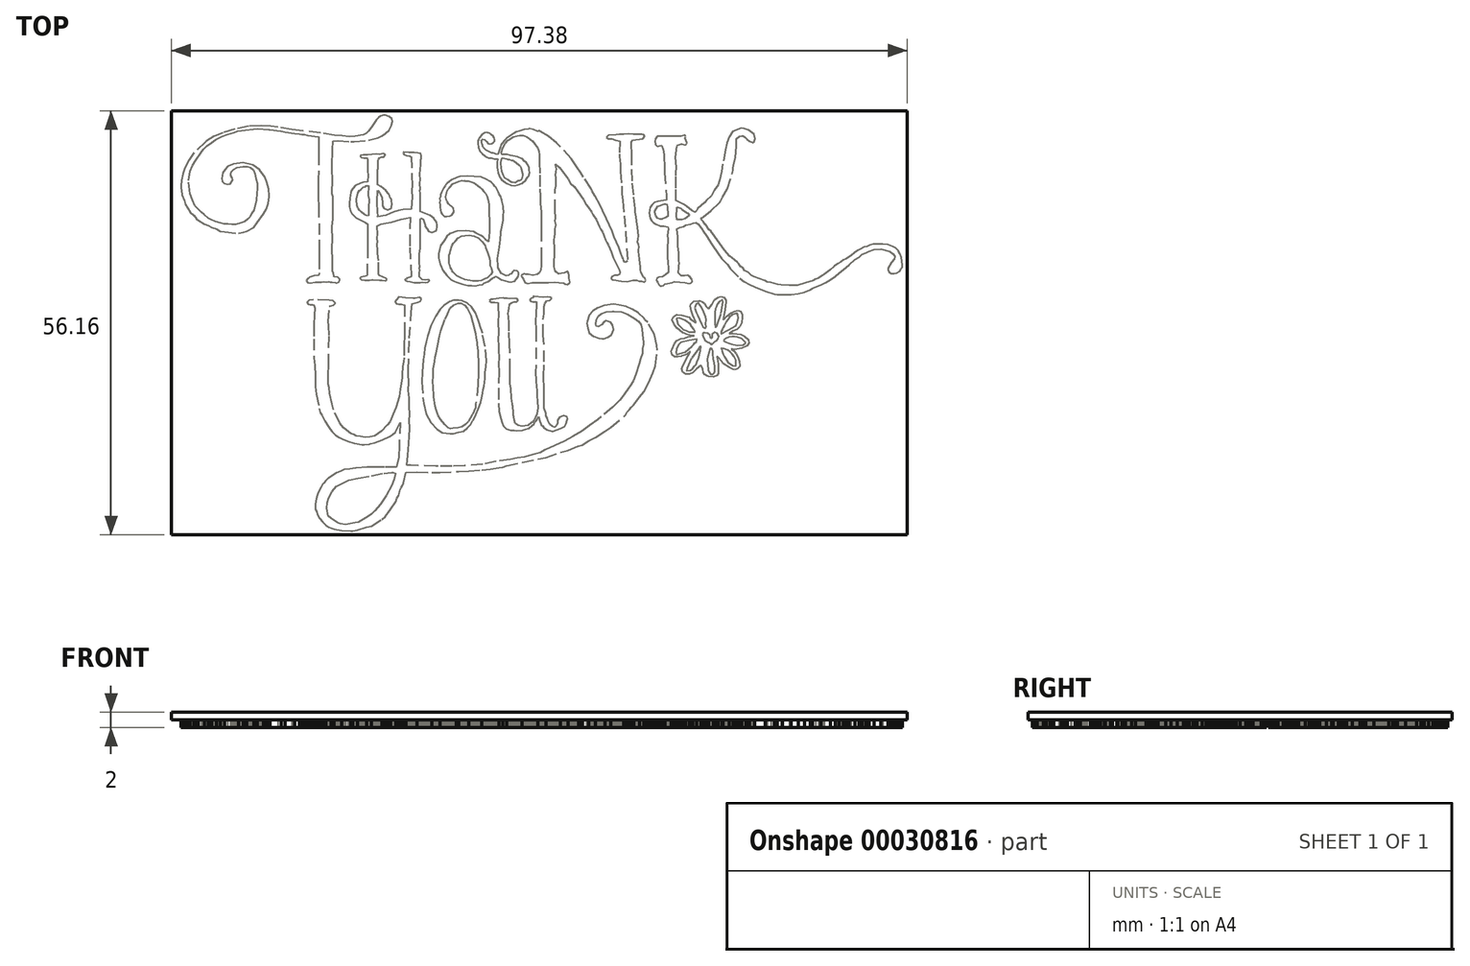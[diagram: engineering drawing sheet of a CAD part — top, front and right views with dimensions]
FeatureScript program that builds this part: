
annotation { "Feature Type Name" : "Feature", "Feature Type Description" : "" }
export const myFeature = defineFeature(function(context is Context, id is Id, definition is map)
    precondition{}
    {
        {
            var Q0;
            Q0=qCreatedBy(makeId("Top.planeOp"),FACE);
            var sketch = newSketch(context, id + "F0", { "sketchPlane" : qUnion([Q0])});
            skLineSegment(sketch, "E0", {"start": v(-26.64, -26.6) * mm, "end": v(-26.83, -26.5) * mm});
            skLineSegment(sketch, "E1", {"start": v(-26.83, -26.5) * mm, "end": v(-27.1, -26.42) * mm});
            skLineSegment(sketch, "E2", {"start": v(-27.1, -26.42) * mm, "end": v(-27.5, -26.13) * mm});
            skLineSegment(sketch, "E3", {"start": v(-27.5, -26.13) * mm, "end": v(-27.9, -25.88) * mm});
            skLineSegment(sketch, "E4", {"start": v(-27.9, -25.88) * mm, "end": v(-28.23, -25.57) * mm});
            skLineSegment(sketch, "E5", {"start": v(-28.23, -25.57) * mm, "end": v(-28.44, -24.57) * mm});
            skLineSegment(sketch, "E6", {"start": v(-28.44, -24.57) * mm, "end": v(-28.37, -23.8) * mm});
            skLineSegment(sketch, "E7", {"start": v(-28.37, -23.8) * mm, "end": v(-28.18, -23.16) * mm});
            skLineSegment(sketch, "E8", {"start": v(-28.18, -23.16) * mm, "end": v(-27.73, -22.34) * mm});
            skLineSegment(sketch, "E9", {"start": v(-27.73, -22.34) * mm, "end": v(-27.17, -21.66) * mm});
            skLineSegment(sketch, "E10", {"start": v(-27.17, -21.66) * mm, "end": v(-26.54, -21.29) * mm});
            skLineSegment(sketch, "E11", {"start": v(-26.54, -21.29) * mm, "end": v(-25.52, -20.83) * mm});
            skLineSegment(sketch, "E12", {"start": v(-25.52, -20.83) * mm, "end": v(-24.32, -20.52) * mm});
            skLineSegment(sketch, "E13", {"start": v(-24.32, -20.52) * mm, "end": v(-22.57, -20.23) * mm});
            skLineSegment(sketch, "E14", {"start": v(-22.57, -20.23) * mm, "end": v(-20.9, -19.88) * mm});
            skLineSegment(sketch, "E15", {"start": v(-20.9, -19.88) * mm, "end": v(-19.84, -19.8) * mm});
            skLineSegment(sketch, "E16", {"start": v(-19.84, -19.8) * mm, "end": v(-19.66, -19.78) * mm});
            skLineSegment(sketch, "E17", {"start": v(-19.66, -19.78) * mm, "end": v(-19.37, -19.88) * mm});
            skLineSegment(sketch, "E18", {"start": v(-19.37, -19.88) * mm, "end": v(-19.55, -20.76) * mm});
            skLineSegment(sketch, "E19", {"start": v(-19.55, -20.76) * mm, "end": v(-19.9, -21.55) * mm});
            skLineSegment(sketch, "E20", {"start": v(-19.9, -21.55) * mm, "end": v(-20.56, -22.85) * mm});
            skLineSegment(sketch, "E21", {"start": v(-20.56, -22.85) * mm, "end": v(-21.33, -23.96) * mm});
            skLineSegment(sketch, "E22", {"start": v(-21.33, -23.96) * mm, "end": v(-22.07, -24.88) * mm});
            skLineSegment(sketch, "E23", {"start": v(-22.07, -24.88) * mm, "end": v(-22.52, -25.28) * mm});
            skLineSegment(sketch, "E24", {"start": v(-22.52, -25.28) * mm, "end": v(-22.96, -25.65) * mm});
            skLineSegment(sketch, "E25", {"start": v(-22.96, -25.65) * mm, "end": v(-23.6, -26.02) * mm});
            skLineSegment(sketch, "E26", {"start": v(-23.6, -26.02) * mm, "end": v(-24.24, -26.37) * mm});
            skLineSegment(sketch, "E27", {"start": v(-24.24, -26.37) * mm, "end": v(-24.68, -26.47) * mm});
            skLineSegment(sketch, "E28", {"start": v(-24.68, -26.47) * mm, "end": v(-25.98, -26.74) * mm});
            skLineSegment(sketch, "E29", {"start": v(-25.98, -26.74) * mm, "end": v(-26.64, -26.6) * mm});
            skLineSegment(sketch, "E30", {"start": v(-19.42, 2.85) * mm, "end": v(-19.42, 2.82) * mm});
            skLineSegment(sketch, "E31", {"start": v(-19.42, 2.82) * mm, "end": v(-19.23, 2.55) * mm});
            skLineSegment(sketch, "E32", {"start": v(-19.23, 2.55) * mm, "end": v(-18.94, 2.53) * mm});
            skLineSegment(sketch, "E33", {"start": v(-18.94, 2.53) * mm, "end": v(-18.6, 2.53) * mm});
            skLineSegment(sketch, "E34", {"start": v(-18.6, 2.53) * mm, "end": v(-18.15, 2.37) * mm});
            skLineSegment(sketch, "E35", {"start": v(-18.15, 2.37) * mm, "end": v(-18.15, -0.46) * mm});
            skLineSegment(sketch, "E36", {"start": v(-18.15, -0.46) * mm, "end": v(-18.18, -1.05) * mm});
            skLineSegment(sketch, "E37", {"start": v(-18.18, -1.05) * mm, "end": v(-18.18, -1.15) * mm});
            skLineSegment(sketch, "E38", {"start": v(-18.18, -1.15) * mm, "end": v(-18.15, -1.36) * mm});
            skLineSegment(sketch, "E39", {"start": v(-18.15, -1.36) * mm, "end": v(-18.18, -1.73) * mm});
            skLineSegment(sketch, "E40", {"start": v(-18.18, -1.73) * mm, "end": v(-18.2, -2.77) * mm});
            skLineSegment(sketch, "E41", {"start": v(-18.2, -2.77) * mm, "end": v(-18.2, -4.62) * mm});
            skLineSegment(sketch, "E42", {"start": v(-18.2, -4.62) * mm, "end": v(-18.3, -5.15) * mm});
            skLineSegment(sketch, "E43", {"start": v(-18.3, -5.15) * mm, "end": v(-18.39, -5.73) * mm});
            skLineSegment(sketch, "E44", {"start": v(-18.39, -5.73) * mm, "end": v(-18.5, -6.84) * mm});
            skLineSegment(sketch, "E45", {"start": v(-18.5, -6.84) * mm, "end": v(-18.47, -7.13) * mm});
            skLineSegment(sketch, "E46", {"start": v(-18.47, -7.13) * mm, "end": v(-18.47, -7.2) * mm});
            skLineSegment(sketch, "E47", {"start": v(-18.47, -7.2) * mm, "end": v(-18.55, -7.69) * mm});
            skLineSegment(sketch, "E48", {"start": v(-18.55, -7.69) * mm, "end": v(-18.7, -8.72) * mm});
            skLineSegment(sketch, "E49", {"start": v(-18.7, -8.72) * mm, "end": v(-18.86, -9.75) * mm});
            skLineSegment(sketch, "E50", {"start": v(-18.86, -9.75) * mm, "end": v(-19.31, -11.23) * mm});
            skLineSegment(sketch, "E51", {"start": v(-19.31, -11.23) * mm, "end": v(-19.71, -12.1) * mm});
            skLineSegment(sketch, "E52", {"start": v(-19.71, -12.1) * mm, "end": v(-20.08, -13.03) * mm});
            skLineSegment(sketch, "E53", {"start": v(-20.08, -13.03) * mm, "end": v(-20.45, -13.5) * mm});
            skLineSegment(sketch, "E54", {"start": v(-20.45, -13.5) * mm, "end": v(-21.19, -14.34) * mm});
            skLineSegment(sketch, "E55", {"start": v(-21.19, -14.34) * mm, "end": v(-22.12, -14.94) * mm});
            skLineSegment(sketch, "E56", {"start": v(-22.12, -14.94) * mm, "end": v(-22.72, -15.07) * mm});
            skLineSegment(sketch, "E57", {"start": v(-22.72, -15.07) * mm, "end": v(-23.34, -15.12) * mm});
            skLineSegment(sketch, "E58", {"start": v(-23.34, -15.12) * mm, "end": v(-23.99, -15.05) * mm});
            skLineSegment(sketch, "E59", {"start": v(-23.99, -15.05) * mm, "end": v(-24.58, -14.94) * mm});
            skLineSegment(sketch, "E60", {"start": v(-24.58, -14.94) * mm, "end": v(-24.87, -14.75) * mm});
            skLineSegment(sketch, "E61", {"start": v(-24.87, -14.75) * mm, "end": v(-25.24, -14.65) * mm});
            skLineSegment(sketch, "E62", {"start": v(-25.24, -14.65) * mm, "end": v(-25.53, -14.43) * mm});
            skLineSegment(sketch, "E63", {"start": v(-25.53, -14.43) * mm, "end": v(-26.2, -13.9) * mm});
            skLineSegment(sketch, "E64", {"start": v(-26.2, -13.9) * mm, "end": v(-26.72, -13.24) * mm});
            skLineSegment(sketch, "E65", {"start": v(-26.72, -13.24) * mm, "end": v(-27.57, -11.47) * mm});
            skLineSegment(sketch, "E66", {"start": v(-27.57, -11.47) * mm, "end": v(-27.73, -10.73) * mm});
            skLineSegment(sketch, "E67", {"start": v(-27.73, -10.73) * mm, "end": v(-28.07, -9.3) * mm});
            skLineSegment(sketch, "E68", {"start": v(-28.07, -9.3) * mm, "end": v(-28.15, -8.56) * mm});
            skLineSegment(sketch, "E69", {"start": v(-28.15, -8.56) * mm, "end": v(-28.26, -8.08) * mm});
            skLineSegment(sketch, "E70", {"start": v(-28.26, -8.08) * mm, "end": v(-28.28, -7.45) * mm});
            skLineSegment(sketch, "E71", {"start": v(-28.28, -7.45) * mm, "end": v(-28.28, -6.81) * mm});
            skLineSegment(sketch, "E72", {"start": v(-28.28, -6.81) * mm, "end": v(-28.2, -5.57) * mm});
            skLineSegment(sketch, "E73", {"start": v(-28.2, -5.57) * mm, "end": v(-28.12, -1.63) * mm});
            skLineSegment(sketch, "E74", {"start": v(-28.12, -1.63) * mm, "end": v(-28.2, -0.33) * mm});
            skLineSegment(sketch, "E75", {"start": v(-28.2, -0.33) * mm, "end": v(-28.23, 0.2) * mm});
            skLineSegment(sketch, "E76", {"start": v(-28.23, 0.2) * mm, "end": v(-28.12, 2.24) * mm});
            skLineSegment(sketch, "E77", {"start": v(-28.12, 2.24) * mm, "end": v(-28.02, 2.24) * mm});
            skLineSegment(sketch, "E78", {"start": v(-28.02, 2.24) * mm, "end": v(-27.57, 2.35) * mm});
            skLineSegment(sketch, "E79", {"start": v(-27.57, 2.35) * mm, "end": v(-27.33, 2.63) * mm});
            skLineSegment(sketch, "E80", {"start": v(-27.33, 2.63) * mm, "end": v(-27.6, 2.98) * mm});
            skLineSegment(sketch, "E81", {"start": v(-27.6, 2.98) * mm, "end": v(-28.15, 3) * mm});
            skLineSegment(sketch, "E82", {"start": v(-28.15, 3) * mm, "end": v(-30.19, 3.08) * mm});
            skLineSegment(sketch, "E83", {"start": v(-30.19, 3.08) * mm, "end": v(-30.8, 3.03) * mm});
            skLineSegment(sketch, "E84", {"start": v(-30.8, 3.03) * mm, "end": v(-31.06, 2.74) * mm});
            skLineSegment(sketch, "E85", {"start": v(-31.06, 2.74) * mm, "end": v(-31.06, 2.71) * mm});
            skLineSegment(sketch, "E86", {"start": v(-31.06, 2.71) * mm, "end": v(-30.93, 2.53) * mm});
            skLineSegment(sketch, "E87", {"start": v(-30.93, 2.53) * mm, "end": v(-30.66, 2.47) * mm});
            skLineSegment(sketch, "E88", {"start": v(-30.66, 2.47) * mm, "end": v(-30.36, 2.45) * mm});
            skLineSegment(sketch, "E89", {"start": v(-30.36, 2.45) * mm, "end": v(-30.14, 2.37) * mm});
            skLineSegment(sketch, "E90", {"start": v(-30.14, 2.37) * mm, "end": v(-30.03, 1.97) * mm});
            skLineSegment(sketch, "E91", {"start": v(-30.03, 1.97) * mm, "end": v(-30.1, 1.05) * mm});
            skLineSegment(sketch, "E92", {"start": v(-30.1, 1.05) * mm, "end": v(-30.14, -0.25) * mm});
            skLineSegment(sketch, "E93", {"start": v(-30.14, -0.25) * mm, "end": v(-30.14, -2.1) * mm});
            skLineSegment(sketch, "E94", {"start": v(-30.14, -2.1) * mm, "end": v(-30.16, -4.33) * mm});
            skLineSegment(sketch, "E95", {"start": v(-30.16, -4.33) * mm, "end": v(-30.16, -4.6) * mm});
            skLineSegment(sketch, "E96", {"start": v(-30.16, -4.6) * mm, "end": v(-30.06, -5.6) * mm});
            skLineSegment(sketch, "E97", {"start": v(-30.06, -5.6) * mm, "end": v(-29.98, -6.97) * mm});
            skLineSegment(sketch, "E98", {"start": v(-29.98, -6.97) * mm, "end": v(-29.95, -7.66) * mm});
            skLineSegment(sketch, "E99", {"start": v(-29.95, -7.66) * mm, "end": v(-29.98, -8.24) * mm});
            skLineSegment(sketch, "E100", {"start": v(-29.98, -8.24) * mm, "end": v(-29.98, -8.4) * mm});
            skLineSegment(sketch, "E101", {"start": v(-29.98, -8.4) * mm, "end": v(-29.82, -9.4) * mm});
            skLineSegment(sketch, "E102", {"start": v(-29.82, -9.4) * mm, "end": v(-29.45, -11.36) * mm});
            skLineSegment(sketch, "E103", {"start": v(-29.45, -11.36) * mm, "end": v(-29.33, -11.82) * mm});
            skLineSegment(sketch, "E104", {"start": v(-29.33, -11.82) * mm, "end": v(-29.1, -12.24) * mm});
            skLineSegment(sketch, "E105", {"start": v(-29.1, -12.24) * mm, "end": v(-28.72, -13.02) * mm});
            skLineSegment(sketch, "E106", {"start": v(-28.72, -13.02) * mm, "end": v(-28.28, -13.72) * mm});
            skLineSegment(sketch, "E107", {"start": v(-28.28, -13.72) * mm, "end": v(-28, -14.06) * mm});
            skLineSegment(sketch, "E108", {"start": v(-28, -14.06) * mm, "end": v(-27.73, -14.4) * mm});
            skLineSegment(sketch, "E109", {"start": v(-27.73, -14.4) * mm, "end": v(-27.3, -14.84) * mm});
            skLineSegment(sketch, "E110", {"start": v(-27.3, -14.84) * mm, "end": v(-26.78, -15.17) * mm});
            skLineSegment(sketch, "E111", {"start": v(-26.78, -15.17) * mm, "end": v(-26.43, -15.36) * mm});
            skLineSegment(sketch, "E112", {"start": v(-26.43, -15.36) * mm, "end": v(-25.66, -15.67) * mm});
            skLineSegment(sketch, "E113", {"start": v(-25.66, -15.67) * mm, "end": v(-24.84, -15.89) * mm});
            skLineSegment(sketch, "E114", {"start": v(-24.84, -15.89) * mm, "end": v(-24.74, -15.91) * mm});
            skLineSegment(sketch, "E115", {"start": v(-24.74, -15.91) * mm, "end": v(-23.81, -16.1) * mm});
            skLineSegment(sketch, "E116", {"start": v(-23.81, -16.1) * mm, "end": v(-23.47, -16.13) * mm});
            skLineSegment(sketch, "E117", {"start": v(-23.47, -16.13) * mm, "end": v(-22.78, -16.02) * mm});
            skLineSegment(sketch, "E118", {"start": v(-22.78, -16.02) * mm, "end": v(-22.67, -16) * mm});
            skLineSegment(sketch, "E119", {"start": v(-22.67, -16) * mm, "end": v(-22.1, -15.84) * mm});
            skLineSegment(sketch, "E120", {"start": v(-22.1, -15.84) * mm, "end": v(-21.09, -15.46) * mm});
            skLineSegment(sketch, "E121", {"start": v(-21.09, -15.46) * mm, "end": v(-20.13, -15.01) * mm});
            skLineSegment(sketch, "E122", {"start": v(-20.13, -15.01) * mm, "end": v(-19.74, -14.75) * mm});
            skLineSegment(sketch, "E123", {"start": v(-19.74, -14.75) * mm, "end": v(-19.34, -14.46) * mm});
            skLineSegment(sketch, "E124", {"start": v(-19.34, -14.46) * mm, "end": v(-19.05, -13.8) * mm});
            skLineSegment(sketch, "E125", {"start": v(-19.05, -13.8) * mm, "end": v(-18.7, -13.16) * mm});
            skLineSegment(sketch, "E126", {"start": v(-18.7, -13.16) * mm, "end": v(-18.86, -16.23) * mm});
            skLineSegment(sketch, "E127", {"start": v(-18.86, -16.23) * mm, "end": v(-18.94, -17.75) * mm});
            skLineSegment(sketch, "E128", {"start": v(-18.94, -17.75) * mm, "end": v(-19.2, -19.12) * mm});
            skLineSegment(sketch, "E129", {"start": v(-19.2, -19.12) * mm, "end": v(-20.82, -19.12) * mm});
            skLineSegment(sketch, "E130", {"start": v(-20.82, -19.12) * mm, "end": v(-21.46, -19.09) * mm});
            skLineSegment(sketch, "E131", {"start": v(-21.46, -19.09) * mm, "end": v(-22.28, -19.06) * mm});
            skLineSegment(sketch, "E132", {"start": v(-22.28, -19.06) * mm, "end": v(-23.1, -19.09) * mm});
            skLineSegment(sketch, "E133", {"start": v(-23.1, -19.09) * mm, "end": v(-24.66, -19.2) * mm});
            skLineSegment(sketch, "E134", {"start": v(-24.66, -19.2) * mm, "end": v(-25.4, -19.35) * mm});
            skLineSegment(sketch, "E135", {"start": v(-25.4, -19.35) * mm, "end": v(-26.17, -19.43) * mm});
            skLineSegment(sketch, "E136", {"start": v(-26.17, -19.43) * mm, "end": v(-26.7, -19.64) * mm});
            skLineSegment(sketch, "E137", {"start": v(-26.7, -19.64) * mm, "end": v(-27.17, -19.86) * mm});
            skLineSegment(sketch, "E138", {"start": v(-27.17, -19.86) * mm, "end": v(-28.2, -20.54) * mm});
            skLineSegment(sketch, "E139", {"start": v(-28.2, -20.54) * mm, "end": v(-28.31, -20.62) * mm});
            skLineSegment(sketch, "E140", {"start": v(-28.31, -20.62) * mm, "end": v(-28.42, -20.73) * mm});
            skLineSegment(sketch, "E141", {"start": v(-28.42, -20.73) * mm, "end": v(-28.63, -20.94) * mm});
            skLineSegment(sketch, "E142", {"start": v(-28.63, -20.94) * mm, "end": v(-28.81, -21.15) * mm});
            skLineSegment(sketch, "E143", {"start": v(-28.81, -21.15) * mm, "end": v(-29.02, -21.36) * mm});
            skLineSegment(sketch, "E144", {"start": v(-29.02, -21.36) * mm, "end": v(-29.21, -21.74) * mm});
            skLineSegment(sketch, "E145", {"start": v(-29.21, -21.74) * mm, "end": v(-29.58, -22.42) * mm});
            skLineSegment(sketch, "E146", {"start": v(-29.58, -22.42) * mm, "end": v(-29.75, -22.8) * mm});
            skLineSegment(sketch, "E147", {"start": v(-29.75, -22.8) * mm, "end": v(-29.87, -23.27) * mm});
            skLineSegment(sketch, "E148", {"start": v(-29.87, -23.27) * mm, "end": v(-29.95, -23.96) * mm});
            skLineSegment(sketch, "E149", {"start": v(-29.95, -23.96) * mm, "end": v(-29.95, -24.7) * mm});
            skLineSegment(sketch, "E150", {"start": v(-29.95, -24.7) * mm, "end": v(-29.8, -24.99) * mm});
            skLineSegment(sketch, "E151", {"start": v(-29.8, -24.99) * mm, "end": v(-29.71, -25.33) * mm});
            skLineSegment(sketch, "E152", {"start": v(-29.71, -25.33) * mm, "end": v(-29.38, -25.86) * mm});
            skLineSegment(sketch, "E153", {"start": v(-29.38, -25.86) * mm, "end": v(-29.02, -26.34) * mm});
            skLineSegment(sketch, "E154", {"start": v(-29.02, -26.34) * mm, "end": v(-28.58, -26.79) * mm});
            skLineSegment(sketch, "E155", {"start": v(-28.58, -26.79) * mm, "end": v(-28.18, -27) * mm});
            skLineSegment(sketch, "E156", {"start": v(-28.18, -27) * mm, "end": v(-27.84, -27.18) * mm});
            skLineSegment(sketch, "E157", {"start": v(-27.84, -27.18) * mm, "end": v(-27.5, -27.3) * mm});
            skLineSegment(sketch, "E158", {"start": v(-27.5, -27.3) * mm, "end": v(-26.48, -27.48) * mm});
            skLineSegment(sketch, "E159", {"start": v(-26.48, -27.48) * mm, "end": v(-25.3, -27.5) * mm});
            skLineSegment(sketch, "E160", {"start": v(-25.3, -27.5) * mm, "end": v(-25, -27.5) * mm});
            skLineSegment(sketch, "E161", {"start": v(-25, -27.5) * mm, "end": v(-24.37, -27.4) * mm});
            skLineSegment(sketch, "E162", {"start": v(-24.37, -27.4) * mm, "end": v(-23.15, -27.05) * mm});
            skLineSegment(sketch, "E163", {"start": v(-23.15, -27.05) * mm, "end": v(-22.57, -26.87) * mm});
            skLineSegment(sketch, "E164", {"start": v(-22.57, -26.87) * mm, "end": v(-21.17, -26) * mm});
            skLineSegment(sketch, "E165", {"start": v(-21.17, -26) * mm, "end": v(-20.72, -25.63) * mm});
            skLineSegment(sketch, "E166", {"start": v(-20.72, -25.63) * mm, "end": v(-20.35, -25.15) * mm});
            skLineSegment(sketch, "E167", {"start": v(-20.35, -25.15) * mm, "end": v(-20, -24.67) * mm});
            skLineSegment(sketch, "E168", {"start": v(-20, -24.67) * mm, "end": v(-19.31, -23.67) * mm});
            skLineSegment(sketch, "E169", {"start": v(-19.31, -23.67) * mm, "end": v(-19.16, -23.22) * mm});
            skLineSegment(sketch, "E170", {"start": v(-19.16, -23.22) * mm, "end": v(-18.92, -22.82) * mm});
            skLineSegment(sketch, "E171", {"start": v(-18.92, -22.82) * mm, "end": v(-18.7, -22.08) * mm});
            skLineSegment(sketch, "E172", {"start": v(-18.7, -22.08) * mm, "end": v(-18.63, -21.81) * mm});
            skLineSegment(sketch, "E173", {"start": v(-18.63, -21.81) * mm, "end": v(-18.41, -21.52) * mm});
            skLineSegment(sketch, "E174", {"start": v(-18.41, -21.52) * mm, "end": v(-18.26, -21.15) * mm});
            skLineSegment(sketch, "E175", {"start": v(-18.26, -21.15) * mm, "end": v(-18, -19.78) * mm});
            skLineSegment(sketch, "E176", {"start": v(-18, -19.78) * mm, "end": v(-16.51, -19.75) * mm});
            skLineSegment(sketch, "E177", {"start": v(-16.51, -19.75) * mm, "end": v(-14.53, -19.78) * mm});
            skLineSegment(sketch, "E178", {"start": v(-14.53, -19.78) * mm, "end": v(-13.47, -19.8) * mm});
            skLineSegment(sketch, "E179", {"start": v(-13.47, -19.8) * mm, "end": v(-11.32, -19.64) * mm});
            skLineSegment(sketch, "E180", {"start": v(-11.32, -19.64) * mm, "end": v(-10.98, -19.64) * mm});
            skLineSegment(sketch, "E181", {"start": v(-10.98, -19.64) * mm, "end": v(-9.66, -19.57) * mm});
            skLineSegment(sketch, "E182", {"start": v(-9.66, -19.57) * mm, "end": v(-7.91, -19.49) * mm});
            skLineSegment(sketch, "E183", {"start": v(-7.91, -19.49) * mm, "end": v(-6.77, -19.33) * mm});
            skLineSegment(sketch, "E184", {"start": v(-6.77, -19.33) * mm, "end": v(-5.63, -19.17) * mm});
            skLineSegment(sketch, "E185", {"start": v(-5.63, -19.17) * mm, "end": v(-5.16, -19.06) * mm});
            skLineSegment(sketch, "E186", {"start": v(-5.16, -19.06) * mm, "end": v(-4.63, -18.9) * mm});
            skLineSegment(sketch, "E187", {"start": v(-4.63, -18.9) * mm, "end": v(-2.57, -18.43) * mm});
            skLineSegment(sketch, "E188", {"start": v(-2.57, -18.43) * mm, "end": v(-0.48, -17.98) * mm});
            skLineSegment(sketch, "E189", {"start": v(-0.48, -17.98) * mm, "end": v(0.58, -17.8) * mm});
            skLineSegment(sketch, "E190", {"start": v(0.58, -17.8) * mm, "end": v(2.46, -17.13) * mm});
            skLineSegment(sketch, "E191", {"start": v(2.46, -17.13) * mm, "end": v(3.47, -16.87) * mm});
            skLineSegment(sketch, "E192", {"start": v(3.47, -16.87) * mm, "end": v(4.87, -16.31) * mm});
            skLineSegment(sketch, "E193", {"start": v(4.87, -16.31) * mm, "end": v(5.35, -16.15) * mm});
            skLineSegment(sketch, "E194", {"start": v(5.35, -16.15) * mm, "end": v(6.22, -15.62) * mm});
            skLineSegment(sketch, "E195", {"start": v(6.22, -15.62) * mm, "end": v(7.14, -15.17) * mm});
            skLineSegment(sketch, "E196", {"start": v(7.14, -15.17) * mm, "end": v(8.39, -14.35) * mm});
            skLineSegment(sketch, "E197", {"start": v(8.39, -14.35) * mm, "end": v(9.13, -13.82) * mm});
            skLineSegment(sketch, "E198", {"start": v(9.13, -13.82) * mm, "end": v(10.87, -12.42) * mm});
            skLineSegment(sketch, "E199", {"start": v(10.87, -12.42) * mm, "end": v(11.14, -12.16) * mm});
            skLineSegment(sketch, "E200", {"start": v(11.14, -12.16) * mm, "end": v(11.32, -11.79) * mm});
            skLineSegment(sketch, "E201", {"start": v(11.32, -11.79) * mm, "end": v(11.62, -11.5) * mm});
            skLineSegment(sketch, "E202", {"start": v(11.62, -11.5) * mm, "end": v(11.9, -11.15) * mm});
            skLineSegment(sketch, "E203", {"start": v(11.9, -11.15) * mm, "end": v(12.2, -10.86) * mm});
            skLineSegment(sketch, "E204", {"start": v(12.2, -10.86) * mm, "end": v(12.96, -9.8) * mm});
            skLineSegment(sketch, "E205", {"start": v(12.96, -9.8) * mm, "end": v(13.52, -9.11) * mm});
            skLineSegment(sketch, "E206", {"start": v(13.52, -9.11) * mm, "end": v(14, -8.32) * mm});
            skLineSegment(sketch, "E207", {"start": v(14, -8.32) * mm, "end": v(14.34, -7.47) * mm});
            skLineSegment(sketch, "E208", {"start": v(14.34, -7.47) * mm, "end": v(14.73, -6.56) * mm});
            skLineSegment(sketch, "E209", {"start": v(14.73, -6.56) * mm, "end": v(15.03, -5.68) * mm});
            skLineSegment(sketch, "E210", {"start": v(15.03, -5.68) * mm, "end": v(15.3, -3.61) * mm});
            skLineSegment(sketch, "E211", {"start": v(15.3, -3.61) * mm, "end": v(15.27, -2.95) * mm});
            skLineSegment(sketch, "E212", {"start": v(15.27, -2.95) * mm, "end": v(14.9, -1.47) * mm});
            skLineSegment(sketch, "E213", {"start": v(14.9, -1.47) * mm, "end": v(14.02, 0.12) * mm});
            skLineSegment(sketch, "E214", {"start": v(14.02, 0.12) * mm, "end": v(13.68, 0.38) * mm});
            skLineSegment(sketch, "E215", {"start": v(13.68, 0.38) * mm, "end": v(13.57, 0.57) * mm});
            skLineSegment(sketch, "E216", {"start": v(13.57, 0.57) * mm, "end": v(12.75, 1.34) * mm});
            skLineSegment(sketch, "E217", {"start": v(12.75, 1.34) * mm, "end": v(12.01, 1.81) * mm});
            skLineSegment(sketch, "E218", {"start": v(12.01, 1.81) * mm, "end": v(11.17, 2.2) * mm});
            skLineSegment(sketch, "E219", {"start": v(11.17, 2.2) * mm, "end": v(10.24, 2.4) * mm});
            skLineSegment(sketch, "E220", {"start": v(10.24, 2.4) * mm, "end": v(9.55, 2.47) * mm});
            skLineSegment(sketch, "E221", {"start": v(9.55, 2.47) * mm, "end": v(8.26, 2.29) * mm});
            skLineSegment(sketch, "E222", {"start": v(8.26, 2.29) * mm, "end": v(7.45, 2.02) * mm});
            skLineSegment(sketch, "E223", {"start": v(7.45, 2.02) * mm, "end": v(6.83, 1.6) * mm});
            skLineSegment(sketch, "E224", {"start": v(6.83, 1.6) * mm, "end": v(6.3, 1.02) * mm});
            skLineSegment(sketch, "E225", {"start": v(6.3, 1.02) * mm, "end": v(6, 0.2) * mm});
            skLineSegment(sketch, "E226", {"start": v(6, 0.2) * mm, "end": v(5.98, -0.07) * mm});
            skLineSegment(sketch, "E227", {"start": v(5.98, -0.07) * mm, "end": v(6.08, -0.7) * mm});
            skLineSegment(sketch, "E228", {"start": v(6.08, -0.7) * mm, "end": v(6.32, -1.28) * mm});
            skLineSegment(sketch, "E229", {"start": v(6.32, -1.28) * mm, "end": v(6.84, -1.72) * mm});
            skLineSegment(sketch, "E230", {"start": v(6.84, -1.72) * mm, "end": v(7.54, -2.02) * mm});
            skLineSegment(sketch, "E231", {"start": v(7.54, -2.02) * mm, "end": v(8.02, -2.05) * mm});
            skLineSegment(sketch, "E232", {"start": v(8.02, -2.05) * mm, "end": v(8.23, -2.05) * mm});
            skLineSegment(sketch, "E233", {"start": v(8.23, -2.05) * mm, "end": v(8.75, -1.85) * mm});
            skLineSegment(sketch, "E234", {"start": v(8.75, -1.85) * mm, "end": v(9.18, -1.57) * mm});
            skLineSegment(sketch, "E235", {"start": v(9.18, -1.57) * mm, "end": v(9.26, -1.5) * mm});
            skLineSegment(sketch, "E236", {"start": v(9.26, -1.5) * mm, "end": v(9.52, -0.83) * mm});
            skLineSegment(sketch, "E237", {"start": v(9.52, -0.83) * mm, "end": v(9.4, -0.3) * mm});
            skLineSegment(sketch, "E238", {"start": v(9.4, -0.3) * mm, "end": v(9.13, 0.1) * mm});
            skLineSegment(sketch, "E239", {"start": v(9.13, 0.1) * mm, "end": v(8.6, 0.28) * mm});
            skLineSegment(sketch, "E240", {"start": v(8.6, 0.28) * mm, "end": v(8.52, 0.28) * mm});
            skLineSegment(sketch, "E241", {"start": v(8.52, 0.28) * mm, "end": v(8.22, 0.07) * mm});
            skLineSegment(sketch, "E242", {"start": v(8.22, 0.07) * mm, "end": v(7.94, -0.25) * mm});
            skLineSegment(sketch, "E243", {"start": v(7.94, -0.25) * mm, "end": v(7.49, -0.46) * mm});
            skLineSegment(sketch, "E244", {"start": v(7.49, -0.46) * mm, "end": v(7.22, -0.44) * mm});
            skLineSegment(sketch, "E245", {"start": v(7.22, -0.44) * mm, "end": v(7.2, -0.17) * mm});
            skLineSegment(sketch, "E246", {"start": v(7.2, -0.17) * mm, "end": v(7.22, 0.38) * mm});
            skLineSegment(sketch, "E247", {"start": v(7.22, 0.38) * mm, "end": v(7.51, 0.94) * mm});
            skLineSegment(sketch, "E248", {"start": v(7.51, 0.94) * mm, "end": v(7.89, 1.2) * mm});
            skLineSegment(sketch, "E249", {"start": v(7.89, 1.2) * mm, "end": v(8.58, 1.46) * mm});
            skLineSegment(sketch, "E250", {"start": v(8.58, 1.46) * mm, "end": v(9.37, 1.57) * mm});
            skLineSegment(sketch, "E251", {"start": v(9.37, 1.57) * mm, "end": v(9.58, 1.57) * mm});
            skLineSegment(sketch, "E252", {"start": v(9.58, 1.57) * mm, "end": v(10.53, 1.47) * mm});
            skLineSegment(sketch, "E253", {"start": v(10.53, 1.47) * mm, "end": v(11.38, 1.18) * mm});
            skLineSegment(sketch, "E254", {"start": v(11.38, 1.18) * mm, "end": v(12.33, 0.6) * mm});
            skLineSegment(sketch, "E255", {"start": v(12.33, 0.6) * mm, "end": v(12.8, 0.23) * mm});
            skLineSegment(sketch, "E256", {"start": v(12.8, 0.23) * mm, "end": v(13.15, -0.23) * mm});
            skLineSegment(sketch, "E257", {"start": v(13.15, -0.23) * mm, "end": v(13.3, -0.8) * mm});
            skLineSegment(sketch, "E258", {"start": v(13.3, -0.8) * mm, "end": v(13.34, -1.47) * mm});
            skLineSegment(sketch, "E259", {"start": v(13.34, -1.47) * mm, "end": v(13.44, -2.6) * mm});
            skLineSegment(sketch, "E260", {"start": v(13.44, -2.6) * mm, "end": v(13.44, -2.82) * mm});
            skLineSegment(sketch, "E261", {"start": v(13.44, -2.82) * mm, "end": v(13.34, -3.4) * mm});
            skLineSegment(sketch, "E262", {"start": v(13.34, -3.4) * mm, "end": v(13.3, -4.03) * mm});
            skLineSegment(sketch, "E263", {"start": v(13.3, -4.03) * mm, "end": v(13.1, -4.72) * mm});
            skLineSegment(sketch, "E264", {"start": v(13.1, -4.72) * mm, "end": v(12.91, -5.41) * mm});
            skLineSegment(sketch, "E265", {"start": v(12.91, -5.41) * mm, "end": v(12.46, -6.84) * mm});
            skLineSegment(sketch, "E266", {"start": v(12.46, -6.84) * mm, "end": v(12.13, -7.65) * mm});
            skLineSegment(sketch, "E267", {"start": v(12.13, -7.65) * mm, "end": v(11.7, -8.35) * mm});
            skLineSegment(sketch, "E268", {"start": v(11.7, -8.35) * mm, "end": v(11.48, -8.61) * mm});
            skLineSegment(sketch, "E269", {"start": v(11.48, -8.61) * mm, "end": v(10.92, -9.43) * mm});
            skLineSegment(sketch, "E270", {"start": v(10.92, -9.43) * mm, "end": v(10.34, -10.2) * mm});
            skLineSegment(sketch, "E271", {"start": v(10.34, -10.2) * mm, "end": v(9.42, -11.13) * mm});
            skLineSegment(sketch, "E272", {"start": v(9.42, -11.13) * mm, "end": v(7.91, -12.42) * mm});
            skLineSegment(sketch, "E273", {"start": v(7.91, -12.42) * mm, "end": v(7.43, -12.82) * mm});
            skLineSegment(sketch, "E274", {"start": v(7.43, -12.82) * mm, "end": v(6.38, -13.59) * mm});
            skLineSegment(sketch, "E275", {"start": v(6.38, -13.59) * mm, "end": v(5.32, -14.35) * mm});
            skLineSegment(sketch, "E276", {"start": v(5.32, -14.35) * mm, "end": v(4.16, -15.03) * mm});
            skLineSegment(sketch, "E277", {"start": v(4.16, -15.03) * mm, "end": v(2.96, -15.68) * mm});
            skLineSegment(sketch, "E278", {"start": v(2.96, -15.68) * mm, "end": v(1.72, -16.26) * mm});
            skLineSegment(sketch, "E279", {"start": v(1.72, -16.26) * mm, "end": v(0.42, -16.81) * mm});
            skLineSegment(sketch, "E280", {"start": v(0.42, -16.81) * mm, "end": v(-0.21, -17.16) * mm});
            skLineSegment(sketch, "E281", {"start": v(-0.21, -17.16) * mm, "end": v(-0.94, -17.38) * mm});
            skLineSegment(sketch, "E282", {"start": v(-0.94, -17.38) * mm, "end": v(-1.64, -17.56) * mm});
            skLineSegment(sketch, "E283", {"start": v(-1.64, -17.56) * mm, "end": v(-2.3, -17.77) * mm});
            skLineSegment(sketch, "E284", {"start": v(-2.3, -17.77) * mm, "end": v(-3.23, -17.87) * mm});
            skLineSegment(sketch, "E285", {"start": v(-3.23, -17.87) * mm, "end": v(-4.1, -18.06) * mm});
            skLineSegment(sketch, "E286", {"start": v(-4.1, -18.06) * mm, "end": v(-6, -18.35) * mm});
            skLineSegment(sketch, "E287", {"start": v(-6, -18.35) * mm, "end": v(-7.8, -18.7) * mm});
            skLineSegment(sketch, "E288", {"start": v(-7.8, -18.7) * mm, "end": v(-10.21, -18.88) * mm});
            skLineSegment(sketch, "E289", {"start": v(-10.21, -18.88) * mm, "end": v(-11.87, -18.94) * mm});
            skLineSegment(sketch, "E290", {"start": v(-11.87, -18.94) * mm, "end": v(-13.68, -18.98) * mm});
            skLineSegment(sketch, "E291", {"start": v(-13.68, -18.98) * mm, "end": v(-14.02, -18.98) * mm});
            skLineSegment(sketch, "E292", {"start": v(-14.02, -18.98) * mm, "end": v(-17.3, -18.82) * mm});
            skLineSegment(sketch, "E293", {"start": v(-17.3, -18.82) * mm, "end": v(-17.83, -18.82) * mm});
            skLineSegment(sketch, "E294", {"start": v(-17.83, -18.82) * mm, "end": v(-17.7, -17.49) * mm});
            skLineSegment(sketch, "E295", {"start": v(-17.7, -17.49) * mm, "end": v(-17.57, -16) * mm});
            skLineSegment(sketch, "E296", {"start": v(-17.57, -16) * mm, "end": v(-17.54, -14.99) * mm});
            skLineSegment(sketch, "E297", {"start": v(-17.54, -14.99) * mm, "end": v(-17.46, -14.04) * mm});
            skLineSegment(sketch, "E298", {"start": v(-17.46, -14.04) * mm, "end": v(-17.46, -13.82) * mm});
            skLineSegment(sketch, "E299", {"start": v(-17.46, -13.82) * mm, "end": v(-17.49, -12.98) * mm});
            skLineSegment(sketch, "E300", {"start": v(-17.49, -12.98) * mm, "end": v(-17.46, -12.03) * mm});
            skLineSegment(sketch, "E301", {"start": v(-17.46, -12.03) * mm, "end": v(-17.54, -11.07) * mm});
            skLineSegment(sketch, "E302", {"start": v(-17.54, -11.07) * mm, "end": v(-17.51, -9.93) * mm});
            skLineSegment(sketch, "E303", {"start": v(-17.51, -9.93) * mm, "end": v(-17.67, -8.93) * mm});
            skLineSegment(sketch, "E304", {"start": v(-17.67, -8.93) * mm, "end": v(-17.6, -7.87) * mm});
            skLineSegment(sketch, "E305", {"start": v(-17.6, -7.87) * mm, "end": v(-17.67, -6.76) * mm});
            skLineSegment(sketch, "E306", {"start": v(-17.67, -6.76) * mm, "end": v(-17.67, -6.2) * mm});
            skLineSegment(sketch, "E307", {"start": v(-17.67, -6.2) * mm, "end": v(-17.51, -2.02) * mm});
            skLineSegment(sketch, "E308", {"start": v(-17.51, -2.02) * mm, "end": v(-17.33, 0.25) * mm});
            skLineSegment(sketch, "E309", {"start": v(-17.33, 0.25) * mm, "end": v(-17.26, 1.42) * mm});
            skLineSegment(sketch, "E310", {"start": v(-17.26, 1.42) * mm, "end": v(-17.14, 2.58) * mm});
            skLineSegment(sketch, "E311", {"start": v(-17.14, 2.58) * mm, "end": v(-16.4, 2.77) * mm});
            skLineSegment(sketch, "E312", {"start": v(-16.4, 2.77) * mm, "end": v(-16.03, 2.87) * mm});
            skLineSegment(sketch, "E313", {"start": v(-16.03, 2.87) * mm, "end": v(-15.93, 3.14) * mm});
            skLineSegment(sketch, "E314", {"start": v(-15.93, 3.14) * mm, "end": v(-15.93, 3.21) * mm});
            skLineSegment(sketch, "E315", {"start": v(-15.93, 3.21) * mm, "end": v(-16.2, 3.37) * mm});
            skLineSegment(sketch, "E316", {"start": v(-16.2, 3.37) * mm, "end": v(-16.77, 3.27) * mm});
            skLineSegment(sketch, "E317", {"start": v(-16.77, 3.27) * mm, "end": v(-17.04, 3.27) * mm});
            skLineSegment(sketch, "E318", {"start": v(-17.04, 3.27) * mm, "end": v(-18.05, 3.35) * mm});
            skLineSegment(sketch, "E319", {"start": v(-18.05, 3.35) * mm, "end": v(-18.94, 3.43) * mm});
            skLineSegment(sketch, "E320", {"start": v(-18.94, 3.43) * mm, "end": v(-19.26, 3.08) * mm});
            skLineSegment(sketch, "E321", {"start": v(-19.26, 3.08) * mm, "end": v(-19.42, 2.85) * mm});
            skLineSegment(sketch, "E322", {"start": v(-20.95, 27.5) * mm, "end": v(-21.33, 27.4) * mm});
            skLineSegment(sketch, "E323", {"start": v(-21.33, 27.4) * mm, "end": v(-21.59, 27.19) * mm});
            skLineSegment(sketch, "E324", {"start": v(-21.59, 27.19) * mm, "end": v(-21.62, 27.16) * mm});
            skLineSegment(sketch, "E325", {"start": v(-21.62, 27.16) * mm, "end": v(-21.93, 26.87) * mm});
            skLineSegment(sketch, "E326", {"start": v(-21.93, 26.87) * mm, "end": v(-22.4, 26.1) * mm});
            skLineSegment(sketch, "E327", {"start": v(-22.4, 26.1) * mm, "end": v(-22.94, 25.41) * mm});
            skLineSegment(sketch, "E328", {"start": v(-22.94, 25.41) * mm, "end": v(-23.26, 25.12) * mm});
            skLineSegment(sketch, "E329", {"start": v(-23.26, 25.12) * mm, "end": v(-23.63, 24.9) * mm});
            skLineSegment(sketch, "E330", {"start": v(-23.63, 24.9) * mm, "end": v(-24.71, 24.73) * mm});
            skLineSegment(sketch, "E331", {"start": v(-24.71, 24.73) * mm, "end": v(-25.45, 24.67) * mm});
            skLineSegment(sketch, "E332", {"start": v(-25.45, 24.67) * mm, "end": v(-26.43, 24.8) * mm});
            skLineSegment(sketch, "E333", {"start": v(-26.43, 24.8) * mm, "end": v(-27.41, 24.86) * mm});
            skLineSegment(sketch, "E334", {"start": v(-27.41, 24.86) * mm, "end": v(-29.29, 25.15) * mm});
            skLineSegment(sketch, "E335", {"start": v(-29.29, 25.15) * mm, "end": v(-33.07, 25.63) * mm});
            skLineSegment(sketch, "E336", {"start": v(-33.07, 25.63) * mm, "end": v(-34.93, 25.94) * mm});
            skLineSegment(sketch, "E337", {"start": v(-34.93, 25.94) * mm, "end": v(-35.9, 26.05) * mm});
            skLineSegment(sketch, "E338", {"start": v(-35.9, 26.05) * mm, "end": v(-37.15, 26.1) * mm});
            skLineSegment(sketch, "E339", {"start": v(-37.15, 26.1) * mm, "end": v(-38.79, 26.05) * mm});
            skLineSegment(sketch, "E340", {"start": v(-38.79, 26.05) * mm, "end": v(-40.64, 25.7) * mm});
            skLineSegment(sketch, "E341", {"start": v(-40.64, 25.7) * mm, "end": v(-42.25, 25.2) * mm});
            skLineSegment(sketch, "E342", {"start": v(-42.25, 25.2) * mm, "end": v(-43.4, 24.73) * mm});
            skLineSegment(sketch, "E343", {"start": v(-43.4, 24.73) * mm, "end": v(-44.37, 24.12) * mm});
            skLineSegment(sketch, "E344", {"start": v(-44.37, 24.12) * mm, "end": v(-44.53, 23.98) * mm});
            skLineSegment(sketch, "E345", {"start": v(-44.53, 23.98) * mm, "end": v(-46.01, 22.56) * mm});
            skLineSegment(sketch, "E346", {"start": v(-46.01, 22.56) * mm, "end": v(-46.69, 21.62) * mm});
            skLineSegment(sketch, "E347", {"start": v(-46.69, 21.62) * mm, "end": v(-47.23, 20.54) * mm});
            skLineSegment(sketch, "E348", {"start": v(-47.23, 20.54) * mm, "end": v(-47.52, 19.76) * mm});
            skLineSegment(sketch, "E349", {"start": v(-47.52, 19.76) * mm, "end": v(-47.7, 18.9) * mm});
            skLineSegment(sketch, "E350", {"start": v(-47.7, 18.9) * mm, "end": v(-47.76, 18.22) * mm});
            skLineSegment(sketch, "E351", {"start": v(-47.76, 18.22) * mm, "end": v(-47.76, 17.95) * mm});
            skLineSegment(sketch, "E352", {"start": v(-47.76, 17.95) * mm, "end": v(-47.63, 17.05) * mm});
            skLineSegment(sketch, "E353", {"start": v(-47.63, 17.05) * mm, "end": v(-47.63, 17) * mm});
            skLineSegment(sketch, "E354", {"start": v(-47.63, 17) * mm, "end": v(-47.3, 16.23) * mm});
            skLineSegment(sketch, "E355", {"start": v(-47.3, 16.23) * mm, "end": v(-47.15, 15.7) * mm});
            skLineSegment(sketch, "E356", {"start": v(-47.15, 15.7) * mm, "end": v(-46.83, 15.2) * mm});
            skLineSegment(sketch, "E357", {"start": v(-46.83, 15.2) * mm, "end": v(-46.51, 14.67) * mm});
            skLineSegment(sketch, "E358", {"start": v(-46.51, 14.67) * mm, "end": v(-46.06, 14.25) * mm});
            skLineSegment(sketch, "E359", {"start": v(-46.06, 14.25) * mm, "end": v(-45.75, 13.83) * mm});
            skLineSegment(sketch, "E360", {"start": v(-45.75, 13.83) * mm, "end": v(-45.48, 13.64) * mm});
            skLineSegment(sketch, "E361", {"start": v(-45.48, 13.64) * mm, "end": v(-44.66, 13.14) * mm});
            skLineSegment(sketch, "E362", {"start": v(-44.66, 13.14) * mm, "end": v(-44.13, 12.93) * mm});
            skLineSegment(sketch, "E363", {"start": v(-44.13, 12.93) * mm, "end": v(-43.66, 12.66) * mm});
            skLineSegment(sketch, "E364", {"start": v(-43.66, 12.66) * mm, "end": v(-43.07, 12.45) * mm});
            skLineSegment(sketch, "E365", {"start": v(-43.07, 12.45) * mm, "end": v(-42.57, 12.18) * mm});
            skLineSegment(sketch, "E366", {"start": v(-42.57, 12.18) * mm, "end": v(-41.99, 12.08) * mm});
            skLineSegment(sketch, "E367", {"start": v(-41.99, 12.08) * mm, "end": v(-40.11, 11.9) * mm});
            skLineSegment(sketch, "E368", {"start": v(-40.11, 11.9) * mm, "end": v(-39.52, 12) * mm});
            skLineSegment(sketch, "E369", {"start": v(-39.52, 12) * mm, "end": v(-39.03, 12.18) * mm});
            skLineSegment(sketch, "E370", {"start": v(-39.03, 12.18) * mm, "end": v(-38.13, 12.69) * mm});
            skLineSegment(sketch, "E371", {"start": v(-38.13, 12.69) * mm, "end": v(-37.65, 13.27) * mm});
            skLineSegment(sketch, "E372", {"start": v(-37.65, 13.27) * mm, "end": v(-36.8, 14.43) * mm});
            skLineSegment(sketch, "E373", {"start": v(-36.8, 14.43) * mm, "end": v(-36.43, 15.1) * mm});
            skLineSegment(sketch, "E374", {"start": v(-36.43, 15.1) * mm, "end": v(-36.2, 15.86) * mm});
            skLineSegment(sketch, "E375", {"start": v(-36.2, 15.86) * mm, "end": v(-36.09, 16.7) * mm});
            skLineSegment(sketch, "E376", {"start": v(-36.09, 16.7) * mm, "end": v(-36.09, 16.84) * mm});
            skLineSegment(sketch, "E377", {"start": v(-36.09, 16.84) * mm, "end": v(-36.13, 17.75) * mm});
            skLineSegment(sketch, "E378", {"start": v(-36.13, 17.75) * mm, "end": v(-36.35, 18.61) * mm});
            skLineSegment(sketch, "E379", {"start": v(-36.35, 18.61) * mm, "end": v(-36.64, 19.35) * mm});
            skLineSegment(sketch, "E380", {"start": v(-36.64, 19.35) * mm, "end": v(-37.31, 20.26) * mm});
            skLineSegment(sketch, "E381", {"start": v(-37.31, 20.26) * mm, "end": v(-38.23, 20.92) * mm});
            skLineSegment(sketch, "E382", {"start": v(-38.23, 20.92) * mm, "end": v(-39.53, 21.2) * mm});
            skLineSegment(sketch, "E383", {"start": v(-39.53, 21.2) * mm, "end": v(-39.95, 21.18) * mm});
            skLineSegment(sketch, "E384", {"start": v(-39.95, 21.18) * mm, "end": v(-40.8, 21.02) * mm});
            skLineSegment(sketch, "E385", {"start": v(-40.8, 21.02) * mm, "end": v(-41.57, 20.7) * mm});
            skLineSegment(sketch, "E386", {"start": v(-41.57, 20.7) * mm, "end": v(-41.91, 20.33) * mm});
            skLineSegment(sketch, "E387", {"start": v(-41.91, 20.33) * mm, "end": v(-42.2, 19.88) * mm});
            skLineSegment(sketch, "E388", {"start": v(-42.2, 19.88) * mm, "end": v(-42.36, 19.14) * mm});
            skLineSegment(sketch, "E389", {"start": v(-42.36, 19.14) * mm, "end": v(-42.28, 18.76) * mm});
            skLineSegment(sketch, "E390", {"start": v(-42.28, 18.76) * mm, "end": v(-42.04, 18.5) * mm});
            skLineSegment(sketch, "E391", {"start": v(-42.04, 18.5) * mm, "end": v(-41.57, 18.35) * mm});
            skLineSegment(sketch, "E392", {"start": v(-41.57, 18.35) * mm, "end": v(-41.2, 18.46) * mm});
            skLineSegment(sketch, "E393", {"start": v(-41.2, 18.46) * mm, "end": v(-40.9, 18.93) * mm});
            skLineSegment(sketch, "E394", {"start": v(-40.9, 18.93) * mm, "end": v(-40.96, 19.2) * mm});
            skLineSegment(sketch, "E395", {"start": v(-40.96, 19.2) * mm, "end": v(-41.12, 19.51) * mm});
            skLineSegment(sketch, "E396", {"start": v(-41.12, 19.51) * mm, "end": v(-41.14, 19.7) * mm});
            skLineSegment(sketch, "E397", {"start": v(-41.14, 19.7) * mm, "end": v(-41.09, 20.02) * mm});
            skLineSegment(sketch, "E398", {"start": v(-41.09, 20.02) * mm, "end": v(-40.78, 20.37) * mm});
            skLineSegment(sketch, "E399", {"start": v(-40.78, 20.37) * mm, "end": v(-40.35, 20.62) * mm});
            skLineSegment(sketch, "E400", {"start": v(-40.35, 20.62) * mm, "end": v(-39.53, 20.73) * mm});
            skLineSegment(sketch, "E401", {"start": v(-39.53, 20.73) * mm, "end": v(-38.97, 20.7) * mm});
            skLineSegment(sketch, "E402", {"start": v(-38.97, 20.7) * mm, "end": v(-38.55, 20.6) * mm});
            skLineSegment(sketch, "E403", {"start": v(-38.55, 20.6) * mm, "end": v(-38.17, 20.26) * mm});
            skLineSegment(sketch, "E404", {"start": v(-38.17, 20.26) * mm, "end": v(-37.94, 19.75) * mm});
            skLineSegment(sketch, "E405", {"start": v(-37.94, 19.75) * mm, "end": v(-37.84, 19.14) * mm});
            skLineSegment(sketch, "E406", {"start": v(-37.84, 19.14) * mm, "end": v(-37.65, 18.48) * mm});
            skLineSegment(sketch, "E407", {"start": v(-37.65, 18.48) * mm, "end": v(-37.62, 17.85) * mm});
            skLineSegment(sketch, "E408", {"start": v(-37.62, 17.85) * mm, "end": v(-37.76, 16.27) * mm});
            skLineSegment(sketch, "E409", {"start": v(-37.76, 16.27) * mm, "end": v(-38.13, 14.96) * mm});
            skLineSegment(sketch, "E410", {"start": v(-38.13, 14.96) * mm, "end": v(-38.4, 14.51) * mm});
            skLineSegment(sketch, "E411", {"start": v(-38.4, 14.51) * mm, "end": v(-38.6, 14.04) * mm});
            skLineSegment(sketch, "E412", {"start": v(-38.6, 14.04) * mm, "end": v(-38.9, 13.75) * mm});
            skLineSegment(sketch, "E413", {"start": v(-38.9, 13.75) * mm, "end": v(-39.33, 13.45) * mm});
            skLineSegment(sketch, "E414", {"start": v(-39.33, 13.45) * mm, "end": v(-39.85, 13.24) * mm});
            skLineSegment(sketch, "E415", {"start": v(-39.85, 13.24) * mm, "end": v(-40.48, 13.03) * mm});
            skLineSegment(sketch, "E416", {"start": v(-40.48, 13.03) * mm, "end": v(-40.64, 13.03) * mm});
            skLineSegment(sketch, "E417", {"start": v(-40.64, 13.03) * mm, "end": v(-41.01, 13.06) * mm});
            skLineSegment(sketch, "E418", {"start": v(-41.01, 13.06) * mm, "end": v(-41.54, 13.08) * mm});
            skLineSegment(sketch, "E419", {"start": v(-41.54, 13.08) * mm, "end": v(-42.04, 13.1) * mm});
            skLineSegment(sketch, "E420", {"start": v(-42.04, 13.1) * mm, "end": v(-42.5, 13.24) * mm});
            skLineSegment(sketch, "E421", {"start": v(-42.5, 13.24) * mm, "end": v(-43.18, 13.42) * mm});
            skLineSegment(sketch, "E422", {"start": v(-43.18, 13.42) * mm, "end": v(-43.73, 13.7) * mm});
            skLineSegment(sketch, "E423", {"start": v(-43.73, 13.7) * mm, "end": v(-44.1, 13.88) * mm});
            skLineSegment(sketch, "E424", {"start": v(-44.1, 13.88) * mm, "end": v(-44.71, 14.38) * mm});
            skLineSegment(sketch, "E425", {"start": v(-44.71, 14.38) * mm, "end": v(-45.03, 14.65) * mm});
            skLineSegment(sketch, "E426", {"start": v(-45.03, 14.65) * mm, "end": v(-45.88, 15.55) * mm});
            skLineSegment(sketch, "E427", {"start": v(-45.88, 15.55) * mm, "end": v(-46.25, 16.31) * mm});
            skLineSegment(sketch, "E428", {"start": v(-46.25, 16.31) * mm, "end": v(-46.54, 17.13) * mm});
            skLineSegment(sketch, "E429", {"start": v(-46.54, 17.13) * mm, "end": v(-46.75, 18.88) * mm});
            skLineSegment(sketch, "E430", {"start": v(-46.75, 18.88) * mm, "end": v(-46.57, 20.12) * mm});
            skLineSegment(sketch, "E431", {"start": v(-46.57, 20.12) * mm, "end": v(-46.2, 20.85) * mm});
            skLineSegment(sketch, "E432", {"start": v(-46.2, 20.85) * mm, "end": v(-45.77, 21.58) * mm});
            skLineSegment(sketch, "E433", {"start": v(-45.77, 21.58) * mm, "end": v(-45.09, 22.56) * mm});
            skLineSegment(sketch, "E434", {"start": v(-45.09, 22.56) * mm, "end": v(-44.8, 23) * mm});
            skLineSegment(sketch, "E435", {"start": v(-44.8, 23) * mm, "end": v(-44.34, 23.45) * mm});
            skLineSegment(sketch, "E436", {"start": v(-44.34, 23.45) * mm, "end": v(-43.66, 23.93) * mm});
            skLineSegment(sketch, "E437", {"start": v(-43.66, 23.93) * mm, "end": v(-43.2, 24.28) * mm});
            skLineSegment(sketch, "E438", {"start": v(-43.2, 24.28) * mm, "end": v(-42.78, 24.46) * mm});
            skLineSegment(sketch, "E439", {"start": v(-42.78, 24.46) * mm, "end": v(-42.3, 24.73) * mm});
            skLineSegment(sketch, "E440", {"start": v(-42.3, 24.73) * mm, "end": v(-41.62, 25) * mm});
            skLineSegment(sketch, "E441", {"start": v(-41.62, 25) * mm, "end": v(-40.7, 25.25) * mm});
            skLineSegment(sketch, "E442", {"start": v(-40.7, 25.25) * mm, "end": v(-40.24, 25.41) * mm});
            skLineSegment(sketch, "E443", {"start": v(-40.24, 25.41) * mm, "end": v(-39.74, 25.47) * mm});
            skLineSegment(sketch, "E444", {"start": v(-39.74, 25.47) * mm, "end": v(-39.26, 25.57) * mm});
            skLineSegment(sketch, "E445", {"start": v(-39.26, 25.57) * mm, "end": v(-38.18, 25.7) * mm});
            skLineSegment(sketch, "E446", {"start": v(-38.18, 25.7) * mm, "end": v(-37.57, 25.73) * mm});
            skLineSegment(sketch, "E447", {"start": v(-37.57, 25.73) * mm, "end": v(-36.12, 25.63) * mm});
            skLineSegment(sketch, "E448", {"start": v(-36.12, 25.63) * mm, "end": v(-36, 25.63) * mm});
            skLineSegment(sketch, "E449", {"start": v(-36, 25.63) * mm, "end": v(-34.45, 25.44) * mm});
            skLineSegment(sketch, "E450", {"start": v(-34.45, 25.44) * mm, "end": v(-33.97, 25.28) * mm});
            skLineSegment(sketch, "E451", {"start": v(-33.97, 25.28) * mm, "end": v(-32.7, 25.12) * mm});
            skLineSegment(sketch, "E452", {"start": v(-32.7, 25.12) * mm, "end": v(-32.07, 25.02) * mm});
            skLineSegment(sketch, "E453", {"start": v(-32.07, 25.02) * mm, "end": v(-31.75, 25) * mm});
            skLineSegment(sketch, "E454", {"start": v(-31.75, 25) * mm, "end": v(-31.4, 25) * mm});
            skLineSegment(sketch, "E455", {"start": v(-31.4, 25) * mm, "end": v(-30.98, 24.86) * mm});
            skLineSegment(sketch, "E456", {"start": v(-30.98, 24.86) * mm, "end": v(-29.53, 24.65) * mm});
            skLineSegment(sketch, "E457", {"start": v(-29.53, 24.65) * mm, "end": v(-29.5, 23.88) * mm});
            skLineSegment(sketch, "E458", {"start": v(-29.5, 23.88) * mm, "end": v(-29.53, 22.4) * mm});
            skLineSegment(sketch, "E459", {"start": v(-29.53, 22.4) * mm, "end": v(-29.53, 20.15) * mm});
            skLineSegment(sketch, "E460", {"start": v(-29.53, 20.15) * mm, "end": v(-29.55, 19.01) * mm});
            skLineSegment(sketch, "E461", {"start": v(-29.55, 19.01) * mm, "end": v(-29.55, 17.71) * mm});
            skLineSegment(sketch, "E462", {"start": v(-29.55, 17.71) * mm, "end": v(-29.58, 16.81) * mm});
            skLineSegment(sketch, "E463", {"start": v(-29.58, 16.81) * mm, "end": v(-29.58, 16.6) * mm});
            skLineSegment(sketch, "E464", {"start": v(-29.58, 16.6) * mm, "end": v(-29.53, 15.47) * mm});
            skLineSegment(sketch, "E465", {"start": v(-29.53, 15.47) * mm, "end": v(-29.47, 13.2) * mm});
            skLineSegment(sketch, "E466", {"start": v(-29.47, 13.2) * mm, "end": v(-29.47, 11.02) * mm});
            skLineSegment(sketch, "E467", {"start": v(-29.47, 11.02) * mm, "end": v(-29.45, 9.78) * mm});
            skLineSegment(sketch, "E468", {"start": v(-29.45, 9.78) * mm, "end": v(-29.47, 8.64) * mm});
            skLineSegment(sketch, "E469", {"start": v(-29.47, 8.64) * mm, "end": v(-29.47, 6.6) * mm});
            skLineSegment(sketch, "E470", {"start": v(-29.47, 6.6) * mm, "end": v(-29.53, 6.31) * mm});
            skLineSegment(sketch, "E471", {"start": v(-29.53, 6.31) * mm, "end": v(-30.19, 6.24) * mm});
            skLineSegment(sketch, "E472", {"start": v(-30.19, 6.24) * mm, "end": v(-30.74, 6.05) * mm});
            skLineSegment(sketch, "E473", {"start": v(-30.74, 6.05) * mm, "end": v(-30.9, 5.89) * mm});
            skLineSegment(sketch, "E474", {"start": v(-30.9, 5.89) * mm, "end": v(-30.96, 5.86) * mm});
            skLineSegment(sketch, "E475", {"start": v(-30.96, 5.86) * mm, "end": v(-30.98, 5.86) * mm});
            skLineSegment(sketch, "E476", {"start": v(-30.98, 5.86) * mm, "end": v(-31.14, 5.6) * mm});
            skLineSegment(sketch, "E477", {"start": v(-31.14, 5.6) * mm, "end": v(-31.02, 5.38) * mm});
            skLineSegment(sketch, "E478", {"start": v(-31.02, 5.38) * mm, "end": v(-30.7, 5.28) * mm});
            skLineSegment(sketch, "E479", {"start": v(-30.7, 5.28) * mm, "end": v(-30.64, 5.28) * mm});
            skLineSegment(sketch, "E480", {"start": v(-30.64, 5.28) * mm, "end": v(-29.98, 5.44) * mm});
            skLineSegment(sketch, "E481", {"start": v(-29.98, 5.44) * mm, "end": v(-29.82, 5.44) * mm});
            skLineSegment(sketch, "E482", {"start": v(-29.82, 5.44) * mm, "end": v(-29.24, 5.41) * mm});
            skLineSegment(sketch, "E483", {"start": v(-29.24, 5.41) * mm, "end": v(-29.13, 5.41) * mm});
            skLineSegment(sketch, "E484", {"start": v(-29.13, 5.41) * mm, "end": v(-28.81, 5.46) * mm});
            skLineSegment(sketch, "E485", {"start": v(-28.81, 5.46) * mm, "end": v(-28.5, 5.44) * mm});
            skLineSegment(sketch, "E486", {"start": v(-28.5, 5.44) * mm, "end": v(-28.18, 5.5) * mm});
            skLineSegment(sketch, "E487", {"start": v(-28.18, 5.5) * mm, "end": v(-28, 5.44) * mm});
            skLineSegment(sketch, "E488", {"start": v(-28, 5.44) * mm, "end": v(-27.76, 5.44) * mm});
            skLineSegment(sketch, "E489", {"start": v(-27.76, 5.44) * mm, "end": v(-27.3, 5.33) * mm});
            skLineSegment(sketch, "E490", {"start": v(-27.3, 5.33) * mm, "end": v(-27.15, 5.3) * mm});
            skLineSegment(sketch, "E491", {"start": v(-27.15, 5.3) * mm, "end": v(-26.86, 5.41) * mm});
            skLineSegment(sketch, "E492", {"start": v(-26.86, 5.41) * mm, "end": v(-26.72, 5.68) * mm});
            skLineSegment(sketch, "E493", {"start": v(-26.72, 5.68) * mm, "end": v(-26.72, 5.8) * mm});
            skLineSegment(sketch, "E494", {"start": v(-26.72, 5.8) * mm, "end": v(-27, 6.06) * mm});
            skLineSegment(sketch, "E495", {"start": v(-27, 6.06) * mm, "end": v(-27.46, 6.12) * mm});
            skLineSegment(sketch, "E496", {"start": v(-27.46, 6.12) * mm, "end": v(-27.46, 6.23) * mm});
            skLineSegment(sketch, "E497", {"start": v(-27.46, 6.23) * mm, "end": v(-27.56, 6.59) * mm});
            skLineSegment(sketch, "E498", {"start": v(-27.56, 6.59) * mm, "end": v(-27.68, 6.87) * mm});
            skLineSegment(sketch, "E499", {"start": v(-27.68, 6.87) * mm, "end": v(-27.7, 7.08) * mm});
            skLineSegment(sketch, "E500", {"start": v(-27.7, 7.08) * mm, "end": v(-27.68, 7.58) * mm});
            skLineSegment(sketch, "E501", {"start": v(-27.68, 7.58) * mm, "end": v(-27.68, 8.32) * mm});
            skLineSegment(sketch, "E502", {"start": v(-27.68, 8.32) * mm, "end": v(-27.73, 9.8) * mm});
            skLineSegment(sketch, "E503", {"start": v(-27.73, 9.8) * mm, "end": v(-27.7, 11.26) * mm});
            skLineSegment(sketch, "E504", {"start": v(-27.7, 11.26) * mm, "end": v(-27.73, 12.47) * mm});
            skLineSegment(sketch, "E505", {"start": v(-27.73, 12.47) * mm, "end": v(-27.73, 12.77) * mm});
            skLineSegment(sketch, "E506", {"start": v(-27.73, 12.77) * mm, "end": v(-27.62, 13.75) * mm});
            skLineSegment(sketch, "E507", {"start": v(-27.62, 13.75) * mm, "end": v(-27.62, 14.1) * mm});
            skLineSegment(sketch, "E508", {"start": v(-27.62, 14.1) * mm, "end": v(-27.65, 15.41) * mm});
            skLineSegment(sketch, "E509", {"start": v(-27.65, 15.41) * mm, "end": v(-27.65, 15.7) * mm});
            skLineSegment(sketch, "E510", {"start": v(-27.65, 15.7) * mm, "end": v(-27.62, 16.44) * mm});
            skLineSegment(sketch, "E511", {"start": v(-27.62, 16.44) * mm, "end": v(-27.62, 16.74) * mm});
            skLineSegment(sketch, "E512", {"start": v(-27.62, 16.74) * mm, "end": v(-27.73, 17.1) * mm});
            skLineSegment(sketch, "E513", {"start": v(-27.73, 17.1) * mm, "end": v(-27.73, 17.45) * mm});
            skLineSegment(sketch, "E514", {"start": v(-27.73, 17.45) * mm, "end": v(-27.68, 18.75) * mm});
            skLineSegment(sketch, "E515", {"start": v(-27.68, 18.75) * mm, "end": v(-27.68, 18.96) * mm});
            skLineSegment(sketch, "E516", {"start": v(-27.68, 18.96) * mm, "end": v(-27.73, 20.36) * mm});
            skLineSegment(sketch, "E517", {"start": v(-27.73, 20.36) * mm, "end": v(-27.73, 21.44) * mm});
            skLineSegment(sketch, "E518", {"start": v(-27.73, 21.44) * mm, "end": v(-27.7, 22.34) * mm});
            skLineSegment(sketch, "E519", {"start": v(-27.7, 22.34) * mm, "end": v(-27.7, 22.95) * mm});
            skLineSegment(sketch, "E520", {"start": v(-27.7, 22.95) * mm, "end": v(-27.6, 24.12) * mm});
            skLineSegment(sketch, "E521", {"start": v(-27.6, 24.12) * mm, "end": v(-26.99, 24.17) * mm});
            skLineSegment(sketch, "E522", {"start": v(-26.99, 24.17) * mm, "end": v(-25.3, 24.04) * mm});
            skLineSegment(sketch, "E523", {"start": v(-25.3, 24.04) * mm, "end": v(-24.84, 24.04) * mm});
            skLineSegment(sketch, "E524", {"start": v(-24.84, 24.04) * mm, "end": v(-22.94, 24.2) * mm});
            skLineSegment(sketch, "E525", {"start": v(-22.94, 24.2) * mm, "end": v(-21.62, 24.54) * mm});
            skLineSegment(sketch, "E526", {"start": v(-21.62, 24.54) * mm, "end": v(-21.14, 24.8) * mm});
            skLineSegment(sketch, "E527", {"start": v(-21.14, 24.8) * mm, "end": v(-20.69, 25.1) * mm});
            skLineSegment(sketch, "E528", {"start": v(-20.69, 25.1) * mm, "end": v(-20.16, 25.57) * mm});
            skLineSegment(sketch, "E529", {"start": v(-20.16, 25.57) * mm, "end": v(-19.87, 26.2) * mm});
            skLineSegment(sketch, "E530", {"start": v(-19.87, 26.2) * mm, "end": v(-19.87, 26.23) * mm});
            skLineSegment(sketch, "E531", {"start": v(-19.87, 26.23) * mm, "end": v(-19.76, 26.7) * mm});
            skLineSegment(sketch, "E532", {"start": v(-19.76, 26.7) * mm, "end": v(-19.82, 27) * mm});
            skLineSegment(sketch, "E533", {"start": v(-19.82, 27) * mm, "end": v(-20.2, 27.34) * mm});
            skLineSegment(sketch, "E534", {"start": v(-20.2, 27.34) * mm, "end": v(-20.66, 27.5) * mm});
            skLineSegment(sketch, "E535", {"start": v(-20.66, 27.5) * mm, "end": v(-20.95, 27.5) * mm});
            skLineSegment(sketch, "E536", {"start": v(-23.3, 18.2) * mm, "end": v(-23.07, 18.22) * mm});
            skLineSegment(sketch, "E537", {"start": v(-23.07, 18.22) * mm, "end": v(-22.91, 18.16) * mm});
            skLineSegment(sketch, "E538", {"start": v(-22.91, 18.16) * mm, "end": v(-22.96, 16.95) * mm});
            skLineSegment(sketch, "E539", {"start": v(-22.96, 16.95) * mm, "end": v(-22.89, 16.34) * mm});
            skLineSegment(sketch, "E540", {"start": v(-22.89, 16.34) * mm, "end": v(-22.94, 15.28) * mm});
            skLineSegment(sketch, "E541", {"start": v(-22.94, 15.28) * mm, "end": v(-22.94, 14.22) * mm});
            skLineSegment(sketch, "E542", {"start": v(-22.94, 14.22) * mm, "end": v(-23.07, 14.2) * mm});
            skLineSegment(sketch, "E543", {"start": v(-23.07, 14.2) * mm, "end": v(-23.26, 14.25) * mm});
            skLineSegment(sketch, "E544", {"start": v(-23.26, 14.25) * mm, "end": v(-23.47, 14.38) * mm});
            skLineSegment(sketch, "E545", {"start": v(-23.47, 14.38) * mm, "end": v(-23.9, 14.7) * mm});
            skLineSegment(sketch, "E546", {"start": v(-23.9, 14.7) * mm, "end": v(-24.1, 14.96) * mm});
            skLineSegment(sketch, "E547", {"start": v(-24.1, 14.96) * mm, "end": v(-24.24, 15.15) * mm});
            skLineSegment(sketch, "E548", {"start": v(-24.24, 15.15) * mm, "end": v(-24.32, 15.2) * mm});
            skLineSegment(sketch, "E549", {"start": v(-24.32, 15.2) * mm, "end": v(-24.42, 15.57) * mm});
            skLineSegment(sketch, "E550", {"start": v(-24.42, 15.57) * mm, "end": v(-24.45, 15.62) * mm});
            skLineSegment(sketch, "E551", {"start": v(-24.45, 15.62) * mm, "end": v(-24.53, 16.23) * mm});
            skLineSegment(sketch, "E552", {"start": v(-24.53, 16.23) * mm, "end": v(-24.53, 16.4) * mm});
            skLineSegment(sketch, "E553", {"start": v(-24.53, 16.4) * mm, "end": v(-24.34, 17.27) * mm});
            skLineSegment(sketch, "E554", {"start": v(-24.34, 17.27) * mm, "end": v(-24.16, 17.58) * mm});
            skLineSegment(sketch, "E555", {"start": v(-24.16, 17.58) * mm, "end": v(-23.94, 17.69) * mm});
            skLineSegment(sketch, "E556", {"start": v(-23.94, 17.69) * mm, "end": v(-23.7, 17.93) * mm});
            skLineSegment(sketch, "E557", {"start": v(-23.7, 17.93) * mm, "end": v(-23.63, 17.98) * mm});
            skLineSegment(sketch, "E558", {"start": v(-23.63, 17.98) * mm, "end": v(-23.39, 18.06) * mm});
            skLineSegment(sketch, "E559", {"start": v(-23.39, 18.06) * mm, "end": v(-23.39, 18.11) * mm});
            skLineSegment(sketch, "E560", {"start": v(-23.39, 18.11) * mm, "end": v(-23.39, 18.08) * mm});
            skLineSegment(sketch, "E561", {"start": v(-23.39, 18.08) * mm, "end": v(-23.3, 18.08) * mm});
            skLineSegment(sketch, "E562", {"start": v(-23.3, 18.08) * mm, "end": v(-23.3, 18.2) * mm});
            skLineSegment(sketch, "E563", {"start": v(-18.3, 22.63) * mm, "end": v(-18.33, 22.5) * mm});
            skLineSegment(sketch, "E564", {"start": v(-18.33, 22.5) * mm, "end": v(-18.2, 22.3) * mm});
            skLineSegment(sketch, "E565", {"start": v(-18.2, 22.3) * mm, "end": v(-17.89, 22.21) * mm});
            skLineSegment(sketch, "E566", {"start": v(-17.89, 22.21) * mm, "end": v(-17.83, 22.21) * mm});
            skLineSegment(sketch, "E567", {"start": v(-17.83, 22.21) * mm, "end": v(-17.47, 22.15) * mm});
            skLineSegment(sketch, "E568", {"start": v(-17.47, 22.15) * mm, "end": v(-17.25, 22.03) * mm});
            skLineSegment(sketch, "E569", {"start": v(-17.25, 22.03) * mm, "end": v(-17.2, 19.83) * mm});
            skLineSegment(sketch, "E570", {"start": v(-17.2, 19.83) * mm, "end": v(-17.2, 19.4) * mm});
            skLineSegment(sketch, "E571", {"start": v(-17.2, 19.4) * mm, "end": v(-17.17, 18.4) * mm});
            skLineSegment(sketch, "E572", {"start": v(-17.17, 18.4) * mm, "end": v(-17.2, 17.45) * mm});
            skLineSegment(sketch, "E573", {"start": v(-17.2, 17.45) * mm, "end": v(-17.17, 16.7) * mm});
            skLineSegment(sketch, "E574", {"start": v(-17.17, 16.7) * mm, "end": v(-17.2, 15.91) * mm});
            skLineSegment(sketch, "E575", {"start": v(-17.2, 15.91) * mm, "end": v(-17.25, 15.1) * mm});
            skLineSegment(sketch, "E576", {"start": v(-17.25, 15.1) * mm, "end": v(-18.36, 14.99) * mm});
            skLineSegment(sketch, "E577", {"start": v(-18.36, 14.99) * mm, "end": v(-19, 14.88) * mm});
            skLineSegment(sketch, "E578", {"start": v(-19, 14.88) * mm, "end": v(-19.6, 14.72) * mm});
            skLineSegment(sketch, "E579", {"start": v(-19.6, 14.72) * mm, "end": v(-20.08, 14.49) * mm});
            skLineSegment(sketch, "E580", {"start": v(-20.08, 14.49) * mm, "end": v(-20.61, 14.27) * mm});
            skLineSegment(sketch, "E581", {"start": v(-20.61, 14.27) * mm, "end": v(-21.7, 14.04) * mm});
            skLineSegment(sketch, "E582", {"start": v(-21.7, 14.04) * mm, "end": v(-21.67, 14.3) * mm});
            skLineSegment(sketch, "E583", {"start": v(-21.67, 14.3) * mm, "end": v(-21.7, 14.6) * mm});
            skLineSegment(sketch, "E584", {"start": v(-21.7, 14.6) * mm, "end": v(-21.75, 16.1) * mm});
            skLineSegment(sketch, "E585", {"start": v(-21.75, 16.1) * mm, "end": v(-21.7, 17.58) * mm});
            skLineSegment(sketch, "E586", {"start": v(-21.7, 17.58) * mm, "end": v(-21.43, 17.27) * mm});
            skLineSegment(sketch, "E587", {"start": v(-21.43, 17.27) * mm, "end": v(-21.14, 16.68) * mm});
            skLineSegment(sketch, "E588", {"start": v(-21.14, 16.68) * mm, "end": v(-21.06, 15.86) * mm});
            skLineSegment(sketch, "E589", {"start": v(-21.06, 15.86) * mm, "end": v(-21.09, 15.55) * mm});
            skLineSegment(sketch, "E590", {"start": v(-21.09, 15.55) * mm, "end": v(-20.87, 15.18) * mm});
            skLineSegment(sketch, "E591", {"start": v(-20.87, 15.18) * mm, "end": v(-20.45, 15.02) * mm});
            skLineSegment(sketch, "E592", {"start": v(-20.45, 15.02) * mm, "end": v(-20.32, 15.04) * mm});
            skLineSegment(sketch, "E593", {"start": v(-20.32, 15.04) * mm, "end": v(-20.08, 15.12) * mm});
            skLineSegment(sketch, "E594", {"start": v(-20.08, 15.12) * mm, "end": v(-19.9, 15.28) * mm});
            skLineSegment(sketch, "E595", {"start": v(-19.9, 15.28) * mm, "end": v(-19.82, 15.8) * mm});
            skLineSegment(sketch, "E596", {"start": v(-19.82, 15.8) * mm, "end": v(-19.84, 16.1) * mm});
            skLineSegment(sketch, "E597", {"start": v(-19.84, 16.1) * mm, "end": v(-19.9, 16.26) * mm});
            skLineSegment(sketch, "E598", {"start": v(-19.9, 16.26) * mm, "end": v(-19.95, 16.44) * mm});
            skLineSegment(sketch, "E599", {"start": v(-19.95, 16.44) * mm, "end": v(-20.03, 16.6) * mm});
            skLineSegment(sketch, "E600", {"start": v(-20.03, 16.6) * mm, "end": v(-20.1, 16.87) * mm});
            skLineSegment(sketch, "E601", {"start": v(-20.1, 16.87) * mm, "end": v(-20.19, 16.97) * mm});
            skLineSegment(sketch, "E602", {"start": v(-20.19, 16.97) * mm, "end": v(-20.24, 17.13) * mm});
            skLineSegment(sketch, "E603", {"start": v(-20.24, 17.13) * mm, "end": v(-20.64, 17.56) * mm});
            skLineSegment(sketch, "E604", {"start": v(-20.64, 17.56) * mm, "end": v(-21.27, 18.06) * mm});
            skLineSegment(sketch, "E605", {"start": v(-21.27, 18.06) * mm, "end": v(-21.72, 18.32) * mm});
            skLineSegment(sketch, "E606", {"start": v(-21.72, 18.32) * mm, "end": v(-21.72, 18.5) * mm});
            skLineSegment(sketch, "E607", {"start": v(-21.72, 18.5) * mm, "end": v(-21.7, 19.35) * mm});
            skLineSegment(sketch, "E608", {"start": v(-21.7, 19.35) * mm, "end": v(-21.72, 20.07) * mm});
            skLineSegment(sketch, "E609", {"start": v(-21.72, 20.07) * mm, "end": v(-21.72, 20.25) * mm});
            skLineSegment(sketch, "E610", {"start": v(-21.72, 20.25) * mm, "end": v(-21.67, 20.47) * mm});
            skLineSegment(sketch, "E611", {"start": v(-21.67, 20.47) * mm, "end": v(-21.67, 20.68) * mm});
            skLineSegment(sketch, "E612", {"start": v(-21.67, 20.68) * mm, "end": v(-21.62, 21.18) * mm});
            skLineSegment(sketch, "E613", {"start": v(-21.62, 21.18) * mm, "end": v(-21.62, 21.55) * mm});
            skLineSegment(sketch, "E614", {"start": v(-21.62, 21.55) * mm, "end": v(-21.59, 21.7) * mm});
            skLineSegment(sketch, "E615", {"start": v(-21.59, 21.7) * mm, "end": v(-21.44, 21.87) * mm});
            skLineSegment(sketch, "E616", {"start": v(-21.44, 21.87) * mm, "end": v(-21.2, 21.97) * mm});
            skLineSegment(sketch, "E617", {"start": v(-21.2, 21.97) * mm, "end": v(-20.88, 21.97) * mm});
            skLineSegment(sketch, "E618", {"start": v(-20.88, 21.97) * mm, "end": v(-20.69, 22.24) * mm});
            skLineSegment(sketch, "E619", {"start": v(-20.69, 22.24) * mm, "end": v(-20.69, 22.3) * mm});
            skLineSegment(sketch, "E620", {"start": v(-20.69, 22.3) * mm, "end": v(-20.95, 22.45) * mm});
            skLineSegment(sketch, "E621", {"start": v(-20.95, 22.45) * mm, "end": v(-21.46, 22.32) * mm});
            skLineSegment(sketch, "E622", {"start": v(-21.46, 22.32) * mm, "end": v(-21.93, 22.4) * mm});
            skLineSegment(sketch, "E623", {"start": v(-21.93, 22.4) * mm, "end": v(-23.02, 22.24) * mm});
            skLineSegment(sketch, "E624", {"start": v(-23.02, 22.24) * mm, "end": v(-23.6, 22.24) * mm});
            skLineSegment(sketch, "E625", {"start": v(-23.6, 22.24) * mm, "end": v(-24, 22.19) * mm});
            skLineSegment(sketch, "E626", {"start": v(-24, 22.19) * mm, "end": v(-24.02, 22.08) * mm});
            skLineSegment(sketch, "E627", {"start": v(-24.02, 22.08) * mm, "end": v(-23.9, 21.9) * mm});
            skLineSegment(sketch, "E628", {"start": v(-23.9, 21.9) * mm, "end": v(-23.57, 21.87) * mm});
            skLineSegment(sketch, "E629", {"start": v(-23.57, 21.87) * mm, "end": v(-23.34, 21.87) * mm});
            skLineSegment(sketch, "E630", {"start": v(-23.34, 21.87) * mm, "end": v(-23.1, 21.84) * mm});
            skLineSegment(sketch, "E631", {"start": v(-23.1, 21.84) * mm, "end": v(-23.02, 21.52) * mm});
            skLineSegment(sketch, "E632", {"start": v(-23.02, 21.52) * mm, "end": v(-23.07, 20.97) * mm});
            skLineSegment(sketch, "E633", {"start": v(-23.07, 20.97) * mm, "end": v(-23.07, 20.89) * mm});
            skLineSegment(sketch, "E634", {"start": v(-23.07, 20.89) * mm, "end": v(-23.02, 20.36) * mm});
            skLineSegment(sketch, "E635", {"start": v(-23.02, 20.36) * mm, "end": v(-23.04, 20.12) * mm});
            skLineSegment(sketch, "E636", {"start": v(-23.04, 20.12) * mm, "end": v(-23, 19.57) * mm});
            skLineSegment(sketch, "E637", {"start": v(-23, 19.57) * mm, "end": v(-23.02, 18.7) * mm});
            skLineSegment(sketch, "E638", {"start": v(-23.02, 18.7) * mm, "end": v(-23.6, 18.65) * mm});
            skLineSegment(sketch, "E639", {"start": v(-23.6, 18.65) * mm, "end": v(-24, 18.48) * mm});
            skLineSegment(sketch, "E640", {"start": v(-24, 18.48) * mm, "end": v(-24.68, 18.22) * mm});
            skLineSegment(sketch, "E641", {"start": v(-24.68, 18.22) * mm, "end": v(-25.21, 17.56) * mm});
            skLineSegment(sketch, "E642", {"start": v(-25.21, 17.56) * mm, "end": v(-25.21, 17.5) * mm});
            skLineSegment(sketch, "E643", {"start": v(-25.21, 17.5) * mm, "end": v(-25.3, 17.3) * mm});
            skLineSegment(sketch, "E644", {"start": v(-25.3, 17.3) * mm, "end": v(-25.35, 16.9) * mm});
            skLineSegment(sketch, "E645", {"start": v(-25.35, 16.9) * mm, "end": v(-25.4, 16.52) * mm});
            skLineSegment(sketch, "E646", {"start": v(-25.4, 16.52) * mm, "end": v(-25.48, 15.86) * mm});
            skLineSegment(sketch, "E647", {"start": v(-25.48, 15.86) * mm, "end": v(-25.48, 15.73) * mm});
            skLineSegment(sketch, "E648", {"start": v(-25.48, 15.73) * mm, "end": v(-25.43, 15.41) * mm});
            skLineSegment(sketch, "E649", {"start": v(-25.43, 15.41) * mm, "end": v(-25.31, 14.9) * mm});
            skLineSegment(sketch, "E650", {"start": v(-25.31, 14.9) * mm, "end": v(-25.14, 14.49) * mm});
            skLineSegment(sketch, "E651", {"start": v(-25.14, 14.49) * mm, "end": v(-24.55, 13.93) * mm});
            skLineSegment(sketch, "E652", {"start": v(-24.55, 13.93) * mm, "end": v(-23.55, 13.4) * mm});
            skLineSegment(sketch, "E653", {"start": v(-23.55, 13.4) * mm, "end": v(-23.27, 13.28) * mm});
            skLineSegment(sketch, "E654", {"start": v(-23.27, 13.28) * mm, "end": v(-23.07, 13.1) * mm});
            skLineSegment(sketch, "E655", {"start": v(-23.07, 13.1) * mm, "end": v(-23.04, 12.8) * mm});
            skLineSegment(sketch, "E656", {"start": v(-23.04, 12.8) * mm, "end": v(-23.04, 12.4) * mm});
            skLineSegment(sketch, "E657", {"start": v(-23.04, 12.4) * mm, "end": v(-23.07, 11.4) * mm});
            skLineSegment(sketch, "E658", {"start": v(-23.07, 11.4) * mm, "end": v(-23.04, 10.12) * mm});
            skLineSegment(sketch, "E659", {"start": v(-23.04, 10.12) * mm, "end": v(-23.12, 6.23) * mm});
            skLineSegment(sketch, "E660", {"start": v(-23.12, 6.23) * mm, "end": v(-23.34, 6.16) * mm});
            skLineSegment(sketch, "E661", {"start": v(-23.34, 6.16) * mm, "end": v(-23.65, 6.13) * mm});
            skLineSegment(sketch, "E662", {"start": v(-23.65, 6.13) * mm, "end": v(-23.94, 6.08) * mm});
            skLineSegment(sketch, "E663", {"start": v(-23.94, 6.08) * mm, "end": v(-24.08, 5.94) * mm});
            skLineSegment(sketch, "E664", {"start": v(-24.08, 5.94) * mm, "end": v(-24.08, 5.91) * mm});
            skLineSegment(sketch, "E665", {"start": v(-24.08, 5.91) * mm, "end": v(-23.86, 5.73) * mm});
            skLineSegment(sketch, "E666", {"start": v(-23.86, 5.73) * mm, "end": v(-23.42, 5.68) * mm});
            skLineSegment(sketch, "E667", {"start": v(-23.42, 5.68) * mm, "end": v(-22.78, 5.68) * mm});
            skLineSegment(sketch, "E668", {"start": v(-22.78, 5.68) * mm, "end": v(-22.46, 5.76) * mm});
            skLineSegment(sketch, "E669", {"start": v(-22.46, 5.76) * mm, "end": v(-22.33, 5.76) * mm});
            skLineSegment(sketch, "E670", {"start": v(-22.33, 5.76) * mm, "end": v(-21.48, 5.68) * mm});
            skLineSegment(sketch, "E671", {"start": v(-21.48, 5.68) * mm, "end": v(-21.11, 5.65) * mm});
            skLineSegment(sketch, "E672", {"start": v(-21.11, 5.65) * mm, "end": v(-20.72, 5.6) * mm});
            skLineSegment(sketch, "E673", {"start": v(-20.72, 5.6) * mm, "end": v(-20.5, 5.76) * mm});
            skLineSegment(sketch, "E674", {"start": v(-20.5, 5.76) * mm, "end": v(-20.5, 5.78) * mm});
            skLineSegment(sketch, "E675", {"start": v(-20.5, 5.78) * mm, "end": v(-20.65, 5.94) * mm});
            skLineSegment(sketch, "E676", {"start": v(-20.65, 5.94) * mm, "end": v(-20.93, 6.05) * mm});
            skLineSegment(sketch, "E677", {"start": v(-20.93, 6.05) * mm, "end": v(-20.98, 6.07) * mm});
            skLineSegment(sketch, "E678", {"start": v(-20.98, 6.07) * mm, "end": v(-21.5, 6.31) * mm});
            skLineSegment(sketch, "E679", {"start": v(-21.5, 6.31) * mm, "end": v(-21.59, 6.52) * mm});
            skLineSegment(sketch, "E680", {"start": v(-21.59, 6.52) * mm, "end": v(-21.59, 8.27) * mm});
            skLineSegment(sketch, "E681", {"start": v(-21.59, 8.27) * mm, "end": v(-21.7, 9.22) * mm});
            skLineSegment(sketch, "E682", {"start": v(-21.7, 9.22) * mm, "end": v(-21.72, 9.43) * mm});
            skLineSegment(sketch, "E683", {"start": v(-21.72, 9.43) * mm, "end": v(-21.72, 9.64) * mm});
            skLineSegment(sketch, "E684", {"start": v(-21.72, 9.64) * mm, "end": v(-21.75, 10.44) * mm});
            skLineSegment(sketch, "E685", {"start": v(-21.75, 10.44) * mm, "end": v(-21.72, 10.75) * mm});
            skLineSegment(sketch, "E686", {"start": v(-21.72, 10.75) * mm, "end": v(-21.77, 11.2) * mm});
            skLineSegment(sketch, "E687", {"start": v(-21.77, 11.2) * mm, "end": v(-21.72, 11.87) * mm});
            skLineSegment(sketch, "E688", {"start": v(-21.72, 11.87) * mm, "end": v(-21.72, 11.92) * mm});
            skLineSegment(sketch, "E689", {"start": v(-21.72, 11.92) * mm, "end": v(-21.75, 12.66) * mm});
            skLineSegment(sketch, "E690", {"start": v(-21.75, 12.66) * mm, "end": v(-21.75, 12.85) * mm});
            skLineSegment(sketch, "E691", {"start": v(-21.75, 12.85) * mm, "end": v(-21.25, 13.1) * mm});
            skLineSegment(sketch, "E692", {"start": v(-21.25, 13.1) * mm, "end": v(-20.61, 13.24) * mm});
            skLineSegment(sketch, "E693", {"start": v(-20.61, 13.24) * mm, "end": v(-19.87, 13.35) * mm});
            skLineSegment(sketch, "E694", {"start": v(-19.87, 13.35) * mm, "end": v(-19.2, 13.53) * mm});
            skLineSegment(sketch, "E695", {"start": v(-19.2, 13.53) * mm, "end": v(-18.57, 13.75) * mm});
            skLineSegment(sketch, "E696", {"start": v(-18.57, 13.75) * mm, "end": v(-18, 13.88) * mm});
            skLineSegment(sketch, "E697", {"start": v(-18, 13.88) * mm, "end": v(-17.4, 13.98) * mm});
            skLineSegment(sketch, "E698", {"start": v(-17.4, 13.98) * mm, "end": v(-17.46, 9.99) * mm});
            skLineSegment(sketch, "E699", {"start": v(-17.46, 9.99) * mm, "end": v(-17.25, 6.1) * mm});
            skLineSegment(sketch, "E700", {"start": v(-17.25, 6.1) * mm, "end": v(-17.86, 5.91) * mm});
            skLineSegment(sketch, "E701", {"start": v(-17.86, 5.91) * mm, "end": v(-17.89, 5.91) * mm});
            skLineSegment(sketch, "E702", {"start": v(-17.89, 5.91) * mm, "end": v(-17.86, 5.86) * mm});
            skLineSegment(sketch, "E703", {"start": v(-17.86, 5.86) * mm, "end": v(-17.89, 5.83) * mm});
            skLineSegment(sketch, "E704", {"start": v(-17.89, 5.83) * mm, "end": v(-17.97, 5.86) * mm});
            skLineSegment(sketch, "E705", {"start": v(-17.97, 5.86) * mm, "end": v(-18.07, 5.73) * mm});
            skLineSegment(sketch, "E706", {"start": v(-18.07, 5.73) * mm, "end": v(-18.07, 5.7) * mm});
            skLineSegment(sketch, "E707", {"start": v(-18.07, 5.7) * mm, "end": v(-17.83, 5.56) * mm});
            skLineSegment(sketch, "E708", {"start": v(-17.83, 5.56) * mm, "end": v(-17.4, 5.52) * mm});
            skLineSegment(sketch, "E709", {"start": v(-17.4, 5.52) * mm, "end": v(-16.9, 5.33) * mm});
            skLineSegment(sketch, "E710", {"start": v(-16.9, 5.33) * mm, "end": v(-16.59, 5.38) * mm});
            skLineSegment(sketch, "E711", {"start": v(-16.59, 5.38) * mm, "end": v(-16.17, 5.36) * mm});
            skLineSegment(sketch, "E712", {"start": v(-16.17, 5.36) * mm, "end": v(-16.06, 5.36) * mm});
            skLineSegment(sketch, "E713", {"start": v(-16.06, 5.36) * mm, "end": v(-15.8, 5.41) * mm});
            skLineSegment(sketch, "E714", {"start": v(-15.8, 5.41) * mm, "end": v(-15.37, 5.38) * mm});
            skLineSegment(sketch, "E715", {"start": v(-15.37, 5.38) * mm, "end": v(-15.03, 5.43) * mm});
            skLineSegment(sketch, "E716", {"start": v(-15.03, 5.43) * mm, "end": v(-14.87, 5.6) * mm});
            skLineSegment(sketch, "E717", {"start": v(-14.87, 5.6) * mm, "end": v(-14.87, 5.65) * mm});
            skLineSegment(sketch, "E718", {"start": v(-14.87, 5.65) * mm, "end": v(-15.03, 5.73) * mm});
            skLineSegment(sketch, "E719", {"start": v(-15.03, 5.73) * mm, "end": v(-15.4, 5.7) * mm});
            skLineSegment(sketch, "E720", {"start": v(-15.4, 5.7) * mm, "end": v(-15.78, 5.76) * mm});
            skLineSegment(sketch, "E721", {"start": v(-15.78, 5.76) * mm, "end": v(-16, 5.94) * mm});
            skLineSegment(sketch, "E722", {"start": v(-16, 5.94) * mm, "end": v(-16.17, 6.15) * mm});
            skLineSegment(sketch, "E723", {"start": v(-16.17, 6.15) * mm, "end": v(-16.2, 6.36) * mm});
            skLineSegment(sketch, "E724", {"start": v(-16.2, 6.36) * mm, "end": v(-16.2, 6.6) * mm});
            skLineSegment(sketch, "E725", {"start": v(-16.2, 6.6) * mm, "end": v(-16.14, 7.02) * mm});
            skLineSegment(sketch, "E726", {"start": v(-16.14, 7.02) * mm, "end": v(-16.2, 7.26) * mm});
            skLineSegment(sketch, "E727", {"start": v(-16.2, 7.26) * mm, "end": v(-16.14, 7.45) * mm});
            skLineSegment(sketch, "E728", {"start": v(-16.14, 7.45) * mm, "end": v(-16.22, 7.95) * mm});
            skLineSegment(sketch, "E729", {"start": v(-16.22, 7.95) * mm, "end": v(-16.17, 8.19) * mm});
            skLineSegment(sketch, "E730", {"start": v(-16.17, 8.19) * mm, "end": v(-16.22, 8.59) * mm});
            skLineSegment(sketch, "E731", {"start": v(-16.22, 8.59) * mm, "end": v(-16.17, 9.14) * mm});
            skLineSegment(sketch, "E732", {"start": v(-16.17, 9.14) * mm, "end": v(-16.09, 9.86) * mm});
            skLineSegment(sketch, "E733", {"start": v(-16.09, 9.86) * mm, "end": v(-16.03, 9.99) * mm});
            skLineSegment(sketch, "E734", {"start": v(-16.03, 9.99) * mm, "end": v(-16.09, 10.97) * mm});
            skLineSegment(sketch, "E735", {"start": v(-16.09, 10.97) * mm, "end": v(-16.03, 11.55) * mm});
            skLineSegment(sketch, "E736", {"start": v(-16.03, 11.55) * mm, "end": v(-16.06, 12.13) * mm});
            skLineSegment(sketch, "E737", {"start": v(-16.06, 12.13) * mm, "end": v(-16.03, 12.63) * mm});
            skLineSegment(sketch, "E738", {"start": v(-16.03, 12.63) * mm, "end": v(-16.06, 13.1) * mm});
            skLineSegment(sketch, "E739", {"start": v(-16.06, 13.1) * mm, "end": v(-16.03, 13.5) * mm});
            skLineSegment(sketch, "E740", {"start": v(-16.03, 13.5) * mm, "end": v(-16.03, 13.67) * mm});
            skLineSegment(sketch, "E741", {"start": v(-16.03, 13.67) * mm, "end": v(-16, 13.85) * mm});
            skLineSegment(sketch, "E742", {"start": v(-16, 13.85) * mm, "end": v(-15.93, 13.88) * mm});
            skLineSegment(sketch, "E743", {"start": v(-15.93, 13.88) * mm, "end": v(-15.69, 13.72) * mm});
            skLineSegment(sketch, "E744", {"start": v(-15.69, 13.72) * mm, "end": v(-15.4, 12.98) * mm});
            skLineSegment(sketch, "E745", {"start": v(-15.4, 12.98) * mm, "end": v(-15.42, 12.77) * mm});
            skLineSegment(sketch, "E746", {"start": v(-15.42, 12.77) * mm, "end": v(-15.19, 12.47) * mm});
            skLineSegment(sketch, "E747", {"start": v(-15.19, 12.47) * mm, "end": v(-14.99, 12.16) * mm});
            skLineSegment(sketch, "E748", {"start": v(-14.99, 12.16) * mm, "end": v(-14.63, 12.05) * mm});
            skLineSegment(sketch, "E749", {"start": v(-14.63, 12.05) * mm, "end": v(-14.47, 12.05) * mm});
            skLineSegment(sketch, "E750", {"start": v(-14.47, 12.05) * mm, "end": v(-14, 12.2) * mm});
            skLineSegment(sketch, "E751", {"start": v(-14, 12.2) * mm, "end": v(-13.88, 12.44) * mm});
            skLineSegment(sketch, "E752", {"start": v(-13.88, 12.44) * mm, "end": v(-13.81, 12.69) * mm});
            skLineSegment(sketch, "E753", {"start": v(-13.81, 12.69) * mm, "end": v(-13.86, 12.98) * mm});
            skLineSegment(sketch, "E754", {"start": v(-13.86, 12.98) * mm, "end": v(-13.9, 13.35) * mm});
            skLineSegment(sketch, "E755", {"start": v(-13.9, 13.35) * mm, "end": v(-14.3, 13.85) * mm});
            skLineSegment(sketch, "E756", {"start": v(-14.3, 13.85) * mm, "end": v(-14.8, 14.22) * mm});
            skLineSegment(sketch, "E757", {"start": v(-14.8, 14.22) * mm, "end": v(-16.03, 14.78) * mm});
            skLineSegment(sketch, "E758", {"start": v(-16.03, 14.78) * mm, "end": v(-16.06, 15.38) * mm});
            skLineSegment(sketch, "E759", {"start": v(-16.06, 15.38) * mm, "end": v(-16.06, 16.02) * mm});
            skLineSegment(sketch, "E760", {"start": v(-16.06, 16.02) * mm, "end": v(-16.09, 16.18) * mm});
            skLineSegment(sketch, "E761", {"start": v(-16.09, 16.18) * mm, "end": v(-16.09, 16.4) * mm});
            skLineSegment(sketch, "E762", {"start": v(-16.09, 16.4) * mm, "end": v(-16.06, 17.18) * mm});
            skLineSegment(sketch, "E763", {"start": v(-16.06, 17.18) * mm, "end": v(-16.11, 17.56) * mm});
            skLineSegment(sketch, "E764", {"start": v(-16.11, 17.56) * mm, "end": v(-16.06, 17.74) * mm});
            skLineSegment(sketch, "E765", {"start": v(-16.06, 17.74) * mm, "end": v(-16.11, 18.43) * mm});
            skLineSegment(sketch, "E766", {"start": v(-16.11, 18.43) * mm, "end": v(-16.09, 19.09) * mm});
            skLineSegment(sketch, "E767", {"start": v(-16.09, 19.09) * mm, "end": v(-16.11, 19.6) * mm});
            skLineSegment(sketch, "E768", {"start": v(-16.11, 19.6) * mm, "end": v(-16.11, 19.72) * mm});
            skLineSegment(sketch, "E769", {"start": v(-16.11, 19.72) * mm, "end": v(-16.06, 20.33) * mm});
            skLineSegment(sketch, "E770", {"start": v(-16.06, 20.33) * mm, "end": v(-16, 20.97) * mm});
            skLineSegment(sketch, "E771", {"start": v(-16, 20.97) * mm, "end": v(-16, 21.6) * mm});
            skLineSegment(sketch, "E772", {"start": v(-16, 21.6) * mm, "end": v(-15.95, 21.82) * mm});
            skLineSegment(sketch, "E773", {"start": v(-15.95, 21.82) * mm, "end": v(-15.9, 22.03) * mm});
            skLineSegment(sketch, "E774", {"start": v(-15.9, 22.03) * mm, "end": v(-15.9, 22.1) * mm});
            skLineSegment(sketch, "E775", {"start": v(-15.9, 22.1) * mm, "end": v(-16.02, 22.45) * mm});
            skLineSegment(sketch, "E776", {"start": v(-16.02, 22.45) * mm, "end": v(-16.38, 22.53) * mm});
            skLineSegment(sketch, "E777", {"start": v(-16.38, 22.53) * mm, "end": v(-16.9, 22.58) * mm});
            skLineSegment(sketch, "E778", {"start": v(-16.9, 22.58) * mm, "end": v(-17.46, 22.56) * mm});
            skLineSegment(sketch, "E779", {"start": v(-17.46, 22.56) * mm, "end": v(-17.6, 22.56) * mm});
            skLineSegment(sketch, "E780", {"start": v(-17.6, 22.56) * mm, "end": v(-18.26, 22.66) * mm});
            skLineSegment(sketch, "E781", {"start": v(-18.26, 22.66) * mm, "end": v(-18.3, 22.63) * mm});
            skLineSegment(sketch, "E782", {"start": v(-10.16, 5.76) * mm, "end": v(-10.72, 5.97) * mm});
            skLineSegment(sketch, "E783", {"start": v(-10.72, 5.97) * mm, "end": v(-11.22, 6.23) * mm});
            skLineSegment(sketch, "E784", {"start": v(-11.22, 6.23) * mm, "end": v(-11.43, 6.44) * mm});
            skLineSegment(sketch, "E785", {"start": v(-11.43, 6.44) * mm, "end": v(-11.64, 6.6) * mm});
            skLineSegment(sketch, "E786", {"start": v(-11.64, 6.6) * mm, "end": v(-11.75, 6.76) * mm});
            skLineSegment(sketch, "E787", {"start": v(-11.75, 6.76) * mm, "end": v(-11.88, 6.92) * mm});
            skLineSegment(sketch, "E788", {"start": v(-11.88, 6.92) * mm, "end": v(-11.96, 7.13) * mm});
            skLineSegment(sketch, "E789", {"start": v(-11.96, 7.13) * mm, "end": v(-12.06, 7.34) * mm});
            skLineSegment(sketch, "E790", {"start": v(-12.06, 7.34) * mm, "end": v(-12.12, 7.55) * mm});
            skLineSegment(sketch, "E791", {"start": v(-12.12, 7.55) * mm, "end": v(-12.2, 7.71) * mm});
            skLineSegment(sketch, "E792", {"start": v(-12.2, 7.71) * mm, "end": v(-12.22, 7.95) * mm});
            skLineSegment(sketch, "E793", {"start": v(-12.22, 7.95) * mm, "end": v(-12.28, 8.45) * mm});
            skLineSegment(sketch, "E794", {"start": v(-12.28, 8.45) * mm, "end": v(-12.22, 8.96) * mm});
            skLineSegment(sketch, "E795", {"start": v(-12.22, 8.96) * mm, "end": v(-12.14, 9.27) * mm});
            skLineSegment(sketch, "E796", {"start": v(-12.14, 9.27) * mm, "end": v(-12.06, 9.62) * mm});
            skLineSegment(sketch, "E797", {"start": v(-12.06, 9.62) * mm, "end": v(-11.85, 10.25) * mm});
            skLineSegment(sketch, "E798", {"start": v(-11.85, 10.25) * mm, "end": v(-11.67, 10.54) * mm});
            skLineSegment(sketch, "E799", {"start": v(-11.67, 10.54) * mm, "end": v(-11.43, 10.83) * mm});
            skLineSegment(sketch, "E800", {"start": v(-11.43, 10.83) * mm, "end": v(-11.06, 11.26) * mm});
            skLineSegment(sketch, "E801", {"start": v(-11.06, 11.26) * mm, "end": v(-10.58, 11.5) * mm});
            skLineSegment(sketch, "E802", {"start": v(-10.58, 11.5) * mm, "end": v(-10.14, 11.6) * mm});
            skLineSegment(sketch, "E803", {"start": v(-10.14, 11.6) * mm, "end": v(-9.58, 11.63) * mm});
            skLineSegment(sketch, "E804", {"start": v(-9.58, 11.63) * mm, "end": v(-8.94, 11.55) * mm});
            skLineSegment(sketch, "E805", {"start": v(-8.94, 11.55) * mm, "end": v(-8.4, 11.25) * mm});
            skLineSegment(sketch, "E806", {"start": v(-8.4, 11.25) * mm, "end": v(-7.86, 10.78) * mm});
            skLineSegment(sketch, "E807", {"start": v(-7.86, 10.78) * mm, "end": v(-7.7, 10.5) * mm});
            skLineSegment(sketch, "E808", {"start": v(-7.7, 10.5) * mm, "end": v(-7.49, 10.23) * mm});
            skLineSegment(sketch, "E809", {"start": v(-7.49, 10.23) * mm, "end": v(-7.4, 10.02) * mm});
            skLineSegment(sketch, "E810", {"start": v(-7.4, 10.02) * mm, "end": v(-7.2, 9.38) * mm});
            skLineSegment(sketch, "E811", {"start": v(-7.2, 9.38) * mm, "end": v(-6.93, 8.59) * mm});
            skLineSegment(sketch, "E812", {"start": v(-6.93, 8.59) * mm, "end": v(-6.85, 8.14) * mm});
            skLineSegment(sketch, "E813", {"start": v(-6.85, 8.14) * mm, "end": v(-6.85, 7.87) * mm});
            skLineSegment(sketch, "E814", {"start": v(-6.85, 7.87) * mm, "end": v(-6.83, 7.63) * mm});
            skLineSegment(sketch, "E815", {"start": v(-6.83, 7.63) * mm, "end": v(-6.7, 7.29) * mm});
            skLineSegment(sketch, "E816", {"start": v(-6.7, 7.29) * mm, "end": v(-6.67, 7.18) * mm});
            skLineSegment(sketch, "E817", {"start": v(-6.67, 7.18) * mm, "end": v(-6.5, 6.76) * mm});
            skLineSegment(sketch, "E818", {"start": v(-6.5, 6.76) * mm, "end": v(-6.71, 6.44) * mm});
            skLineSegment(sketch, "E819", {"start": v(-6.71, 6.44) * mm, "end": v(-7.01, 6.18) * mm});
            skLineSegment(sketch, "E820", {"start": v(-7.01, 6.18) * mm, "end": v(-7.2, 6.02) * mm});
            skLineSegment(sketch, "E821", {"start": v(-7.2, 6.02) * mm, "end": v(-7.6, 5.8) * mm});
            skLineSegment(sketch, "E822", {"start": v(-7.6, 5.8) * mm, "end": v(-7.99, 5.6) * mm});
            skLineSegment(sketch, "E823", {"start": v(-7.99, 5.6) * mm, "end": v(-8.39, 5.54) * mm});
            skLineSegment(sketch, "E824", {"start": v(-8.39, 5.54) * mm, "end": v(-8.6, 5.54) * mm});
            skLineSegment(sketch, "E825", {"start": v(-8.6, 5.54) * mm, "end": v(-9.1, 5.57) * mm});
            skLineSegment(sketch, "E826", {"start": v(-9.1, 5.57) * mm, "end": v(-9.15, 5.57) * mm});
            skLineSegment(sketch, "E827", {"start": v(-9.15, 5.57) * mm, "end": v(-10.16, 5.76) * mm});
            skLineSegment(sketch, "E828", {"start": v(-10.85, 19.38) * mm, "end": v(-11.22, 19.25) * mm});
            skLineSegment(sketch, "E829", {"start": v(-11.22, 19.25) * mm, "end": v(-11.93, 18.93) * mm});
            skLineSegment(sketch, "E830", {"start": v(-11.93, 18.93) * mm, "end": v(-12.28, 18.72) * mm});
            skLineSegment(sketch, "E831", {"start": v(-12.28, 18.72) * mm, "end": v(-12.49, 18.5) * mm});
            skLineSegment(sketch, "E832", {"start": v(-12.49, 18.5) * mm, "end": v(-12.7, 18.3) * mm});
            skLineSegment(sketch, "E833", {"start": v(-12.7, 18.3) * mm, "end": v(-12.78, 18.16) * mm});
            skLineSegment(sketch, "E834", {"start": v(-12.78, 18.16) * mm, "end": v(-12.96, 17.93) * mm});
            skLineSegment(sketch, "E835", {"start": v(-12.96, 17.93) * mm, "end": v(-13.28, 17.3) * mm});
            skLineSegment(sketch, "E836", {"start": v(-13.28, 17.3) * mm, "end": v(-13.39, 17) * mm});
            skLineSegment(sketch, "E837", {"start": v(-13.39, 17) * mm, "end": v(-13.41, 16.84) * mm});
            skLineSegment(sketch, "E838", {"start": v(-13.41, 16.84) * mm, "end": v(-13.41, 16.7) * mm});
            skLineSegment(sketch, "E839", {"start": v(-13.41, 16.7) * mm, "end": v(-13.5, 16.44) * mm});
            skLineSegment(sketch, "E840", {"start": v(-13.5, 16.44) * mm, "end": v(-13.47, 16.2) * mm});
            skLineSegment(sketch, "E841", {"start": v(-13.47, 16.2) * mm, "end": v(-13.5, 16) * mm});
            skLineSegment(sketch, "E842", {"start": v(-13.5, 16) * mm, "end": v(-13.44, 15.68) * mm});
            skLineSegment(sketch, "E843", {"start": v(-13.44, 15.68) * mm, "end": v(-13.47, 15.38) * mm});
            skLineSegment(sketch, "E844", {"start": v(-13.47, 15.38) * mm, "end": v(-13.47, 15.3) * mm});
            skLineSegment(sketch, "E845", {"start": v(-13.47, 15.3) * mm, "end": v(-13.39, 14.96) * mm});
            skLineSegment(sketch, "E846", {"start": v(-13.39, 14.96) * mm, "end": v(-13.3, 14.62) * mm});
            skLineSegment(sketch, "E847", {"start": v(-13.3, 14.62) * mm, "end": v(-13.18, 14.43) * mm});
            skLineSegment(sketch, "E848", {"start": v(-13.18, 14.43) * mm, "end": v(-12.86, 14.14) * mm});
            skLineSegment(sketch, "E849", {"start": v(-12.86, 14.14) * mm, "end": v(-12.57, 14.12) * mm});
            skLineSegment(sketch, "E850", {"start": v(-12.57, 14.12) * mm, "end": v(-12.1, 14.2) * mm});
            skLineSegment(sketch, "E851", {"start": v(-12.1, 14.2) * mm, "end": v(-11.88, 14.33) * mm});
            skLineSegment(sketch, "E852", {"start": v(-11.88, 14.33) * mm, "end": v(-11.75, 14.51) * mm});
            skLineSegment(sketch, "E853", {"start": v(-11.75, 14.51) * mm, "end": v(-11.59, 14.72) * mm});
            skLineSegment(sketch, "E854", {"start": v(-11.59, 14.72) * mm, "end": v(-11.59, 14.8) * mm});
            skLineSegment(sketch, "E855", {"start": v(-11.59, 14.8) * mm, "end": v(-11.67, 15.2) * mm});
            skLineSegment(sketch, "E856", {"start": v(-11.67, 15.2) * mm, "end": v(-11.96, 15.44) * mm});
            skLineSegment(sketch, "E857", {"start": v(-11.96, 15.44) * mm, "end": v(-12.04, 15.52) * mm});
            skLineSegment(sketch, "E858", {"start": v(-12.04, 15.52) * mm, "end": v(-12.12, 15.57) * mm});
            skLineSegment(sketch, "E859", {"start": v(-12.12, 15.57) * mm, "end": v(-12.32, 15.8) * mm});
            skLineSegment(sketch, "E860", {"start": v(-12.32, 15.8) * mm, "end": v(-12.49, 16.07) * mm});
            skLineSegment(sketch, "E861", {"start": v(-12.49, 16.07) * mm, "end": v(-12.62, 16.34) * mm});
            skLineSegment(sketch, "E862", {"start": v(-12.62, 16.34) * mm, "end": v(-12.67, 16.7) * mm});
            skLineSegment(sketch, "E863", {"start": v(-12.67, 16.7) * mm, "end": v(-12.65, 16.97) * mm});
            skLineSegment(sketch, "E864", {"start": v(-12.65, 16.97) * mm, "end": v(-12.57, 17.21) * mm});
            skLineSegment(sketch, "E865", {"start": v(-12.57, 17.21) * mm, "end": v(-12.51, 17.5) * mm});
            skLineSegment(sketch, "E866", {"start": v(-12.51, 17.5) * mm, "end": v(-12.36, 17.71) * mm});
            skLineSegment(sketch, "E867", {"start": v(-12.36, 17.71) * mm, "end": v(-12.2, 17.93) * mm});
            skLineSegment(sketch, "E868", {"start": v(-12.2, 17.93) * mm, "end": v(-11.75, 18.43) * mm});
            skLineSegment(sketch, "E869", {"start": v(-11.75, 18.43) * mm, "end": v(-10.95, 18.77) * mm});
            skLineSegment(sketch, "E870", {"start": v(-10.95, 18.77) * mm, "end": v(-10.5, 18.88) * mm});
            skLineSegment(sketch, "E871", {"start": v(-10.5, 18.88) * mm, "end": v(-10.3, 18.85) * mm});
            skLineSegment(sketch, "E872", {"start": v(-10.3, 18.85) * mm, "end": v(-10.21, 18.88) * mm});
            skLineSegment(sketch, "E873", {"start": v(-10.21, 18.88) * mm, "end": v(-10.13, 18.85) * mm});
            skLineSegment(sketch, "E874", {"start": v(-10.13, 18.85) * mm, "end": v(-9.7, 18.85) * mm});
            skLineSegment(sketch, "E875", {"start": v(-9.7, 18.85) * mm, "end": v(-9.34, 18.7) * mm});
            skLineSegment(sketch, "E876", {"start": v(-9.34, 18.7) * mm, "end": v(-8.97, 18.56) * mm});
            skLineSegment(sketch, "E877", {"start": v(-8.97, 18.56) * mm, "end": v(-8.78, 18.43) * mm});
            skLineSegment(sketch, "E878", {"start": v(-8.78, 18.43) * mm, "end": v(-8.44, 18.22) * mm});
            skLineSegment(sketch, "E879", {"start": v(-8.44, 18.22) * mm, "end": v(-8.19, 17.97) * mm});
            skLineSegment(sketch, "E880", {"start": v(-8.19, 17.97) * mm, "end": v(-7.94, 17.74) * mm});
            skLineSegment(sketch, "E881", {"start": v(-7.94, 17.74) * mm, "end": v(-7.67, 17.45) * mm});
            skLineSegment(sketch, "E882", {"start": v(-7.67, 17.45) * mm, "end": v(-7.43, 17.16) * mm});
            skLineSegment(sketch, "E883", {"start": v(-7.43, 17.16) * mm, "end": v(-7.25, 16.76) * mm});
            skLineSegment(sketch, "E884", {"start": v(-7.25, 16.76) * mm, "end": v(-7.09, 16.37) * mm});
            skLineSegment(sketch, "E885", {"start": v(-7.09, 16.37) * mm, "end": v(-7.01, 15.7) * mm});
            skLineSegment(sketch, "E886", {"start": v(-7.01, 15.7) * mm, "end": v(-6.96, 15.12) * mm});
            skLineSegment(sketch, "E887", {"start": v(-6.96, 15.12) * mm, "end": v(-6.96, 14.99) * mm});
            skLineSegment(sketch, "E888", {"start": v(-6.96, 14.99) * mm, "end": v(-6.99, 14.38) * mm});
            skLineSegment(sketch, "E889", {"start": v(-6.99, 14.38) * mm, "end": v(-6.9, 13.67) * mm});
            skLineSegment(sketch, "E890", {"start": v(-6.9, 13.67) * mm, "end": v(-6.93, 12.8) * mm});
            skLineSegment(sketch, "E891", {"start": v(-6.93, 12.8) * mm, "end": v(-6.93, 12.58) * mm});
            skLineSegment(sketch, "E892", {"start": v(-6.93, 12.58) * mm, "end": v(-6.9, 12.03) * mm});
            skLineSegment(sketch, "E893", {"start": v(-6.9, 12.03) * mm, "end": v(-6.99, 11.52) * mm});
            skLineSegment(sketch, "E894", {"start": v(-6.99, 11.52) * mm, "end": v(-7.06, 10.78) * mm});
            skLineSegment(sketch, "E895", {"start": v(-7.06, 10.78) * mm, "end": v(-7.4, 11.02) * mm});
            skLineSegment(sketch, "E896", {"start": v(-7.4, 11.02) * mm, "end": v(-7.43, 11.05) * mm});
            skLineSegment(sketch, "E897", {"start": v(-7.43, 11.05) * mm, "end": v(-7.75, 11.4) * mm});
            skLineSegment(sketch, "E898", {"start": v(-7.75, 11.4) * mm, "end": v(-8.04, 11.58) * mm});
            skLineSegment(sketch, "E899", {"start": v(-8.04, 11.58) * mm, "end": v(-8.68, 11.92) * mm});
            skLineSegment(sketch, "E900", {"start": v(-8.68, 11.92) * mm, "end": v(-9.02, 12.1) * mm});
            skLineSegment(sketch, "E901", {"start": v(-9.02, 12.1) * mm, "end": v(-10, 12.24) * mm});
            skLineSegment(sketch, "E902", {"start": v(-10, 12.24) * mm, "end": v(-11.22, 12.16) * mm});
            skLineSegment(sketch, "E903", {"start": v(-11.22, 12.16) * mm, "end": v(-12.14, 11.84) * mm});
            skLineSegment(sketch, "E904", {"start": v(-12.14, 11.84) * mm, "end": v(-12.56, 11.45) * mm});
            skLineSegment(sketch, "E905", {"start": v(-12.56, 11.45) * mm, "end": v(-12.91, 10.97) * mm});
            skLineSegment(sketch, "E906", {"start": v(-12.91, 10.97) * mm, "end": v(-13.39, 10.23) * mm});
            skLineSegment(sketch, "E907", {"start": v(-13.39, 10.23) * mm, "end": v(-13.47, 9.99) * mm});
            skLineSegment(sketch, "E908", {"start": v(-13.47, 9.99) * mm, "end": v(-13.55, 9.75) * mm});
            skLineSegment(sketch, "E909", {"start": v(-13.55, 9.75) * mm, "end": v(-13.63, 9.2) * mm});
            skLineSegment(sketch, "E910", {"start": v(-13.63, 9.2) * mm, "end": v(-13.65, 8.8) * mm});
            skLineSegment(sketch, "E911", {"start": v(-13.65, 8.8) * mm, "end": v(-13.65, 8.61) * mm});
            skLineSegment(sketch, "E912", {"start": v(-13.65, 8.61) * mm, "end": v(-13.44, 7.82) * mm});
            skLineSegment(sketch, "E913", {"start": v(-13.44, 7.82) * mm, "end": v(-13.41, 7.74) * mm});
            skLineSegment(sketch, "E914", {"start": v(-13.41, 7.74) * mm, "end": v(-13.07, 6.95) * mm});
            skLineSegment(sketch, "E915", {"start": v(-13.07, 6.95) * mm, "end": v(-12.57, 6.31) * mm});
            skLineSegment(sketch, "E916", {"start": v(-12.57, 6.31) * mm, "end": v(-12.3, 6.05) * mm});
            skLineSegment(sketch, "E917", {"start": v(-12.3, 6.05) * mm, "end": v(-12.01, 5.76) * mm});
            skLineSegment(sketch, "E918", {"start": v(-12.01, 5.76) * mm, "end": v(-11.64, 5.57) * mm});
            skLineSegment(sketch, "E919", {"start": v(-11.64, 5.57) * mm, "end": v(-11.3, 5.41) * mm});
            skLineSegment(sketch, "E920", {"start": v(-11.3, 5.41) * mm, "end": v(-10.56, 5.15) * mm});
            skLineSegment(sketch, "E921", {"start": v(-10.56, 5.15) * mm, "end": v(-9.76, 4.96) * mm});
            skLineSegment(sketch, "E922", {"start": v(-9.76, 4.96) * mm, "end": v(-9.29, 4.96) * mm});
            skLineSegment(sketch, "E923", {"start": v(-9.29, 4.96) * mm, "end": v(-8.8, 4.93) * mm});
            skLineSegment(sketch, "E924", {"start": v(-8.8, 4.93) * mm, "end": v(-8.3, 5.01) * mm});
            skLineSegment(sketch, "E925", {"start": v(-8.3, 5.01) * mm, "end": v(-7.83, 5.12) * mm});
            skLineSegment(sketch, "E926", {"start": v(-7.83, 5.12) * mm, "end": v(-7.6, 5.28) * mm});
            skLineSegment(sketch, "E927", {"start": v(-7.6, 5.28) * mm, "end": v(-7.09, 5.5) * mm});
            skLineSegment(sketch, "E928", {"start": v(-7.09, 5.5) * mm, "end": v(-6.5, 5.91) * mm});
            skLineSegment(sketch, "E929", {"start": v(-6.5, 5.91) * mm, "end": v(-6.3, 6.07) * mm});
            skLineSegment(sketch, "E930", {"start": v(-6.3, 6.07) * mm, "end": v(-6.11, 6.2) * mm});
            skLineSegment(sketch, "E931", {"start": v(-6.11, 6.2) * mm, "end": v(-5.71, 6) * mm});
            skLineSegment(sketch, "E932", {"start": v(-5.71, 6) * mm, "end": v(-5.34, 5.76) * mm});
            skLineSegment(sketch, "E933", {"start": v(-5.34, 5.76) * mm, "end": v(-4.47, 5.5) * mm});
            skLineSegment(sketch, "E934", {"start": v(-4.47, 5.5) * mm, "end": v(-4.13, 5.41) * mm});
            skLineSegment(sketch, "E935", {"start": v(-4.13, 5.41) * mm, "end": v(-3.86, 5.5) * mm});
            skLineSegment(sketch, "E936", {"start": v(-3.86, 5.5) * mm, "end": v(-3.55, 5.54) * mm});
            skLineSegment(sketch, "E937", {"start": v(-3.55, 5.54) * mm, "end": v(-3.33, 5.8) * mm});
            skLineSegment(sketch, "E938", {"start": v(-3.33, 5.8) * mm, "end": v(-3.12, 6.1) * mm});
            skLineSegment(sketch, "E939", {"start": v(-3.12, 6.1) * mm, "end": v(-3.04, 6.44) * mm});
            skLineSegment(sketch, "E940", {"start": v(-3.04, 6.44) * mm, "end": v(-3.07, 6.6) * mm});
            skLineSegment(sketch, "E941", {"start": v(-3.07, 6.6) * mm, "end": v(-3.13, 6.74) * mm});
            skLineSegment(sketch, "E942", {"start": v(-3.13, 6.74) * mm, "end": v(-3.2, 6.87) * mm});
            skLineSegment(sketch, "E943", {"start": v(-3.2, 6.87) * mm, "end": v(-3.6, 6.95) * mm});
            skLineSegment(sketch, "E944", {"start": v(-3.6, 6.95) * mm, "end": v(-3.65, 6.95) * mm});
            skLineSegment(sketch, "E945", {"start": v(-3.65, 6.95) * mm, "end": v(-3.9, 6.75) * mm});
            skLineSegment(sketch, "E946", {"start": v(-3.9, 6.75) * mm, "end": v(-4.07, 6.5) * mm});
            skLineSegment(sketch, "E947", {"start": v(-4.07, 6.5) * mm, "end": v(-4.23, 6.42) * mm});
            skLineSegment(sketch, "E948", {"start": v(-4.23, 6.42) * mm, "end": v(-4.37, 6.31) * mm});
            skLineSegment(sketch, "E949", {"start": v(-4.37, 6.31) * mm, "end": v(-4.68, 6.23) * mm});
            skLineSegment(sketch, "E950", {"start": v(-4.68, 6.23) * mm, "end": v(-5.05, 6.44) * mm});
            skLineSegment(sketch, "E951", {"start": v(-5.05, 6.44) * mm, "end": v(-5.34, 6.58) * mm});
            skLineSegment(sketch, "E952", {"start": v(-5.34, 6.58) * mm, "end": v(-5.74, 7.34) * mm});
            skLineSegment(sketch, "E953", {"start": v(-5.74, 7.34) * mm, "end": v(-5.74, 7.37) * mm});
            skLineSegment(sketch, "E954", {"start": v(-5.74, 7.37) * mm, "end": v(-5.8, 7.58) * mm});
            skLineSegment(sketch, "E955", {"start": v(-5.8, 7.58) * mm, "end": v(-5.77, 7.87) * mm});
            skLineSegment(sketch, "E956", {"start": v(-5.77, 7.87) * mm, "end": v(-5.82, 8.14) * mm});
            skLineSegment(sketch, "E957", {"start": v(-5.82, 8.14) * mm, "end": v(-5.82, 8.5) * mm});
            skLineSegment(sketch, "E958", {"start": v(-5.82, 8.5) * mm, "end": v(-5.66, 9.67) * mm});
            skLineSegment(sketch, "E959", {"start": v(-5.66, 9.67) * mm, "end": v(-5.58, 10.04) * mm});
            skLineSegment(sketch, "E960", {"start": v(-5.58, 10.04) * mm, "end": v(-5.48, 11.1) * mm});
            skLineSegment(sketch, "E961", {"start": v(-5.48, 11.1) * mm, "end": v(-5.37, 11.92) * mm});
            skLineSegment(sketch, "E962", {"start": v(-5.37, 11.92) * mm, "end": v(-5.37, 12.13) * mm});
            skLineSegment(sketch, "E963", {"start": v(-5.37, 12.13) * mm, "end": v(-5.34, 12.34) * mm});
            skLineSegment(sketch, "E964", {"start": v(-5.34, 12.34) * mm, "end": v(-5.19, 12.98) * mm});
            skLineSegment(sketch, "E965", {"start": v(-5.19, 12.98) * mm, "end": v(-5.1, 13.61) * mm});
            skLineSegment(sketch, "E966", {"start": v(-5.1, 13.61) * mm, "end": v(-5.05, 14.25) * mm});
            skLineSegment(sketch, "E967", {"start": v(-5.05, 14.25) * mm, "end": v(-5, 14.75) * mm});
            skLineSegment(sketch, "E968", {"start": v(-5, 14.75) * mm, "end": v(-5, 14.8) * mm});
            skLineSegment(sketch, "E969", {"start": v(-5, 14.8) * mm, "end": v(-5.05, 15.12) * mm});
            skLineSegment(sketch, "E970", {"start": v(-5.05, 15.12) * mm, "end": v(-5.05, 15.47) * mm});
            skLineSegment(sketch, "E971", {"start": v(-5.05, 15.47) * mm, "end": v(-5.24, 16.2) * mm});
            skLineSegment(sketch, "E972", {"start": v(-5.24, 16.2) * mm, "end": v(-5.27, 16.26) * mm});
            skLineSegment(sketch, "E973", {"start": v(-5.27, 16.26) * mm, "end": v(-5.34, 16.47) * mm});
            skLineSegment(sketch, "E974", {"start": v(-5.34, 16.47) * mm, "end": v(-5.42, 16.7) * mm});
            skLineSegment(sketch, "E975", {"start": v(-5.42, 16.7) * mm, "end": v(-5.63, 17.08) * mm});
            skLineSegment(sketch, "E976", {"start": v(-5.63, 17.08) * mm, "end": v(-5.71, 17.32) * mm});
            skLineSegment(sketch, "E977", {"start": v(-5.71, 17.32) * mm, "end": v(-6.06, 17.93) * mm});
            skLineSegment(sketch, "E978", {"start": v(-6.06, 17.93) * mm, "end": v(-6.2, 18.11) * mm});
            skLineSegment(sketch, "E979", {"start": v(-6.2, 18.11) * mm, "end": v(-6.35, 18.3) * mm});
            skLineSegment(sketch, "E980", {"start": v(-6.35, 18.3) * mm, "end": v(-6.67, 18.64) * mm});
            skLineSegment(sketch, "E981", {"start": v(-6.67, 18.64) * mm, "end": v(-6.88, 18.77) * mm});
            skLineSegment(sketch, "E982", {"start": v(-6.88, 18.77) * mm, "end": v(-7.28, 19.01) * mm});
            skLineSegment(sketch, "E983", {"start": v(-7.28, 19.01) * mm, "end": v(-8.02, 19.3) * mm});
            skLineSegment(sketch, "E984", {"start": v(-8.02, 19.3) * mm, "end": v(-8.92, 19.4) * mm});
            skLineSegment(sketch, "E985", {"start": v(-8.92, 19.4) * mm, "end": v(-9.84, 19.43) * mm});
            skLineSegment(sketch, "E986", {"start": v(-9.84, 19.43) * mm, "end": v(-10.85, 19.38) * mm});
            skLineSegment(sketch, "E987", {"start": v(17.86, 14.27) * mm, "end": v(17.89, 15.07) * mm});
            skLineSegment(sketch, "E988", {"start": v(17.89, 15.07) * mm, "end": v(17.89, 15.33) * mm});
            skLineSegment(sketch, "E989", {"start": v(17.89, 15.33) * mm, "end": v(18.02, 15.36) * mm});
            skLineSegment(sketch, "E990", {"start": v(18.02, 15.36) * mm, "end": v(18.41, 15.2) * mm});
            skLineSegment(sketch, "E991", {"start": v(18.41, 15.2) * mm, "end": v(18.6, 15.04) * mm});
            skLineSegment(sketch, "E992", {"start": v(18.6, 15.04) * mm, "end": v(19.29, 14.54) * mm});
            skLineSegment(sketch, "E993", {"start": v(19.29, 14.54) * mm, "end": v(19.58, 14.22) * mm});
            skLineSegment(sketch, "E994", {"start": v(19.58, 14.22) * mm, "end": v(19.26, 14) * mm});
            skLineSegment(sketch, "E995", {"start": v(19.26, 14) * mm, "end": v(18.97, 13.8) * mm});
            skLineSegment(sketch, "E996", {"start": v(18.97, 13.8) * mm, "end": v(18.57, 13.7) * mm});
            skLineSegment(sketch, "E997", {"start": v(18.57, 13.7) * mm, "end": v(18.1, 13.67) * mm});
            skLineSegment(sketch, "E998", {"start": v(18.1, 13.67) * mm, "end": v(17.91, 13.67) * mm});
            skLineSegment(sketch, "E999", {"start": v(17.91, 13.67) * mm, "end": v(17.86, 14.27) * mm});
            skLineSegment(sketch, "E1000", {"start": v(15.35, 13.85) * mm, "end": v(15.1, 14.17) * mm});
            skLineSegment(sketch, "E1001", {"start": v(15.1, 14.17) * mm, "end": v(15, 14.62) * mm});
            skLineSegment(sketch, "E1002", {"start": v(15, 14.62) * mm, "end": v(15, 14.8) * mm});
            skLineSegment(sketch, "E1003", {"start": v(15, 14.8) * mm, "end": v(15.17, 15.16) * mm});
            skLineSegment(sketch, "E1004", {"start": v(15.17, 15.16) * mm, "end": v(15.35, 15.47) * mm});
            skLineSegment(sketch, "E1005", {"start": v(15.35, 15.47) * mm, "end": v(16.25, 15.76) * mm});
            skLineSegment(sketch, "E1006", {"start": v(16.25, 15.76) * mm, "end": v(16.4, 15.76) * mm});
            skLineSegment(sketch, "E1007", {"start": v(16.4, 15.76) * mm, "end": v(16.6, 15.7) * mm});
            skLineSegment(sketch, "E1008", {"start": v(16.6, 15.7) * mm, "end": v(16.64, 15.33) * mm});
            skLineSegment(sketch, "E1009", {"start": v(16.64, 15.33) * mm, "end": v(16.7, 14.35) * mm});
            skLineSegment(sketch, "E1010", {"start": v(16.7, 14.35) * mm, "end": v(16.7, 14.12) * mm});
            skLineSegment(sketch, "E1011", {"start": v(16.7, 14.12) * mm, "end": v(16.37, 13.94) * mm});
            skLineSegment(sketch, "E1012", {"start": v(16.37, 13.94) * mm, "end": v(15.98, 13.8) * mm});
            skLineSegment(sketch, "E1013", {"start": v(15.98, 13.8) * mm, "end": v(15.93, 13.77) * mm});
            skLineSegment(sketch, "E1014", {"start": v(15.93, 13.77) * mm, "end": v(15.72, 13.75) * mm});
            skLineSegment(sketch, "E1015", {"start": v(15.72, 13.75) * mm, "end": v(15.35, 13.85) * mm});
            skLineSegment(sketch, "E1016", {"start": v(25.3, 25.33) * mm, "end": v(24.84, 24.65) * mm});
            skLineSegment(sketch, "E1017", {"start": v(24.84, 24.65) * mm, "end": v(24.53, 23.85) * mm});
            skLineSegment(sketch, "E1018", {"start": v(24.53, 23.85) * mm, "end": v(24.32, 22.98) * mm});
            skLineSegment(sketch, "E1019", {"start": v(24.32, 22.98) * mm, "end": v(23.97, 21.05) * mm});
            skLineSegment(sketch, "E1020", {"start": v(23.97, 21.05) * mm, "end": v(23.81, 20.07) * mm});
            skLineSegment(sketch, "E1021", {"start": v(23.81, 20.07) * mm, "end": v(23.57, 18.96) * mm});
            skLineSegment(sketch, "E1022", {"start": v(23.57, 18.96) * mm, "end": v(23.52, 18.75) * mm});
            skLineSegment(sketch, "E1023", {"start": v(23.52, 18.75) * mm, "end": v(23.36, 18.32) * mm});
            skLineSegment(sketch, "E1024", {"start": v(23.36, 18.32) * mm, "end": v(22.89, 17.63) * mm});
            skLineSegment(sketch, "E1025", {"start": v(22.89, 17.63) * mm, "end": v(22.46, 16.87) * mm});
            skLineSegment(sketch, "E1026", {"start": v(22.46, 16.87) * mm, "end": v(21.78, 16.2) * mm});
            skLineSegment(sketch, "E1027", {"start": v(21.78, 16.2) * mm, "end": v(21.59, 15.97) * mm});
            skLineSegment(sketch, "E1028", {"start": v(21.59, 15.97) * mm, "end": v(20.66, 15.12) * mm});
            skLineSegment(sketch, "E1029", {"start": v(20.66, 15.12) * mm, "end": v(20.5, 14.88) * mm});
            skLineSegment(sketch, "E1030", {"start": v(20.5, 14.88) * mm, "end": v(20.3, 14.72) * mm});
            skLineSegment(sketch, "E1031", {"start": v(20.3, 14.72) * mm, "end": v(20.27, 14.72) * mm});
            skLineSegment(sketch, "E1032", {"start": v(20.27, 14.72) * mm, "end": v(19.87, 14.9) * mm});
            skLineSegment(sketch, "E1033", {"start": v(19.87, 14.9) * mm, "end": v(19.18, 15.44) * mm});
            skLineSegment(sketch, "E1034", {"start": v(19.18, 15.44) * mm, "end": v(18.81, 15.73) * mm});
            skLineSegment(sketch, "E1035", {"start": v(18.81, 15.73) * mm, "end": v(18.29, 15.95) * mm});
            skLineSegment(sketch, "E1036", {"start": v(18.29, 15.95) * mm, "end": v(17.78, 16.2) * mm});
            skLineSegment(sketch, "E1037", {"start": v(17.78, 16.2) * mm, "end": v(17.8, 17.9) * mm});
            skLineSegment(sketch, "E1038", {"start": v(17.8, 17.9) * mm, "end": v(17.78, 19.54) * mm});
            skLineSegment(sketch, "E1039", {"start": v(17.78, 19.54) * mm, "end": v(17.78, 19.72) * mm});
            skLineSegment(sketch, "E1040", {"start": v(17.78, 19.72) * mm, "end": v(17.83, 20.8) * mm});
            skLineSegment(sketch, "E1041", {"start": v(17.83, 20.8) * mm, "end": v(17.8, 21.13) * mm});
            skLineSegment(sketch, "E1042", {"start": v(17.8, 21.13) * mm, "end": v(17.75, 21.37) * mm});
            skLineSegment(sketch, "E1043", {"start": v(17.75, 21.37) * mm, "end": v(17.73, 21.92) * mm});
            skLineSegment(sketch, "E1044", {"start": v(17.73, 21.92) * mm, "end": v(17.91, 23.5) * mm});
            skLineSegment(sketch, "E1045", {"start": v(17.91, 23.5) * mm, "end": v(18.47, 23.72) * mm});
            skLineSegment(sketch, "E1046", {"start": v(18.47, 23.72) * mm, "end": v(18.57, 23.72) * mm});
            skLineSegment(sketch, "E1047", {"start": v(18.57, 23.72) * mm, "end": v(18.97, 23.62) * mm});
            skLineSegment(sketch, "E1048", {"start": v(18.97, 23.62) * mm, "end": v(19.1, 23.64) * mm});
            skLineSegment(sketch, "E1049", {"start": v(19.1, 23.64) * mm, "end": v(19.2, 23.75) * mm});
            skLineSegment(sketch, "E1050", {"start": v(19.2, 23.75) * mm, "end": v(19.24, 23.85) * mm});
            skLineSegment(sketch, "E1051", {"start": v(19.24, 23.85) * mm, "end": v(19.14, 24.16) * mm});
            skLineSegment(sketch, "E1052", {"start": v(19.14, 24.16) * mm, "end": v(19.02, 24.46) * mm});
            skLineSegment(sketch, "E1053", {"start": v(19.02, 24.46) * mm, "end": v(19.05, 24.65) * mm});
            skLineSegment(sketch, "E1054", {"start": v(19.05, 24.65) * mm, "end": v(19, 24.83) * mm});
            skLineSegment(sketch, "E1055", {"start": v(19, 24.83) * mm, "end": v(18.87, 24.88) * mm});
            skLineSegment(sketch, "E1056", {"start": v(18.87, 24.88) * mm, "end": v(18.39, 24.75) * mm});
            skLineSegment(sketch, "E1057", {"start": v(18.39, 24.75) * mm, "end": v(17.57, 24.75) * mm});
            skLineSegment(sketch, "E1058", {"start": v(17.57, 24.75) * mm, "end": v(17.41, 24.73) * mm});
            skLineSegment(sketch, "E1059", {"start": v(17.41, 24.73) * mm, "end": v(17.22, 24.75) * mm});
            skLineSegment(sketch, "E1060", {"start": v(17.22, 24.75) * mm, "end": v(16.8, 24.75) * mm});
            skLineSegment(sketch, "E1061", {"start": v(16.8, 24.75) * mm, "end": v(16.4, 24.7) * mm});
            skLineSegment(sketch, "E1062", {"start": v(16.4, 24.7) * mm, "end": v(16.25, 24.7) * mm});
            skLineSegment(sketch, "E1063", {"start": v(16.25, 24.7) * mm, "end": v(15.56, 24.73) * mm});
            skLineSegment(sketch, "E1064", {"start": v(15.56, 24.73) * mm, "end": v(15.32, 24.7) * mm});
            skLineSegment(sketch, "E1065", {"start": v(15.32, 24.7) * mm, "end": v(15.08, 24.44) * mm});
            skLineSegment(sketch, "E1066", {"start": v(15.08, 24.44) * mm, "end": v(15, 24.04) * mm});
            skLineSegment(sketch, "E1067", {"start": v(15, 24.04) * mm, "end": v(15.03, 23.7) * mm});
            skLineSegment(sketch, "E1068", {"start": v(15.03, 23.7) * mm, "end": v(15.03, 23.67) * mm});
            skLineSegment(sketch, "E1069", {"start": v(15.03, 23.67) * mm, "end": v(15.24, 23.43) * mm});
            skLineSegment(sketch, "E1070", {"start": v(15.24, 23.43) * mm, "end": v(15.37, 23.4) * mm});
            skLineSegment(sketch, "E1071", {"start": v(15.37, 23.4) * mm, "end": v(15.58, 23.47) * mm});
            skLineSegment(sketch, "E1072", {"start": v(15.58, 23.47) * mm, "end": v(15.85, 23.53) * mm});
            skLineSegment(sketch, "E1073", {"start": v(15.85, 23.53) * mm, "end": v(15.9, 23.53) * mm});
            skLineSegment(sketch, "E1074", {"start": v(15.9, 23.53) * mm, "end": v(16.09, 23.03) * mm});
            skLineSegment(sketch, "E1075", {"start": v(16.09, 23.03) * mm, "end": v(16.09, 23) * mm});
            skLineSegment(sketch, "E1076", {"start": v(16.09, 23) * mm, "end": v(16.22, 22.34) * mm});
            skLineSegment(sketch, "E1077", {"start": v(16.22, 22.34) * mm, "end": v(16.22, 21.6) * mm});
            skLineSegment(sketch, "E1078", {"start": v(16.22, 21.6) * mm, "end": v(16.27, 21.13) * mm});
            skLineSegment(sketch, "E1079", {"start": v(16.27, 21.13) * mm, "end": v(16.27, 20.94) * mm});
            skLineSegment(sketch, "E1080", {"start": v(16.27, 20.94) * mm, "end": v(16.25, 20.23) * mm});
            skLineSegment(sketch, "E1081", {"start": v(16.25, 20.23) * mm, "end": v(16.27, 19.91) * mm});
            skLineSegment(sketch, "E1082", {"start": v(16.27, 19.91) * mm, "end": v(16.51, 16.87) * mm});
            skLineSegment(sketch, "E1083", {"start": v(16.51, 16.87) * mm, "end": v(16.54, 16.44) * mm});
            skLineSegment(sketch, "E1084", {"start": v(16.54, 16.44) * mm, "end": v(16.54, 16.28) * mm});
            skLineSegment(sketch, "E1085", {"start": v(16.54, 16.28) * mm, "end": v(15.4, 16.1) * mm});
            skLineSegment(sketch, "E1086", {"start": v(15.4, 16.1) * mm, "end": v(14.92, 15.94) * mm});
            skLineSegment(sketch, "E1087", {"start": v(14.92, 15.94) * mm, "end": v(14.6, 15.65) * mm});
            skLineSegment(sketch, "E1088", {"start": v(14.6, 15.65) * mm, "end": v(14.37, 15.3) * mm});
            skLineSegment(sketch, "E1089", {"start": v(14.37, 15.3) * mm, "end": v(14.2, 14.57) * mm});
            skLineSegment(sketch, "E1090", {"start": v(14.2, 14.57) * mm, "end": v(14.34, 13.88) * mm});
            skLineSegment(sketch, "E1091", {"start": v(14.34, 13.88) * mm, "end": v(14.52, 13.56) * mm});
            skLineSegment(sketch, "E1092", {"start": v(14.52, 13.56) * mm, "end": v(14.76, 13.35) * mm});
            skLineSegment(sketch, "E1093", {"start": v(14.76, 13.35) * mm, "end": v(14.8, 13.32) * mm});
            skLineSegment(sketch, "E1094", {"start": v(14.8, 13.32) * mm, "end": v(15.1, 13.08) * mm});
            skLineSegment(sketch, "E1095", {"start": v(15.1, 13.08) * mm, "end": v(15.66, 12.87) * mm});
            skLineSegment(sketch, "E1096", {"start": v(15.66, 12.87) * mm, "end": v(16.2, 12.84) * mm});
            skLineSegment(sketch, "E1097", {"start": v(16.2, 12.84) * mm, "end": v(16.72, 12.71) * mm});
            skLineSegment(sketch, "E1098", {"start": v(16.72, 12.71) * mm, "end": v(16.75, 12.47) * mm});
            skLineSegment(sketch, "E1099", {"start": v(16.75, 12.47) * mm, "end": v(16.64, 11.6) * mm});
            skLineSegment(sketch, "E1100", {"start": v(16.64, 11.6) * mm, "end": v(16.7, 11.13) * mm});
            skLineSegment(sketch, "E1101", {"start": v(16.7, 11.13) * mm, "end": v(16.7, 10.83) * mm});
            skLineSegment(sketch, "E1102", {"start": v(16.7, 10.83) * mm, "end": v(16.67, 10.12) * mm});
            skLineSegment(sketch, "E1103", {"start": v(16.67, 10.12) * mm, "end": v(16.67, 9.03) * mm});
            skLineSegment(sketch, "E1104", {"start": v(16.67, 9.03) * mm, "end": v(16.64, 8.72) * mm});
            skLineSegment(sketch, "E1105", {"start": v(16.64, 8.72) * mm, "end": v(16.7, 8) * mm});
            skLineSegment(sketch, "E1106", {"start": v(16.7, 8) * mm, "end": v(16.75, 7.24) * mm});
            skLineSegment(sketch, "E1107", {"start": v(16.75, 7.24) * mm, "end": v(16.75, 6.68) * mm});
            skLineSegment(sketch, "E1108", {"start": v(16.75, 6.68) * mm, "end": v(16.38, 6.36) * mm});
            skLineSegment(sketch, "E1109", {"start": v(16.38, 6.36) * mm, "end": v(15.98, 6.12) * mm});
            skLineSegment(sketch, "E1110", {"start": v(15.98, 6.12) * mm, "end": v(15.48, 6.07) * mm});
            skLineSegment(sketch, "E1111", {"start": v(15.48, 6.07) * mm, "end": v(15.26, 5.91) * mm});
            skLineSegment(sketch, "E1112", {"start": v(15.26, 5.91) * mm, "end": v(15.16, 5.68) * mm});
            skLineSegment(sketch, "E1113", {"start": v(15.16, 5.68) * mm, "end": v(15.25, 5.52) * mm});
            skLineSegment(sketch, "E1114", {"start": v(15.25, 5.52) * mm, "end": v(15.37, 5.33) * mm});
            skLineSegment(sketch, "E1115", {"start": v(15.37, 5.33) * mm, "end": v(15.52, 5.08) * mm});
            skLineSegment(sketch, "E1116", {"start": v(15.52, 5.08) * mm, "end": v(15.7, 4.93) * mm});
            skLineSegment(sketch, "E1117", {"start": v(15.7, 4.93) * mm, "end": v(15.87, 4.9) * mm});
            skLineSegment(sketch, "E1118", {"start": v(15.87, 4.9) * mm, "end": v(16.11, 5) * mm});
            skLineSegment(sketch, "E1119", {"start": v(16.11, 5) * mm, "end": v(16.35, 5.15) * mm});
            skLineSegment(sketch, "E1120", {"start": v(16.35, 5.15) * mm, "end": v(17.28, 5.38) * mm});
            skLineSegment(sketch, "E1121", {"start": v(17.28, 5.38) * mm, "end": v(17.62, 5.5) * mm});
            skLineSegment(sketch, "E1122", {"start": v(17.62, 5.5) * mm, "end": v(18.32, 5.45) * mm});
            skLineSegment(sketch, "E1123", {"start": v(18.32, 5.45) * mm, "end": v(19, 5.36) * mm});
            skLineSegment(sketch, "E1124", {"start": v(19, 5.36) * mm, "end": v(19.47, 5.23) * mm});
            skLineSegment(sketch, "E1125", {"start": v(19.47, 5.23) * mm, "end": v(19.53, 5.23) * mm});
            skLineSegment(sketch, "E1126", {"start": v(19.53, 5.23) * mm, "end": v(19.76, 5.3) * mm});
            skLineSegment(sketch, "E1127", {"start": v(19.76, 5.3) * mm, "end": v(19.92, 5.46) * mm});
            skLineSegment(sketch, "E1128", {"start": v(19.92, 5.46) * mm, "end": v(19.92, 5.57) * mm});
            skLineSegment(sketch, "E1129", {"start": v(19.92, 5.57) * mm, "end": v(19.9, 5.8) * mm});
            skLineSegment(sketch, "E1130", {"start": v(19.9, 5.8) * mm, "end": v(19.65, 6.1) * mm});
            skLineSegment(sketch, "E1131", {"start": v(19.65, 6.1) * mm, "end": v(19.31, 6.28) * mm});
            skLineSegment(sketch, "E1132", {"start": v(19.31, 6.28) * mm, "end": v(18.92, 6.23) * mm});
            skLineSegment(sketch, "E1133", {"start": v(18.92, 6.23) * mm, "end": v(18.57, 6.26) * mm});
            skLineSegment(sketch, "E1134", {"start": v(18.57, 6.26) * mm, "end": v(18.47, 6.26) * mm});
            skLineSegment(sketch, "E1135", {"start": v(18.47, 6.26) * mm, "end": v(18.1, 6.65) * mm});
            skLineSegment(sketch, "E1136", {"start": v(18.1, 6.65) * mm, "end": v(18.1, 6.79) * mm});
            skLineSegment(sketch, "E1137", {"start": v(18.1, 6.79) * mm, "end": v(18.15, 7.29) * mm});
            skLineSegment(sketch, "E1138", {"start": v(18.15, 7.29) * mm, "end": v(18.15, 7.6) * mm});
            skLineSegment(sketch, "E1139", {"start": v(18.15, 7.6) * mm, "end": v(18.2, 7.9) * mm});
            skLineSegment(sketch, "E1140", {"start": v(18.2, 7.9) * mm, "end": v(18.15, 8.3) * mm});
            skLineSegment(sketch, "E1141", {"start": v(18.15, 8.3) * mm, "end": v(18.18, 8.77) * mm});
            skLineSegment(sketch, "E1142", {"start": v(18.18, 8.77) * mm, "end": v(18.15, 9.27) * mm});
            skLineSegment(sketch, "E1143", {"start": v(18.15, 9.27) * mm, "end": v(18.05, 10.2) * mm});
            skLineSegment(sketch, "E1144", {"start": v(18.05, 10.2) * mm, "end": v(18.05, 11.36) * mm});
            skLineSegment(sketch, "E1145", {"start": v(18.05, 11.36) * mm, "end": v(17.91, 12.47) * mm});
            skLineSegment(sketch, "E1146", {"start": v(17.91, 12.47) * mm, "end": v(18.28, 12.69) * mm});
            skLineSegment(sketch, "E1147", {"start": v(18.28, 12.69) * mm, "end": v(18.79, 12.8) * mm});
            skLineSegment(sketch, "E1148", {"start": v(18.79, 12.8) * mm, "end": v(19.08, 12.95) * mm});
            skLineSegment(sketch, "E1149", {"start": v(19.08, 12.95) * mm, "end": v(19.77, 13.1) * mm});
            skLineSegment(sketch, "E1150", {"start": v(19.77, 13.1) * mm, "end": v(20.08, 13.22) * mm});
            skLineSegment(sketch, "E1151", {"start": v(20.08, 13.22) * mm, "end": v(20.4, 13.32) * mm});
            skLineSegment(sketch, "E1152", {"start": v(20.4, 13.32) * mm, "end": v(20.45, 13.32) * mm});
            skLineSegment(sketch, "E1153", {"start": v(20.45, 13.32) * mm, "end": v(20.7, 13.08) * mm});
            skLineSegment(sketch, "E1154", {"start": v(20.7, 13.08) * mm, "end": v(21.17, 12.53) * mm});
            skLineSegment(sketch, "E1155", {"start": v(21.17, 12.53) * mm, "end": v(21.46, 12.03) * mm});
            skLineSegment(sketch, "E1156", {"start": v(21.46, 12.03) * mm, "end": v(21.8, 11.6) * mm});
            skLineSegment(sketch, "E1157", {"start": v(21.8, 11.6) * mm, "end": v(22.57, 10.36) * mm});
            skLineSegment(sketch, "E1158", {"start": v(22.57, 10.36) * mm, "end": v(23.36, 9.14) * mm});
            skLineSegment(sketch, "E1159", {"start": v(23.36, 9.14) * mm, "end": v(23.84, 8.56) * mm});
            skLineSegment(sketch, "E1160", {"start": v(23.84, 8.56) * mm, "end": v(24.32, 8) * mm});
            skLineSegment(sketch, "E1161", {"start": v(24.32, 8) * mm, "end": v(24.55, 7.77) * mm});
            skLineSegment(sketch, "E1162", {"start": v(24.55, 7.77) * mm, "end": v(24.98, 7.21) * mm});
            skLineSegment(sketch, "E1163", {"start": v(24.98, 7.21) * mm, "end": v(26.25, 5.91) * mm});
            skLineSegment(sketch, "E1164", {"start": v(26.25, 5.91) * mm, "end": v(26.83, 5.52) * mm});
            skLineSegment(sketch, "E1165", {"start": v(26.83, 5.52) * mm, "end": v(27.5, 5.12) * mm});
            skLineSegment(sketch, "E1166", {"start": v(27.5, 5.12) * mm, "end": v(28.18, 4.78) * mm});
            skLineSegment(sketch, "E1167", {"start": v(28.18, 4.78) * mm, "end": v(29.6, 4.2) * mm});
            skLineSegment(sketch, "E1168", {"start": v(29.6, 4.2) * mm, "end": v(30.77, 3.85) * mm});
            skLineSegment(sketch, "E1169", {"start": v(30.77, 3.85) * mm, "end": v(31.17, 3.8) * mm});
            skLineSegment(sketch, "E1170", {"start": v(31.17, 3.8) * mm, "end": v(31.9, 3.74) * mm});
            skLineSegment(sketch, "E1171", {"start": v(31.9, 3.74) * mm, "end": v(33.05, 3.77) * mm});
            skLineSegment(sketch, "E1172", {"start": v(33.05, 3.77) * mm, "end": v(33.97, 3.87) * mm});
            skLineSegment(sketch, "E1173", {"start": v(33.97, 3.87) * mm, "end": v(34.8, 4.09) * mm});
            skLineSegment(sketch, "E1174", {"start": v(34.8, 4.09) * mm, "end": v(35.53, 4.4) * mm});
            skLineSegment(sketch, "E1175", {"start": v(35.53, 4.4) * mm, "end": v(35.82, 4.6) * mm});
            skLineSegment(sketch, "E1176", {"start": v(35.82, 4.6) * mm, "end": v(36.94, 5.01) * mm});
            skLineSegment(sketch, "E1177", {"start": v(36.94, 5.01) * mm, "end": v(37.6, 5.38) * mm});
            skLineSegment(sketch, "E1178", {"start": v(37.6, 5.38) * mm, "end": v(38.26, 5.76) * mm});
            skLineSegment(sketch, "E1179", {"start": v(38.26, 5.76) * mm, "end": v(38.83, 6.17) * mm});
            skLineSegment(sketch, "E1180", {"start": v(38.83, 6.17) * mm, "end": v(39.37, 6.65) * mm});
            skLineSegment(sketch, "E1181", {"start": v(39.37, 6.65) * mm, "end": v(39.95, 7.08) * mm});
            skLineSegment(sketch, "E1182", {"start": v(39.95, 7.08) * mm, "end": v(40.32, 7.42) * mm});
            skLineSegment(sketch, "E1183", {"start": v(40.32, 7.42) * mm, "end": v(40.72, 7.74) * mm});
            skLineSegment(sketch, "E1184", {"start": v(40.72, 7.74) * mm, "end": v(41.49, 8.4) * mm});
            skLineSegment(sketch, "E1185", {"start": v(41.49, 8.4) * mm, "end": v(42.02, 8.72) * mm});
            skLineSegment(sketch, "E1186", {"start": v(42.02, 8.72) * mm, "end": v(42.44, 9.09) * mm});
            skLineSegment(sketch, "E1187", {"start": v(42.44, 9.09) * mm, "end": v(42.92, 9.27) * mm});
            skLineSegment(sketch, "E1188", {"start": v(42.92, 9.27) * mm, "end": v(43.31, 9.49) * mm});
            skLineSegment(sketch, "E1189", {"start": v(43.31, 9.49) * mm, "end": v(44.03, 9.71) * mm});
            skLineSegment(sketch, "E1190", {"start": v(44.03, 9.71) * mm, "end": v(44.87, 9.8) * mm});
            skLineSegment(sketch, "E1191", {"start": v(44.87, 9.8) * mm, "end": v(46.12, 9.51) * mm});
            skLineSegment(sketch, "E1192", {"start": v(46.12, 9.51) * mm, "end": v(46.49, 9.17) * mm});
            skLineSegment(sketch, "E1193", {"start": v(46.49, 9.17) * mm, "end": v(46.73, 8.85) * mm});
            skLineSegment(sketch, "E1194", {"start": v(46.73, 8.85) * mm, "end": v(46.73, 8.8) * mm});
            skLineSegment(sketch, "E1195", {"start": v(46.73, 8.8) * mm, "end": v(46.67, 8.45) * mm});
            skLineSegment(sketch, "E1196", {"start": v(46.67, 8.45) * mm, "end": v(46.28, 8.03) * mm});
            skLineSegment(sketch, "E1197", {"start": v(46.28, 8.03) * mm, "end": v(45.88, 7.26) * mm});
            skLineSegment(sketch, "E1198", {"start": v(45.88, 7.26) * mm, "end": v(45.85, 7.08) * mm});
            skLineSegment(sketch, "E1199", {"start": v(45.85, 7.08) * mm, "end": v(45.99, 6.73) * mm});
            skLineSegment(sketch, "E1200", {"start": v(45.99, 6.73) * mm, "end": v(46.28, 6.6) * mm});
            skLineSegment(sketch, "E1201", {"start": v(46.28, 6.6) * mm, "end": v(46.67, 6.55) * mm});
            skLineSegment(sketch, "E1202", {"start": v(46.67, 6.55) * mm, "end": v(47.02, 6.6) * mm});
            skLineSegment(sketch, "E1203", {"start": v(47.02, 6.6) * mm, "end": v(47.41, 6.9) * mm});
            skLineSegment(sketch, "E1204", {"start": v(47.41, 6.9) * mm, "end": v(47.57, 7.18) * mm});
            skLineSegment(sketch, "E1205", {"start": v(47.57, 7.18) * mm, "end": v(47.73, 7.42) * mm});
            skLineSegment(sketch, "E1206", {"start": v(47.73, 7.42) * mm, "end": v(47.76, 7.74) * mm});
            skLineSegment(sketch, "E1207", {"start": v(47.76, 7.74) * mm, "end": v(47.62, 8.64) * mm});
            skLineSegment(sketch, "E1208", {"start": v(47.62, 8.64) * mm, "end": v(47.47, 9.15) * mm});
            skLineSegment(sketch, "E1209", {"start": v(47.47, 9.15) * mm, "end": v(47.23, 9.51) * mm});
            skLineSegment(sketch, "E1210", {"start": v(47.23, 9.51) * mm, "end": v(47.23, 9.56) * mm});
            skLineSegment(sketch, "E1211", {"start": v(47.23, 9.56) * mm, "end": v(46.99, 9.78) * mm});
            skLineSegment(sketch, "E1212", {"start": v(46.99, 9.78) * mm, "end": v(46.89, 9.9) * mm});
            skLineSegment(sketch, "E1213", {"start": v(46.89, 9.9) * mm, "end": v(46.51, 10.15) * mm});
            skLineSegment(sketch, "E1214", {"start": v(46.51, 10.15) * mm, "end": v(45.85, 10.39) * mm});
            skLineSegment(sketch, "E1215", {"start": v(45.85, 10.39) * mm, "end": v(45.14, 10.44) * mm});
            skLineSegment(sketch, "E1216", {"start": v(45.14, 10.44) * mm, "end": v(43.87, 10.44) * mm});
            skLineSegment(sketch, "E1217", {"start": v(43.87, 10.44) * mm, "end": v(43.45, 10.3) * mm});
            skLineSegment(sketch, "E1218", {"start": v(43.45, 10.3) * mm, "end": v(43.07, 10.15) * mm});
            skLineSegment(sketch, "E1219", {"start": v(43.07, 10.15) * mm, "end": v(42.68, 10.04) * mm});
            skLineSegment(sketch, "E1220", {"start": v(42.68, 10.04) * mm, "end": v(42.1, 9.72) * mm});
            skLineSegment(sketch, "E1221", {"start": v(42.1, 9.72) * mm, "end": v(41.86, 9.62) * mm});
            skLineSegment(sketch, "E1222", {"start": v(41.86, 9.62) * mm, "end": v(41.43, 9.27) * mm});
            skLineSegment(sketch, "E1223", {"start": v(41.43, 9.27) * mm, "end": v(40.96, 8.93) * mm});
            skLineSegment(sketch, "E1224", {"start": v(40.96, 8.93) * mm, "end": v(40.24, 8.45) * mm});
            skLineSegment(sketch, "E1225", {"start": v(40.24, 8.45) * mm, "end": v(39.95, 8.32) * mm});
            skLineSegment(sketch, "E1226", {"start": v(39.95, 8.32) * mm, "end": v(39.64, 8.08) * mm});
            skLineSegment(sketch, "E1227", {"start": v(39.64, 8.08) * mm, "end": v(39.21, 7.84) * mm});
            skLineSegment(sketch, "E1228", {"start": v(39.21, 7.84) * mm, "end": v(38.74, 7.5) * mm});
            skLineSegment(sketch, "E1229", {"start": v(38.74, 7.5) * mm, "end": v(38.15, 7) * mm});
            skLineSegment(sketch, "E1230", {"start": v(38.15, 7) * mm, "end": v(37.39, 6.44) * mm});
            skLineSegment(sketch, "E1231", {"start": v(37.39, 6.44) * mm, "end": v(37.23, 6.31) * mm});
            skLineSegment(sketch, "E1232", {"start": v(37.23, 6.31) * mm, "end": v(36.88, 6.12) * mm});
            skLineSegment(sketch, "E1233", {"start": v(36.88, 6.12) * mm, "end": v(36.64, 5.94) * mm});
            skLineSegment(sketch, "E1234", {"start": v(36.64, 5.94) * mm, "end": v(36.27, 5.8) * mm});
            skLineSegment(sketch, "E1235", {"start": v(36.27, 5.8) * mm, "end": v(35.93, 5.62) * mm});
            skLineSegment(sketch, "E1236", {"start": v(35.93, 5.62) * mm, "end": v(34.87, 5.3) * mm});
            skLineSegment(sketch, "E1237", {"start": v(34.87, 5.3) * mm, "end": v(33.84, 4.99) * mm});
            skLineSegment(sketch, "E1238", {"start": v(33.84, 4.99) * mm, "end": v(32.78, 4.99) * mm});
            skLineSegment(sketch, "E1239", {"start": v(32.78, 4.99) * mm, "end": v(31.72, 5.01) * mm});
            skLineSegment(sketch, "E1240", {"start": v(31.72, 5.01) * mm, "end": v(31.25, 5.12) * mm});
            skLineSegment(sketch, "E1241", {"start": v(31.25, 5.12) * mm, "end": v(30.77, 5.23) * mm});
            skLineSegment(sketch, "E1242", {"start": v(30.77, 5.23) * mm, "end": v(30.35, 5.38) * mm});
            skLineSegment(sketch, "E1243", {"start": v(30.35, 5.38) * mm, "end": v(29.85, 5.44) * mm});
            skLineSegment(sketch, "E1244", {"start": v(29.85, 5.44) * mm, "end": v(29.5, 5.6) * mm});
            skLineSegment(sketch, "E1245", {"start": v(29.5, 5.6) * mm, "end": v(28.13, 6.15) * mm});
            skLineSegment(sketch, "E1246", {"start": v(28.13, 6.15) * mm, "end": v(27.78, 6.34) * mm});
            skLineSegment(sketch, "E1247", {"start": v(27.78, 6.34) * mm, "end": v(27.38, 6.68) * mm});
            skLineSegment(sketch, "E1248", {"start": v(27.38, 6.68) * mm, "end": v(26.88, 6.97) * mm});
            skLineSegment(sketch, "E1249", {"start": v(26.88, 6.97) * mm, "end": v(26.64, 7.26) * mm});
            skLineSegment(sketch, "E1250", {"start": v(26.64, 7.26) * mm, "end": v(26.35, 7.48) * mm});
            skLineSegment(sketch, "E1251", {"start": v(26.35, 7.48) * mm, "end": v(26.12, 7.84) * mm});
            skLineSegment(sketch, "E1252", {"start": v(26.12, 7.84) * mm, "end": v(25.9, 8.03) * mm});
            skLineSegment(sketch, "E1253", {"start": v(25.9, 8.03) * mm, "end": v(25.53, 8.37) * mm});
            skLineSegment(sketch, "E1254", {"start": v(25.53, 8.37) * mm, "end": v(24.92, 8.88) * mm});
            skLineSegment(sketch, "E1255", {"start": v(24.92, 8.88) * mm, "end": v(24.2, 9.67) * mm});
            skLineSegment(sketch, "E1256", {"start": v(24.2, 9.67) * mm, "end": v(23.55, 10.57) * mm});
            skLineSegment(sketch, "E1257", {"start": v(23.55, 10.57) * mm, "end": v(22.94, 11.47) * mm});
            skLineSegment(sketch, "E1258", {"start": v(22.94, 11.47) * mm, "end": v(22.41, 12.13) * mm});
            skLineSegment(sketch, "E1259", {"start": v(22.41, 12.13) * mm, "end": v(22.2, 12.32) * mm});
            skLineSegment(sketch, "E1260", {"start": v(22.2, 12.32) * mm, "end": v(21.72, 13.03) * mm});
            skLineSegment(sketch, "E1261", {"start": v(21.72, 13.03) * mm, "end": v(21.67, 13.06) * mm});
            skLineSegment(sketch, "E1262", {"start": v(21.67, 13.06) * mm, "end": v(21.43, 13.43) * mm});
            skLineSegment(sketch, "E1263", {"start": v(21.43, 13.43) * mm, "end": v(21.09, 13.75) * mm});
            skLineSegment(sketch, "E1264", {"start": v(21.09, 13.75) * mm, "end": v(21.2, 13.95) * mm});
            skLineSegment(sketch, "E1265", {"start": v(21.2, 13.95) * mm, "end": v(21.38, 14.1) * mm});
            skLineSegment(sketch, "E1266", {"start": v(21.38, 14.1) * mm, "end": v(22.41, 14.86) * mm});
            skLineSegment(sketch, "E1267", {"start": v(22.41, 14.86) * mm, "end": v(23.47, 15.91) * mm});
            skLineSegment(sketch, "E1268", {"start": v(23.47, 15.91) * mm, "end": v(23.6, 16.05) * mm});
            skLineSegment(sketch, "E1269", {"start": v(23.6, 16.05) * mm, "end": v(23.7, 16.23) * mm});
            skLineSegment(sketch, "E1270", {"start": v(23.7, 16.23) * mm, "end": v(23.73, 16.26) * mm});
            skLineSegment(sketch, "E1271", {"start": v(23.73, 16.26) * mm, "end": v(23.97, 16.66) * mm});
            skLineSegment(sketch, "E1272", {"start": v(23.97, 16.66) * mm, "end": v(24.55, 17.71) * mm});
            skLineSegment(sketch, "E1273", {"start": v(24.55, 17.71) * mm, "end": v(25.22, 19.7) * mm});
            skLineSegment(sketch, "E1274", {"start": v(25.22, 19.7) * mm, "end": v(25.37, 20.23) * mm});
            skLineSegment(sketch, "E1275", {"start": v(25.37, 20.23) * mm, "end": v(25.37, 20.52) * mm});
            skLineSegment(sketch, "E1276", {"start": v(25.37, 20.52) * mm, "end": v(25.4, 20.84) * mm});
            skLineSegment(sketch, "E1277", {"start": v(25.4, 20.84) * mm, "end": v(25.64, 21.92) * mm});
            skLineSegment(sketch, "E1278", {"start": v(25.64, 21.92) * mm, "end": v(25.77, 23.4) * mm});
            skLineSegment(sketch, "E1279", {"start": v(25.77, 23.4) * mm, "end": v(25.77, 24.1) * mm});
            skLineSegment(sketch, "E1280", {"start": v(25.77, 24.1) * mm, "end": v(25.8, 24.38) * mm});
            skLineSegment(sketch, "E1281", {"start": v(25.8, 24.38) * mm, "end": v(26.14, 24.73) * mm});
            skLineSegment(sketch, "E1282", {"start": v(26.14, 24.73) * mm, "end": v(26.51, 24.78) * mm});
            skLineSegment(sketch, "E1283", {"start": v(26.51, 24.78) * mm, "end": v(26.64, 24.78) * mm});
            skLineSegment(sketch, "E1284", {"start": v(26.64, 24.78) * mm, "end": v(26.95, 24.6) * mm});
            skLineSegment(sketch, "E1285", {"start": v(26.95, 24.6) * mm, "end": v(27.2, 24.35) * mm});
            skLineSegment(sketch, "E1286", {"start": v(27.2, 24.35) * mm, "end": v(27.53, 24.08) * mm});
            skLineSegment(sketch, "E1287", {"start": v(27.53, 24.08) * mm, "end": v(27.91, 23.93) * mm});
            skLineSegment(sketch, "E1288", {"start": v(27.91, 23.93) * mm, "end": v(28.13, 24.04) * mm});
            skLineSegment(sketch, "E1289", {"start": v(28.13, 24.04) * mm, "end": v(28.26, 24.38) * mm});
            skLineSegment(sketch, "E1290", {"start": v(28.26, 24.38) * mm, "end": v(28.13, 24.96) * mm});
            skLineSegment(sketch, "E1291", {"start": v(28.13, 24.96) * mm, "end": v(27.38, 25.55) * mm});
            skLineSegment(sketch, "E1292", {"start": v(27.38, 25.55) * mm, "end": v(26.8, 25.76) * mm});
            skLineSegment(sketch, "E1293", {"start": v(26.8, 25.76) * mm, "end": v(26.43, 25.78) * mm});
            skLineSegment(sketch, "E1294", {"start": v(26.43, 25.78) * mm, "end": v(25.3, 25.33) * mm});
            skLineSegment(sketch, "E1295", {"start": v(-12.04, -14.04) * mm, "end": v(-12.36, -13.88) * mm});
            skLineSegment(sketch, "E1296", {"start": v(-12.36, -13.88) * mm, "end": v(-12.62, -13.64) * mm});
            skLineSegment(sketch, "E1297", {"start": v(-12.62, -13.64) * mm, "end": v(-12.83, -13.45) * mm});
            skLineSegment(sketch, "E1298", {"start": v(-12.83, -13.45) * mm, "end": v(-13.39, -12.71) * mm});
            skLineSegment(sketch, "E1299", {"start": v(-13.39, -12.71) * mm, "end": v(-13.73, -12.24) * mm});
            skLineSegment(sketch, "E1300", {"start": v(-13.73, -12.24) * mm, "end": v(-13.86, -11.84) * mm});
            skLineSegment(sketch, "E1301", {"start": v(-13.86, -11.84) * mm, "end": v(-14, -11.5) * mm});
            skLineSegment(sketch, "E1302", {"start": v(-14, -11.5) * mm, "end": v(-14.08, -11.05) * mm});
            skLineSegment(sketch, "E1303", {"start": v(-14.08, -11.05) * mm, "end": v(-14.26, -9.72) * mm});
            skLineSegment(sketch, "E1304", {"start": v(-14.26, -9.72) * mm, "end": v(-14.37, -8.35) * mm});
            skLineSegment(sketch, "E1305", {"start": v(-14.37, -8.35) * mm, "end": v(-14.4, -7.87) * mm});
            skLineSegment(sketch, "E1306", {"start": v(-14.4, -7.87) * mm, "end": v(-14.37, -6.94) * mm});
            skLineSegment(sketch, "E1307", {"start": v(-14.37, -6.94) * mm, "end": v(-14.31, -6.05) * mm});
            skLineSegment(sketch, "E1308", {"start": v(-14.31, -6.05) * mm, "end": v(-14.18, -5.15) * mm});
            skLineSegment(sketch, "E1309", {"start": v(-14.18, -5.15) * mm, "end": v(-14.08, -4.51) * mm});
            skLineSegment(sketch, "E1310", {"start": v(-14.08, -4.51) * mm, "end": v(-14, -4.06) * mm});
            skLineSegment(sketch, "E1311", {"start": v(-14, -4.06) * mm, "end": v(-13.78, -3.06) * mm});
            skLineSegment(sketch, "E1312", {"start": v(-13.78, -3.06) * mm, "end": v(-13.52, -1.76) * mm});
            skLineSegment(sketch, "E1313", {"start": v(-13.52, -1.76) * mm, "end": v(-13.3, -0.97) * mm});
            skLineSegment(sketch, "E1314", {"start": v(-13.3, -0.97) * mm, "end": v(-12.78, 0.54) * mm});
            skLineSegment(sketch, "E1315", {"start": v(-12.78, 0.54) * mm, "end": v(-12.44, 1.26) * mm});
            skLineSegment(sketch, "E1316", {"start": v(-12.44, 1.26) * mm, "end": v(-12.12, 2) * mm});
            skLineSegment(sketch, "E1317", {"start": v(-12.12, 2) * mm, "end": v(-11.7, 2.37) * mm});
            skLineSegment(sketch, "E1318", {"start": v(-11.7, 2.37) * mm, "end": v(-11.03, 2.66) * mm});
            skLineSegment(sketch, "E1319", {"start": v(-11.03, 2.66) * mm, "end": v(-10.69, 2.66) * mm});
            skLineSegment(sketch, "E1320", {"start": v(-10.69, 2.66) * mm, "end": v(-10.21, 2.38) * mm});
            skLineSegment(sketch, "E1321", {"start": v(-10.21, 2.38) * mm, "end": v(-9.82, 1.92) * mm});
            skLineSegment(sketch, "E1322", {"start": v(-9.82, 1.92) * mm, "end": v(-9.42, 1.07) * mm});
            skLineSegment(sketch, "E1323", {"start": v(-9.42, 1.07) * mm, "end": v(-9.13, 0.1) * mm});
            skLineSegment(sketch, "E1324", {"start": v(-9.13, 0.1) * mm, "end": v(-8.76, -1.44) * mm});
            skLineSegment(sketch, "E1325", {"start": v(-8.76, -1.44) * mm, "end": v(-8.7, -1.97) * mm});
            skLineSegment(sketch, "E1326", {"start": v(-8.7, -1.97) * mm, "end": v(-8.55, -2.55) * mm});
            skLineSegment(sketch, "E1327", {"start": v(-8.55, -2.55) * mm, "end": v(-8.55, -2.9) * mm});
            skLineSegment(sketch, "E1328", {"start": v(-8.55, -2.9) * mm, "end": v(-8.52, -3.21) * mm});
            skLineSegment(sketch, "E1329", {"start": v(-8.52, -3.21) * mm, "end": v(-8.44, -3.77) * mm});
            skLineSegment(sketch, "E1330", {"start": v(-8.44, -3.77) * mm, "end": v(-8.44, -4.38) * mm});
            skLineSegment(sketch, "E1331", {"start": v(-8.44, -4.38) * mm, "end": v(-8.36, -4.93) * mm});
            skLineSegment(sketch, "E1332", {"start": v(-8.36, -4.93) * mm, "end": v(-8.36, -5.1) * mm});
            skLineSegment(sketch, "E1333", {"start": v(-8.36, -5.1) * mm, "end": v(-8.39, -5.73) * mm});
            skLineSegment(sketch, "E1334", {"start": v(-8.39, -5.73) * mm, "end": v(-8.39, -5.89) * mm});
            skLineSegment(sketch, "E1335", {"start": v(-8.39, -5.89) * mm, "end": v(-8.36, -6.52) * mm});
            skLineSegment(sketch, "E1336", {"start": v(-8.36, -6.52) * mm, "end": v(-8.39, -7.08) * mm});
            skLineSegment(sketch, "E1337", {"start": v(-8.39, -7.08) * mm, "end": v(-8.41, -7.63) * mm});
            skLineSegment(sketch, "E1338", {"start": v(-8.41, -7.63) * mm, "end": v(-8.41, -8.16) * mm});
            skLineSegment(sketch, "E1339", {"start": v(-8.41, -8.16) * mm, "end": v(-8.73, -10.73) * mm});
            skLineSegment(sketch, "E1340", {"start": v(-8.73, -10.73) * mm, "end": v(-8.78, -11.23) * mm});
            skLineSegment(sketch, "E1341", {"start": v(-8.78, -11.23) * mm, "end": v(-9.15, -12.1) * mm});
            skLineSegment(sketch, "E1342", {"start": v(-9.15, -12.1) * mm, "end": v(-9.2, -12.18) * mm});
            skLineSegment(sketch, "E1343", {"start": v(-9.2, -12.18) * mm, "end": v(-9.7, -13.06) * mm});
            skLineSegment(sketch, "E1344", {"start": v(-9.7, -13.06) * mm, "end": v(-10.1, -13.43) * mm});
            skLineSegment(sketch, "E1345", {"start": v(-10.1, -13.43) * mm, "end": v(-10.53, -13.77) * mm});
            skLineSegment(sketch, "E1346", {"start": v(-10.53, -13.77) * mm, "end": v(-11.05, -13.9) * mm});
            skLineSegment(sketch, "E1347", {"start": v(-11.05, -13.9) * mm, "end": v(-11.75, -13.96) * mm});
            skLineSegment(sketch, "E1348", {"start": v(-11.75, -13.96) * mm, "end": v(-12.04, -14.04) * mm});
            skLineSegment(sketch, "E1349", {"start": v(-12.17, 2.85) * mm, "end": v(-12.94, 2.34) * mm});
            skLineSegment(sketch, "E1350", {"start": v(-12.94, 2.34) * mm, "end": v(-13.47, 1.79) * mm});
            skLineSegment(sketch, "E1351", {"start": v(-13.47, 1.79) * mm, "end": v(-14.02, 0.91) * mm});
            skLineSegment(sketch, "E1352", {"start": v(-14.02, 0.91) * mm, "end": v(-14.34, 0.28) * mm});
            skLineSegment(sketch, "E1353", {"start": v(-14.34, 0.28) * mm, "end": v(-14.66, -0.33) * mm});
            skLineSegment(sketch, "E1354", {"start": v(-14.66, -0.33) * mm, "end": v(-15.13, -1.76) * mm});
            skLineSegment(sketch, "E1355", {"start": v(-15.13, -1.76) * mm, "end": v(-15.32, -2.53) * mm});
            skLineSegment(sketch, "E1356", {"start": v(-15.32, -2.53) * mm, "end": v(-15.48, -3.32) * mm});
            skLineSegment(sketch, "E1357", {"start": v(-15.48, -3.32) * mm, "end": v(-15.56, -4.11) * mm});
            skLineSegment(sketch, "E1358", {"start": v(-15.56, -4.11) * mm, "end": v(-15.69, -4.86) * mm});
            skLineSegment(sketch, "E1359", {"start": v(-15.69, -4.86) * mm, "end": v(-15.74, -5.68) * mm});
            skLineSegment(sketch, "E1360", {"start": v(-15.74, -5.68) * mm, "end": v(-15.8, -6.5) * mm});
            skLineSegment(sketch, "E1361", {"start": v(-15.8, -6.5) * mm, "end": v(-15.85, -7.8) * mm});
            skLineSegment(sketch, "E1362", {"start": v(-15.85, -7.8) * mm, "end": v(-15.74, -9.86) * mm});
            skLineSegment(sketch, "E1363", {"start": v(-15.74, -9.86) * mm, "end": v(-15.64, -10.62) * mm});
            skLineSegment(sketch, "E1364", {"start": v(-15.64, -10.62) * mm, "end": v(-15.3, -12.03) * mm});
            skLineSegment(sketch, "E1365", {"start": v(-15.3, -12.03) * mm, "end": v(-15, -12.63) * mm});
            skLineSegment(sketch, "E1366", {"start": v(-15, -12.63) * mm, "end": v(-14.68, -13.19) * mm});
            skLineSegment(sketch, "E1367", {"start": v(-14.68, -13.19) * mm, "end": v(-13.84, -14.09) * mm});
            skLineSegment(sketch, "E1368", {"start": v(-13.84, -14.09) * mm, "end": v(-13.12, -14.51) * mm});
            skLineSegment(sketch, "E1369", {"start": v(-13.12, -14.51) * mm, "end": v(-12.14, -14.65) * mm});
            skLineSegment(sketch, "E1370", {"start": v(-12.14, -14.65) * mm, "end": v(-11.67, -14.62) * mm});
            skLineSegment(sketch, "E1371", {"start": v(-11.67, -14.62) * mm, "end": v(-11, -14.46) * mm});
            skLineSegment(sketch, "E1372", {"start": v(-11, -14.46) * mm, "end": v(-10.37, -14.3) * mm});
            skLineSegment(sketch, "E1373", {"start": v(-10.37, -14.3) * mm, "end": v(-9.87, -13.88) * mm});
            skLineSegment(sketch, "E1374", {"start": v(-9.87, -13.88) * mm, "end": v(-9.42, -13.43) * mm});
            skLineSegment(sketch, "E1375", {"start": v(-9.42, -13.43) * mm, "end": v(-9.13, -12.95) * mm});
            skLineSegment(sketch, "E1376", {"start": v(-9.13, -12.95) * mm, "end": v(-9.02, -12.8) * mm});
            skLineSegment(sketch, "E1377", {"start": v(-9.02, -12.8) * mm, "end": v(-8.68, -12.08) * mm});
            skLineSegment(sketch, "E1378", {"start": v(-8.68, -12.08) * mm, "end": v(-8.36, -11.34) * mm});
            skLineSegment(sketch, "E1379", {"start": v(-8.36, -11.34) * mm, "end": v(-8.07, -10.54) * mm});
            skLineSegment(sketch, "E1380", {"start": v(-8.07, -10.54) * mm, "end": v(-7.94, -9.93) * mm});
            skLineSegment(sketch, "E1381", {"start": v(-7.94, -9.93) * mm, "end": v(-7.78, -9.33) * mm});
            skLineSegment(sketch, "E1382", {"start": v(-7.78, -9.33) * mm, "end": v(-7.73, -8.82) * mm});
            skLineSegment(sketch, "E1383", {"start": v(-7.73, -8.82) * mm, "end": v(-7.62, -8.35) * mm});
            skLineSegment(sketch, "E1384", {"start": v(-7.62, -8.35) * mm, "end": v(-7.57, -7.84) * mm});
            skLineSegment(sketch, "E1385", {"start": v(-7.57, -7.84) * mm, "end": v(-7.49, -7.37) * mm});
            skLineSegment(sketch, "E1386", {"start": v(-7.49, -7.37) * mm, "end": v(-7.49, -6.52) * mm});
            skLineSegment(sketch, "E1387", {"start": v(-7.49, -6.52) * mm, "end": v(-7.4, -6.18) * mm});
            skLineSegment(sketch, "E1388", {"start": v(-7.4, -6.18) * mm, "end": v(-7.38, -5.78) * mm});
            skLineSegment(sketch, "E1389", {"start": v(-7.38, -5.78) * mm, "end": v(-7.3, -5.01) * mm});
            skLineSegment(sketch, "E1390", {"start": v(-7.3, -5.01) * mm, "end": v(-7.49, -3.1) * mm});
            skLineSegment(sketch, "E1391", {"start": v(-7.49, -3.1) * mm, "end": v(-7.83, -1.36) * mm});
            skLineSegment(sketch, "E1392", {"start": v(-7.83, -1.36) * mm, "end": v(-8.18, -0.28) * mm});
            skLineSegment(sketch, "E1393", {"start": v(-8.18, -0.28) * mm, "end": v(-8.2, -0.2) * mm});
            skLineSegment(sketch, "E1394", {"start": v(-8.2, -0.2) * mm, "end": v(-8.39, 0.33) * mm});
            skLineSegment(sketch, "E1395", {"start": v(-8.39, 0.33) * mm, "end": v(-8.78, 1.36) * mm});
            skLineSegment(sketch, "E1396", {"start": v(-8.78, 1.36) * mm, "end": v(-9.29, 2.13) * mm});
            skLineSegment(sketch, "E1397", {"start": v(-9.29, 2.13) * mm, "end": v(-9.81, 2.65) * mm});
            skLineSegment(sketch, "E1398", {"start": v(-9.81, 2.65) * mm, "end": v(-10.53, 2.98) * mm});
            skLineSegment(sketch, "E1399", {"start": v(-10.53, 2.98) * mm, "end": v(-11, 3.03) * mm});
            skLineSegment(sketch, "E1400", {"start": v(-11, 3.03) * mm, "end": v(-11.65, 3) * mm});
            skLineSegment(sketch, "E1401", {"start": v(-11.65, 3) * mm, "end": v(-12.17, 2.85) * mm});
            skLineSegment(sketch, "E1402", {"start": v(-1.11, 3.35) * mm, "end": v(-1.42, 3.27) * mm});
            skLineSegment(sketch, "E1403", {"start": v(-1.42, 3.27) * mm, "end": v(-1.56, 3.06) * mm});
            skLineSegment(sketch, "E1404", {"start": v(-1.56, 3.06) * mm, "end": v(-1.47, 2.87) * mm});
            skLineSegment(sketch, "E1405", {"start": v(-1.47, 2.87) * mm, "end": v(-1.22, 2.82) * mm});
            skLineSegment(sketch, "E1406", {"start": v(-1.22, 2.82) * mm, "end": v(-0.77, 2.85) * mm});
            skLineSegment(sketch, "E1407", {"start": v(-0.77, 2.85) * mm, "end": v(-0.69, 2.85) * mm});
            skLineSegment(sketch, "E1408", {"start": v(-0.69, 2.85) * mm, "end": v(-0.69, 2.58) * mm});
            skLineSegment(sketch, "E1409", {"start": v(-0.69, 2.58) * mm, "end": v(-0.77, 1.05) * mm});
            skLineSegment(sketch, "E1410", {"start": v(-0.77, 1.05) * mm, "end": v(-0.8, 0.38) * mm});
            skLineSegment(sketch, "E1411", {"start": v(-0.8, 0.38) * mm, "end": v(-0.77, -0.97) * mm});
            skLineSegment(sketch, "E1412", {"start": v(-0.77, -0.97) * mm, "end": v(-0.77, -5.75) * mm});
            skLineSegment(sketch, "E1413", {"start": v(-0.77, -5.75) * mm, "end": v(-0.82, -6.39) * mm});
            skLineSegment(sketch, "E1414", {"start": v(-0.82, -6.39) * mm, "end": v(-0.77, -7.71) * mm});
            skLineSegment(sketch, "E1415", {"start": v(-0.77, -7.71) * mm, "end": v(-0.71, -8.35) * mm});
            skLineSegment(sketch, "E1416", {"start": v(-0.71, -8.35) * mm, "end": v(-0.66, -8.98) * mm});
            skLineSegment(sketch, "E1417", {"start": v(-0.66, -8.98) * mm, "end": v(-0.66, -9.64) * mm});
            skLineSegment(sketch, "E1418", {"start": v(-0.66, -9.64) * mm, "end": v(-0.58, -10.38) * mm});
            skLineSegment(sketch, "E1419", {"start": v(-0.58, -10.38) * mm, "end": v(-0.53, -11.2) * mm});
            skLineSegment(sketch, "E1420", {"start": v(-0.53, -11.2) * mm, "end": v(-0.64, -12.03) * mm});
            skLineSegment(sketch, "E1421", {"start": v(-0.64, -12.03) * mm, "end": v(-0.82, -12.5) * mm});
            skLineSegment(sketch, "E1422", {"start": v(-0.82, -12.5) * mm, "end": v(-1.02, -12.9) * mm});
            skLineSegment(sketch, "E1423", {"start": v(-1.02, -12.9) * mm, "end": v(-1.3, -13.16) * mm});
            skLineSegment(sketch, "E1424", {"start": v(-1.3, -13.16) * mm, "end": v(-1.32, -13.19) * mm});
            skLineSegment(sketch, "E1425", {"start": v(-1.32, -13.19) * mm, "end": v(-1.8, -13.56) * mm});
            skLineSegment(sketch, "E1426", {"start": v(-1.8, -13.56) * mm, "end": v(-2.2, -13.61) * mm});
            skLineSegment(sketch, "E1427", {"start": v(-2.2, -13.61) * mm, "end": v(-2.6, -13.67) * mm});
            skLineSegment(sketch, "E1428", {"start": v(-2.6, -13.67) * mm, "end": v(-2.86, -13.64) * mm});
            skLineSegment(sketch, "E1429", {"start": v(-2.86, -13.64) * mm, "end": v(-3.12, -13.56) * mm});
            skLineSegment(sketch, "E1430", {"start": v(-3.12, -13.56) * mm, "end": v(-3.47, -13.3) * mm});
            skLineSegment(sketch, "E1431", {"start": v(-3.47, -13.3) * mm, "end": v(-3.6, -12.85) * mm});
            skLineSegment(sketch, "E1432", {"start": v(-3.6, -12.85) * mm, "end": v(-3.7, -12.45) * mm});
            skLineSegment(sketch, "E1433", {"start": v(-3.7, -12.45) * mm, "end": v(-3.73, -12.24) * mm});
            skLineSegment(sketch, "E1434", {"start": v(-3.73, -12.24) * mm, "end": v(-3.73, -12) * mm});
            skLineSegment(sketch, "E1435", {"start": v(-3.73, -12) * mm, "end": v(-3.76, -11.81) * mm});
            skLineSegment(sketch, "E1436", {"start": v(-3.76, -11.81) * mm, "end": v(-3.76, -11.6) * mm});
            skLineSegment(sketch, "E1437", {"start": v(-3.76, -11.6) * mm, "end": v(-3.84, -11.28) * mm});
            skLineSegment(sketch, "E1438", {"start": v(-3.84, -11.28) * mm, "end": v(-3.84, -11) * mm});
            skLineSegment(sketch, "E1439", {"start": v(-3.84, -11) * mm, "end": v(-3.86, -10.83) * mm});
            skLineSegment(sketch, "E1440", {"start": v(-3.86, -10.83) * mm, "end": v(-3.86, -10.68) * mm});
            skLineSegment(sketch, "E1441", {"start": v(-3.86, -10.68) * mm, "end": v(-4, -9.96) * mm});
            skLineSegment(sketch, "E1442", {"start": v(-4, -9.96) * mm, "end": v(-4.05, -8.7) * mm});
            skLineSegment(sketch, "E1443", {"start": v(-4.05, -8.7) * mm, "end": v(-4.15, -8.06) * mm});
            skLineSegment(sketch, "E1444", {"start": v(-4.15, -8.06) * mm, "end": v(-4.15, -7.16) * mm});
            skLineSegment(sketch, "E1445", {"start": v(-4.15, -7.16) * mm, "end": v(-4.18, -6.26) * mm});
            skLineSegment(sketch, "E1446", {"start": v(-4.18, -6.26) * mm, "end": v(-4.23, -2.74) * mm});
            skLineSegment(sketch, "E1447", {"start": v(-4.23, -2.74) * mm, "end": v(-4.31, -1.07) * mm});
            skLineSegment(sketch, "E1448", {"start": v(-4.31, -1.07) * mm, "end": v(-4.29, -0.75) * mm});
            skLineSegment(sketch, "E1449", {"start": v(-4.29, -0.75) * mm, "end": v(-4.34, 0.25) * mm});
            skLineSegment(sketch, "E1450", {"start": v(-4.34, 0.25) * mm, "end": v(-4.37, 0.52) * mm});
            skLineSegment(sketch, "E1451", {"start": v(-4.37, 0.52) * mm, "end": v(-4.37, 0.78) * mm});
            skLineSegment(sketch, "E1452", {"start": v(-4.37, 0.78) * mm, "end": v(-4.42, 1.28) * mm});
            skLineSegment(sketch, "E1453", {"start": v(-4.42, 1.28) * mm, "end": v(-4.37, 1.57) * mm});
            skLineSegment(sketch, "E1454", {"start": v(-4.37, 1.57) * mm, "end": v(-4.37, 1.73) * mm});
            skLineSegment(sketch, "E1455", {"start": v(-4.37, 1.73) * mm, "end": v(-4.34, 1.87) * mm});
            skLineSegment(sketch, "E1456", {"start": v(-4.34, 1.87) * mm, "end": v(-4.23, 2.47) * mm});
            skLineSegment(sketch, "E1457", {"start": v(-4.23, 2.47) * mm, "end": v(-3.99, 2.7) * mm});
            skLineSegment(sketch, "E1458", {"start": v(-3.99, 2.7) * mm, "end": v(-3.6, 2.82) * mm});
            skLineSegment(sketch, "E1459", {"start": v(-3.6, 2.82) * mm, "end": v(-3.3, 2.82) * mm});
            skLineSegment(sketch, "E1460", {"start": v(-3.3, 2.82) * mm, "end": v(-3.1, 3) * mm});
            skLineSegment(sketch, "E1461", {"start": v(-3.1, 3) * mm, "end": v(-3.2, 3.2) * mm});
            skLineSegment(sketch, "E1462", {"start": v(-3.2, 3.2) * mm, "end": v(-3.5, 3.27) * mm});
            skLineSegment(sketch, "E1463", {"start": v(-3.5, 3.27) * mm, "end": v(-4.23, 3.19) * mm});
            skLineSegment(sketch, "E1464", {"start": v(-4.23, 3.19) * mm, "end": v(-4.55, 3.27) * mm});
            skLineSegment(sketch, "E1465", {"start": v(-4.55, 3.27) * mm, "end": v(-4.6, 3.27) * mm});
            skLineSegment(sketch, "E1466", {"start": v(-4.6, 3.27) * mm, "end": v(-4.9, 3.24) * mm});
            skLineSegment(sketch, "E1467", {"start": v(-4.9, 3.24) * mm, "end": v(-4.92, 3.3) * mm});
            skLineSegment(sketch, "E1468", {"start": v(-4.92, 3.3) * mm, "end": v(-5.08, 3.32) * mm});
            skLineSegment(sketch, "E1469", {"start": v(-5.08, 3.32) * mm, "end": v(-5.66, 3.24) * mm});
            skLineSegment(sketch, "E1470", {"start": v(-5.66, 3.24) * mm, "end": v(-6.38, 3.1) * mm});
            skLineSegment(sketch, "E1471", {"start": v(-6.38, 3.1) * mm, "end": v(-6.67, 3.14) * mm});
            skLineSegment(sketch, "E1472", {"start": v(-6.67, 3.14) * mm, "end": v(-6.9, 2.98) * mm});
            skLineSegment(sketch, "E1473", {"start": v(-6.9, 2.98) * mm, "end": v(-6.9, 2.95) * mm});
            skLineSegment(sketch, "E1474", {"start": v(-6.9, 2.95) * mm, "end": v(-6.7, 2.77) * mm});
            skLineSegment(sketch, "E1475", {"start": v(-6.7, 2.77) * mm, "end": v(-6.24, 2.74) * mm});
            skLineSegment(sketch, "E1476", {"start": v(-6.24, 2.74) * mm, "end": v(-5.8, 2.71) * mm});
            skLineSegment(sketch, "E1477", {"start": v(-5.8, 2.71) * mm, "end": v(-5.74, 2.4) * mm});
            skLineSegment(sketch, "E1478", {"start": v(-5.74, 2.4) * mm, "end": v(-5.77, 1.92) * mm});
            skLineSegment(sketch, "E1479", {"start": v(-5.77, 1.92) * mm, "end": v(-5.77, 1.79) * mm});
            skLineSegment(sketch, "E1480", {"start": v(-5.77, 1.79) * mm, "end": v(-5.69, 1.4) * mm});
            skLineSegment(sketch, "E1481", {"start": v(-5.69, 1.4) * mm, "end": v(-5.69, 1.18) * mm});
            skLineSegment(sketch, "E1482", {"start": v(-5.69, 1.18) * mm, "end": v(-5.74, 0.15) * mm});
            skLineSegment(sketch, "E1483", {"start": v(-5.74, 0.15) * mm, "end": v(-5.74, -0.12) * mm});
            skLineSegment(sketch, "E1484", {"start": v(-5.74, -0.12) * mm, "end": v(-5.71, -1.05) * mm});
            skLineSegment(sketch, "E1485", {"start": v(-5.71, -1.05) * mm, "end": v(-5.71, -1.23) * mm});
            skLineSegment(sketch, "E1486", {"start": v(-5.71, -1.23) * mm, "end": v(-5.77, -2.18) * mm});
            skLineSegment(sketch, "E1487", {"start": v(-5.77, -2.18) * mm, "end": v(-5.77, -2.4) * mm});
            skLineSegment(sketch, "E1488", {"start": v(-5.77, -2.4) * mm, "end": v(-5.71, -2.8) * mm});
            skLineSegment(sketch, "E1489", {"start": v(-5.71, -2.8) * mm, "end": v(-5.71, -3.82) * mm});
            skLineSegment(sketch, "E1490", {"start": v(-5.71, -3.82) * mm, "end": v(-5.66, -4.38) * mm});
            skLineSegment(sketch, "E1491", {"start": v(-5.66, -4.38) * mm, "end": v(-5.66, -4.56) * mm});
            skLineSegment(sketch, "E1492", {"start": v(-5.66, -4.56) * mm, "end": v(-5.69, -5.41) * mm});
            skLineSegment(sketch, "E1493", {"start": v(-5.69, -5.41) * mm, "end": v(-5.66, -6.47) * mm});
            skLineSegment(sketch, "E1494", {"start": v(-5.66, -6.47) * mm, "end": v(-5.69, -8.64) * mm});
            skLineSegment(sketch, "E1495", {"start": v(-5.69, -8.64) * mm, "end": v(-5.69, -10.65) * mm});
            skLineSegment(sketch, "E1496", {"start": v(-5.69, -10.65) * mm, "end": v(-5.63, -11.7) * mm});
            skLineSegment(sketch, "E1497", {"start": v(-5.63, -11.7) * mm, "end": v(-5.42, -12.66) * mm});
            skLineSegment(sketch, "E1498", {"start": v(-5.42, -12.66) * mm, "end": v(-5.27, -13.14) * mm});
            skLineSegment(sketch, "E1499", {"start": v(-5.27, -13.14) * mm, "end": v(-5.08, -13.61) * mm});
            skLineSegment(sketch, "E1500", {"start": v(-5.08, -13.61) * mm, "end": v(-4.69, -13.99) * mm});
            skLineSegment(sketch, "E1501", {"start": v(-4.69, -13.99) * mm, "end": v(-4.1, -14.17) * mm});
            skLineSegment(sketch, "E1502", {"start": v(-4.1, -14.17) * mm, "end": v(-3.62, -14.22) * mm});
            skLineSegment(sketch, "E1503", {"start": v(-3.62, -14.22) * mm, "end": v(-3.28, -14.25) * mm});
            skLineSegment(sketch, "E1504", {"start": v(-3.28, -14.25) * mm, "end": v(-2.54, -14.17) * mm});
            skLineSegment(sketch, "E1505", {"start": v(-2.54, -14.17) * mm, "end": v(-2.17, -14.09) * mm});
            skLineSegment(sketch, "E1506", {"start": v(-2.17, -14.09) * mm, "end": v(-1.72, -13.93) * mm});
            skLineSegment(sketch, "E1507", {"start": v(-1.72, -13.93) * mm, "end": v(-1.24, -13.59) * mm});
            skLineSegment(sketch, "E1508", {"start": v(-1.24, -13.59) * mm, "end": v(-1.03, -13.37) * mm});
            skLineSegment(sketch, "E1509", {"start": v(-1.03, -13.37) * mm, "end": v(-0.88, -13.1) * mm});
            skLineSegment(sketch, "E1510", {"start": v(-0.88, -13.1) * mm, "end": v(-0.69, -12.9) * mm});
            skLineSegment(sketch, "E1511", {"start": v(-0.69, -12.9) * mm, "end": v(-0.4, -12.42) * mm});
            skLineSegment(sketch, "E1512", {"start": v(-0.4, -12.42) * mm, "end": v(-0.32, -12.82) * mm});
            skLineSegment(sketch, "E1513", {"start": v(-0.32, -12.82) * mm, "end": v(-0.05, -13.48) * mm});
            skLineSegment(sketch, "E1514", {"start": v(-0.05, -13.48) * mm, "end": v(0.11, -13.64) * mm});
            skLineSegment(sketch, "E1515", {"start": v(0.11, -13.64) * mm, "end": v(0.24, -13.82) * mm});
            skLineSegment(sketch, "E1516", {"start": v(0.24, -13.82) * mm, "end": v(0.73, -14.13) * mm});
            skLineSegment(sketch, "E1517", {"start": v(0.73, -14.13) * mm, "end": v(1.35, -14.3) * mm});
            skLineSegment(sketch, "E1518", {"start": v(1.35, -14.3) * mm, "end": v(1.54, -14.3) * mm});
            skLineSegment(sketch, "E1519", {"start": v(1.54, -14.3) * mm, "end": v(2.01, -14.14) * mm});
            skLineSegment(sketch, "E1520", {"start": v(2.01, -14.14) * mm, "end": v(2.51, -13.96) * mm});
            skLineSegment(sketch, "E1521", {"start": v(2.51, -13.96) * mm, "end": v(2.78, -13.82) * mm});
            skLineSegment(sketch, "E1522", {"start": v(2.78, -13.82) * mm, "end": v(3.04, -13.67) * mm});
            skLineSegment(sketch, "E1523", {"start": v(3.04, -13.67) * mm, "end": v(3.23, -13.3) * mm});
            skLineSegment(sketch, "E1524", {"start": v(3.23, -13.3) * mm, "end": v(3.39, -12.87) * mm});
            skLineSegment(sketch, "E1525", {"start": v(3.39, -12.87) * mm, "end": v(3.41, -12.66) * mm});
            skLineSegment(sketch, "E1526", {"start": v(3.41, -12.66) * mm, "end": v(3.36, -12.42) * mm});
            skLineSegment(sketch, "E1527", {"start": v(3.36, -12.42) * mm, "end": v(3.02, -12.29) * mm});
            skLineSegment(sketch, "E1528", {"start": v(3.02, -12.29) * mm, "end": v(2.83, -12.32) * mm});
            skLineSegment(sketch, "E1529", {"start": v(2.83, -12.32) * mm, "end": v(2.32, -12.47) * mm});
            skLineSegment(sketch, "E1530", {"start": v(2.32, -12.47) * mm, "end": v(2.1, -12.85) * mm});
            skLineSegment(sketch, "E1531", {"start": v(2.1, -12.85) * mm, "end": v(2.1, -13.22) * mm});
            skLineSegment(sketch, "E1532", {"start": v(2.1, -13.22) * mm, "end": v(1.97, -13.58) * mm});
            skLineSegment(sketch, "E1533", {"start": v(1.97, -13.58) * mm, "end": v(1.72, -13.8) * mm});
            skLineSegment(sketch, "E1534", {"start": v(1.72, -13.8) * mm, "end": v(1.39, -13.68) * mm});
            skLineSegment(sketch, "E1535", {"start": v(1.39, -13.68) * mm, "end": v(1.11, -13.45) * mm});
            skLineSegment(sketch, "E1536", {"start": v(1.11, -13.45) * mm, "end": v(0.98, -13.19) * mm});
            skLineSegment(sketch, "E1537", {"start": v(0.98, -13.19) * mm, "end": v(0.85, -12.93) * mm});
            skLineSegment(sketch, "E1538", {"start": v(0.85, -12.93) * mm, "end": v(0.74, -12.6) * mm});
            skLineSegment(sketch, "E1539", {"start": v(0.74, -12.6) * mm, "end": v(0.6, -12.32) * mm});
            skLineSegment(sketch, "E1540", {"start": v(0.6, -12.32) * mm, "end": v(0.56, -11.95) * mm});
            skLineSegment(sketch, "E1541", {"start": v(0.56, -11.95) * mm, "end": v(0.34, -11.28) * mm});
            skLineSegment(sketch, "E1542", {"start": v(0.34, -11.28) * mm, "end": v(0.34, -10.89) * mm});
            skLineSegment(sketch, "E1543", {"start": v(0.34, -10.89) * mm, "end": v(0.32, -10.5) * mm});
            skLineSegment(sketch, "E1544", {"start": v(0.32, -10.5) * mm, "end": v(0.32, -10.36) * mm});
            skLineSegment(sketch, "E1545", {"start": v(0.32, -10.36) * mm, "end": v(0.34, -9.72) * mm});
            skLineSegment(sketch, "E1546", {"start": v(0.34, -9.72) * mm, "end": v(0.32, -9.14) * mm});
            skLineSegment(sketch, "E1547", {"start": v(0.32, -9.14) * mm, "end": v(0.3, -8.82) * mm});
            skLineSegment(sketch, "E1548", {"start": v(0.3, -8.82) * mm, "end": v(0.32, -8.5) * mm});
            skLineSegment(sketch, "E1549", {"start": v(0.32, -8.5) * mm, "end": v(0.26, -7.34) * mm});
            skLineSegment(sketch, "E1550", {"start": v(0.26, -7.34) * mm, "end": v(0.26, -7.08) * mm});
            skLineSegment(sketch, "E1551", {"start": v(0.26, -7.08) * mm, "end": v(0.34, -5.15) * mm});
            skLineSegment(sketch, "E1552", {"start": v(0.34, -5.15) * mm, "end": v(0.3, -2.82) * mm});
            skLineSegment(sketch, "E1553", {"start": v(0.3, -2.82) * mm, "end": v(0.21, -1.65) * mm});
            skLineSegment(sketch, "E1554", {"start": v(0.21, -1.65) * mm, "end": v(0.21, 0.46) * mm});
            skLineSegment(sketch, "E1555", {"start": v(0.21, 0.46) * mm, "end": v(0.32, 1.2) * mm});
            skLineSegment(sketch, "E1556", {"start": v(0.32, 1.2) * mm, "end": v(0.32, 1.68) * mm});
            skLineSegment(sketch, "E1557", {"start": v(0.32, 1.68) * mm, "end": v(0.34, 2.16) * mm});
            skLineSegment(sketch, "E1558", {"start": v(0.34, 2.16) * mm, "end": v(0.46, 2.61) * mm});
            skLineSegment(sketch, "E1559", {"start": v(0.46, 2.61) * mm, "end": v(0.69, 2.92) * mm});
            skLineSegment(sketch, "E1560", {"start": v(0.69, 2.92) * mm, "end": v(1.07, 3.01) * mm});
            skLineSegment(sketch, "E1561", {"start": v(1.07, 3.01) * mm, "end": v(1.32, 3.24) * mm});
            skLineSegment(sketch, "E1562", {"start": v(1.32, 3.24) * mm, "end": v(1.32, 3.3) * mm});
            skLineSegment(sketch, "E1563", {"start": v(1.32, 3.3) * mm, "end": v(1.14, 3.4) * mm});
            skLineSegment(sketch, "E1564", {"start": v(1.14, 3.4) * mm, "end": v(0.8, 3.43) * mm});
            skLineSegment(sketch, "E1565", {"start": v(0.8, 3.43) * mm, "end": v(0.19, 3.4) * mm});
            skLineSegment(sketch, "E1566", {"start": v(0.19, 3.4) * mm, "end": v(-0.98, 3.5) * mm});
            skLineSegment(sketch, "E1567", {"start": v(-0.98, 3.5) * mm, "end": v(-1.11, 3.5) * mm});
            skLineSegment(sketch, "E1568", {"start": v(-1.11, 3.5) * mm, "end": v(-1.11, 3.35) * mm});
            skLineSegment(sketch, "E1569", {"start": v(-1.59, 24.38) * mm, "end": v(-1.22, 24.06) * mm});
            skLineSegment(sketch, "E1570", {"start": v(-1.22, 24.06) * mm, "end": v(-0.87, 23.67) * mm});
            skLineSegment(sketch, "E1571", {"start": v(-0.87, 23.67) * mm, "end": v(-0.48, 23.11) * mm});
            skLineSegment(sketch, "E1572", {"start": v(-0.48, 23.11) * mm, "end": v(-0.38, 22.74) * mm});
            skLineSegment(sketch, "E1573", {"start": v(-0.38, 22.74) * mm, "end": v(-0.32, 22.26) * mm});
            skLineSegment(sketch, "E1574", {"start": v(-0.32, 22.26) * mm, "end": v(-0.3, 21.37) * mm});
            skLineSegment(sketch, "E1575", {"start": v(-0.3, 21.37) * mm, "end": v(-0.24, 19.57) * mm});
            skLineSegment(sketch, "E1576", {"start": v(-0.24, 19.57) * mm, "end": v(-0.24, 17.71) * mm});
            skLineSegment(sketch, "E1577", {"start": v(-0.24, 17.71) * mm, "end": v(-0.18, 16.81) * mm});
            skLineSegment(sketch, "E1578", {"start": v(-0.18, 16.81) * mm, "end": v(-0.18, 15.86) * mm});
            skLineSegment(sketch, "E1579", {"start": v(-0.18, 15.86) * mm, "end": v(-0.08, 14.7) * mm});
            skLineSegment(sketch, "E1580", {"start": v(-0.08, 14.7) * mm, "end": v(-0.08, 13.53) * mm});
            skLineSegment(sketch, "E1581", {"start": v(-0.08, 13.53) * mm, "end": v(-0.05, 12.32) * mm});
            skLineSegment(sketch, "E1582", {"start": v(-0.05, 12.32) * mm, "end": v(-0.08, 9.9) * mm});
            skLineSegment(sketch, "E1583", {"start": v(-0.08, 9.9) * mm, "end": v(-0.05, 8.82) * mm});
            skLineSegment(sketch, "E1584", {"start": v(-0.05, 8.82) * mm, "end": v(-0.08, 7.66) * mm});
            skLineSegment(sketch, "E1585", {"start": v(-0.08, 7.66) * mm, "end": v(-0.08, 7.63) * mm});
            skLineSegment(sketch, "E1586", {"start": v(-0.08, 7.63) * mm, "end": v(-0.14, 7.04) * mm});
            skLineSegment(sketch, "E1587", {"start": v(-0.14, 7.04) * mm, "end": v(-0.3, 6.63) * mm});
            skLineSegment(sketch, "E1588", {"start": v(-0.3, 6.63) * mm, "end": v(-0.58, 6.47) * mm});
            skLineSegment(sketch, "E1589", {"start": v(-0.58, 6.47) * mm, "end": v(-1.11, 6.34) * mm});
            skLineSegment(sketch, "E1590", {"start": v(-1.11, 6.34) * mm, "end": v(-1.22, 6.34) * mm});
            skLineSegment(sketch, "E1591", {"start": v(-1.22, 6.34) * mm, "end": v(-1.75, 6.47) * mm});
            skLineSegment(sketch, "E1592", {"start": v(-1.75, 6.47) * mm, "end": v(-2.06, 6.47) * mm});
            skLineSegment(sketch, "E1593", {"start": v(-2.06, 6.47) * mm, "end": v(-2.28, 6.5) * mm});
            skLineSegment(sketch, "E1594", {"start": v(-2.28, 6.5) * mm, "end": v(-2.33, 6.5) * mm});
            skLineSegment(sketch, "E1595", {"start": v(-2.33, 6.5) * mm, "end": v(-2.72, 6.28) * mm});
            skLineSegment(sketch, "E1596", {"start": v(-2.72, 6.28) * mm, "end": v(-2.6, 6.05) * mm});
            skLineSegment(sketch, "E1597", {"start": v(-2.6, 6.05) * mm, "end": v(-2.4, 5.78) * mm});
            skLineSegment(sketch, "E1598", {"start": v(-2.4, 5.78) * mm, "end": v(-2.25, 5.38) * mm});
            skLineSegment(sketch, "E1599", {"start": v(-2.25, 5.38) * mm, "end": v(-1.85, 5.23) * mm});
            skLineSegment(sketch, "E1600", {"start": v(-1.85, 5.23) * mm, "end": v(-1.24, 5.36) * mm});
            skLineSegment(sketch, "E1601", {"start": v(-1.24, 5.36) * mm, "end": v(-0.77, 5.36) * mm});
            skLineSegment(sketch, "E1602", {"start": v(-0.77, 5.36) * mm, "end": v(0.21, 5.38) * mm});
            skLineSegment(sketch, "E1603", {"start": v(0.21, 5.38) * mm, "end": v(0.9, 5.38) * mm});
            skLineSegment(sketch, "E1604", {"start": v(0.9, 5.38) * mm, "end": v(1.7, 5.41) * mm});
            skLineSegment(sketch, "E1605", {"start": v(1.7, 5.41) * mm, "end": v(2.3, 5.36) * mm});
            skLineSegment(sketch, "E1606", {"start": v(2.3, 5.36) * mm, "end": v(2.94, 5.3) * mm});
            skLineSegment(sketch, "E1607", {"start": v(2.94, 5.3) * mm, "end": v(3.12, 5.17) * mm});
            skLineSegment(sketch, "E1608", {"start": v(3.12, 5.17) * mm, "end": v(3.36, 5.12) * mm});
            skLineSegment(sketch, "E1609", {"start": v(3.36, 5.12) * mm, "end": v(3.7, 5.28) * mm});
            skLineSegment(sketch, "E1610", {"start": v(3.7, 5.28) * mm, "end": v(3.73, 5.41) * mm});
            skLineSegment(sketch, "E1611", {"start": v(3.73, 5.41) * mm, "end": v(3.6, 5.91) * mm});
            skLineSegment(sketch, "E1612", {"start": v(3.6, 5.91) * mm, "end": v(3.6, 5.97) * mm});
            skLineSegment(sketch, "E1613", {"start": v(3.6, 5.97) * mm, "end": v(3.63, 6.31) * mm});
            skLineSegment(sketch, "E1614", {"start": v(3.63, 6.31) * mm, "end": v(3.58, 6.62) * mm});
            skLineSegment(sketch, "E1615", {"start": v(3.58, 6.62) * mm, "end": v(3.41, 6.81) * mm});
            skLineSegment(sketch, "E1616", {"start": v(3.41, 6.81) * mm, "end": v(3.36, 6.81) * mm});
            skLineSegment(sketch, "E1617", {"start": v(3.36, 6.81) * mm, "end": v(2.96, 6.65) * mm});
            skLineSegment(sketch, "E1618", {"start": v(2.96, 6.65) * mm, "end": v(2.64, 6.57) * mm});
            skLineSegment(sketch, "E1619", {"start": v(2.64, 6.57) * mm, "end": v(2.3, 6.52) * mm});
            skLineSegment(sketch, "E1620", {"start": v(2.3, 6.52) * mm, "end": v(2.25, 6.52) * mm});
            skLineSegment(sketch, "E1621", {"start": v(2.25, 6.52) * mm, "end": v(1.93, 6.73) * mm});
            skLineSegment(sketch, "E1622", {"start": v(1.93, 6.73) * mm, "end": v(1.79, 6.92) * mm});
            skLineSegment(sketch, "E1623", {"start": v(1.79, 6.92) * mm, "end": v(1.75, 7.18) * mm});
            skLineSegment(sketch, "E1624", {"start": v(1.75, 7.18) * mm, "end": v(1.64, 7.48) * mm});
            skLineSegment(sketch, "E1625", {"start": v(1.64, 7.48) * mm, "end": v(1.67, 7.69) * mm});
            skLineSegment(sketch, "E1626", {"start": v(1.67, 7.69) * mm, "end": v(1.67, 8.35) * mm});
            skLineSegment(sketch, "E1627", {"start": v(1.67, 8.35) * mm, "end": v(1.72, 8.8) * mm});
            skLineSegment(sketch, "E1628", {"start": v(1.72, 8.8) * mm, "end": v(1.7, 9.3) * mm});
            skLineSegment(sketch, "E1629", {"start": v(1.7, 9.3) * mm, "end": v(1.72, 9.83) * mm});
            skLineSegment(sketch, "E1630", {"start": v(1.72, 9.83) * mm, "end": v(1.67, 11.02) * mm});
            skLineSegment(sketch, "E1631", {"start": v(1.67, 11.02) * mm, "end": v(1.7, 11.4) * mm});
            skLineSegment(sketch, "E1632", {"start": v(1.7, 11.4) * mm, "end": v(1.8, 11.84) * mm});
            skLineSegment(sketch, "E1633", {"start": v(1.8, 11.84) * mm, "end": v(1.8, 12.5) * mm});
            skLineSegment(sketch, "E1634", {"start": v(1.8, 12.5) * mm, "end": v(1.9, 13) * mm});
            skLineSegment(sketch, "E1635", {"start": v(1.9, 13) * mm, "end": v(1.8, 13.48) * mm});
            skLineSegment(sketch, "E1636", {"start": v(1.8, 13.48) * mm, "end": v(1.85, 13.96) * mm});
            skLineSegment(sketch, "E1637", {"start": v(1.85, 13.96) * mm, "end": v(1.8, 14.86) * mm});
            skLineSegment(sketch, "E1638", {"start": v(1.8, 14.86) * mm, "end": v(1.8, 17.6) * mm});
            skLineSegment(sketch, "E1639", {"start": v(1.8, 17.6) * mm, "end": v(1.93, 18.16) * mm});
            skLineSegment(sketch, "E1640", {"start": v(1.93, 18.16) * mm, "end": v(1.88, 18.53) * mm});
            skLineSegment(sketch, "E1641", {"start": v(1.88, 18.53) * mm, "end": v(1.88, 19.25) * mm});
            skLineSegment(sketch, "E1642", {"start": v(1.88, 19.25) * mm, "end": v(1.83, 19.57) * mm});
            skLineSegment(sketch, "E1643", {"start": v(1.83, 19.57) * mm, "end": v(1.9, 20.03) * mm});
            skLineSegment(sketch, "E1644", {"start": v(1.9, 20.03) * mm, "end": v(1.98, 20.44) * mm});
            skLineSegment(sketch, "E1645", {"start": v(1.98, 20.44) * mm, "end": v(1.83, 20.94) * mm});
            skLineSegment(sketch, "E1646", {"start": v(1.83, 20.94) * mm, "end": v(1.85, 21.07) * mm});
            skLineSegment(sketch, "E1647", {"start": v(1.85, 21.07) * mm, "end": v(2.35, 20.62) * mm});
            skLineSegment(sketch, "E1648", {"start": v(2.35, 20.62) * mm, "end": v(2.75, 20.07) * mm});
            skLineSegment(sketch, "E1649", {"start": v(2.75, 20.07) * mm, "end": v(3.12, 19.57) * mm});
            skLineSegment(sketch, "E1650", {"start": v(3.12, 19.57) * mm, "end": v(3.5, 19.06) * mm});
            skLineSegment(sketch, "E1651", {"start": v(3.5, 19.06) * mm, "end": v(3.84, 18.5) * mm});
            skLineSegment(sketch, "E1652", {"start": v(3.84, 18.5) * mm, "end": v(4.34, 18.06) * mm});
            skLineSegment(sketch, "E1653", {"start": v(4.34, 18.06) * mm, "end": v(4.45, 17.85) * mm});
            skLineSegment(sketch, "E1654", {"start": v(4.45, 17.85) * mm, "end": v(4.63, 17.63) * mm});
            skLineSegment(sketch, "E1655", {"start": v(4.63, 17.63) * mm, "end": v(5.19, 16.76) * mm});
            skLineSegment(sketch, "E1656", {"start": v(5.19, 16.76) * mm, "end": v(5.53, 16.37) * mm});
            skLineSegment(sketch, "E1657", {"start": v(5.53, 16.37) * mm, "end": v(5.9, 15.65) * mm});
            skLineSegment(sketch, "E1658", {"start": v(5.9, 15.65) * mm, "end": v(6.14, 15.33) * mm});
            skLineSegment(sketch, "E1659", {"start": v(6.14, 15.33) * mm, "end": v(6.59, 14.67) * mm});
            skLineSegment(sketch, "E1660", {"start": v(6.59, 14.67) * mm, "end": v(6.77, 14.33) * mm});
            skLineSegment(sketch, "E1661", {"start": v(6.77, 14.33) * mm, "end": v(7.25, 13.67) * mm});
            skLineSegment(sketch, "E1662", {"start": v(7.25, 13.67) * mm, "end": v(7.62, 12.82) * mm});
            skLineSegment(sketch, "E1663", {"start": v(7.62, 12.82) * mm, "end": v(7.83, 12.42) * mm});
            skLineSegment(sketch, "E1664", {"start": v(7.83, 12.42) * mm, "end": v(8.07, 12.05) * mm});
            skLineSegment(sketch, "E1665", {"start": v(8.07, 12.05) * mm, "end": v(8.18, 11.68) * mm});
            skLineSegment(sketch, "E1666", {"start": v(8.18, 11.68) * mm, "end": v(8.28, 11.52) * mm});
            skLineSegment(sketch, "E1667", {"start": v(8.28, 11.52) * mm, "end": v(8.47, 11.02) * mm});
            skLineSegment(sketch, "E1668", {"start": v(8.47, 11.02) * mm, "end": v(8.63, 10.65) * mm});
            skLineSegment(sketch, "E1669", {"start": v(8.63, 10.65) * mm, "end": v(8.84, 10.3) * mm});
            skLineSegment(sketch, "E1670", {"start": v(8.84, 10.3) * mm, "end": v(9.02, 9.87) * mm});
            skLineSegment(sketch, "E1671", {"start": v(9.02, 9.87) * mm, "end": v(9.23, 9.4) * mm});
            skLineSegment(sketch, "E1672", {"start": v(9.23, 9.4) * mm, "end": v(9.47, 8.7) * mm});
            skLineSegment(sketch, "E1673", {"start": v(9.47, 8.7) * mm, "end": v(10.08, 7.37) * mm});
            skLineSegment(sketch, "E1674", {"start": v(10.08, 7.37) * mm, "end": v(10.27, 7) * mm});
            skLineSegment(sketch, "E1675", {"start": v(10.27, 7) * mm, "end": v(10.37, 6.68) * mm});
            skLineSegment(sketch, "E1676", {"start": v(10.37, 6.68) * mm, "end": v(10.26, 6.42) * mm});
            skLineSegment(sketch, "E1677", {"start": v(10.26, 6.42) * mm, "end": v(10.03, 6.28) * mm});
            skLineSegment(sketch, "E1678", {"start": v(10.03, 6.28) * mm, "end": v(9.66, 6.28) * mm});
            skLineSegment(sketch, "E1679", {"start": v(9.66, 6.28) * mm, "end": v(9.5, 6.26) * mm});
            skLineSegment(sketch, "E1680", {"start": v(9.5, 6.26) * mm, "end": v(9.28, 6.13) * mm});
            skLineSegment(sketch, "E1681", {"start": v(9.28, 6.13) * mm, "end": v(9.18, 5.91) * mm});
            skLineSegment(sketch, "E1682", {"start": v(9.18, 5.91) * mm, "end": v(9.18, 5.86) * mm});
            skLineSegment(sketch, "E1683", {"start": v(9.18, 5.86) * mm, "end": v(9.34, 5.76) * mm});
            skLineSegment(sketch, "E1684", {"start": v(9.34, 5.76) * mm, "end": v(9.47, 5.76) * mm});
            skLineSegment(sketch, "E1685", {"start": v(9.47, 5.76) * mm, "end": v(10.53, 5.57) * mm});
            skLineSegment(sketch, "E1686", {"start": v(10.53, 5.57) * mm, "end": v(11.32, 5.52) * mm});
            skLineSegment(sketch, "E1687", {"start": v(11.32, 5.52) * mm, "end": v(12.04, 5.65) * mm});
            skLineSegment(sketch, "E1688", {"start": v(12.04, 5.65) * mm, "end": v(12.6, 5.65) * mm});
            skLineSegment(sketch, "E1689", {"start": v(12.6, 5.65) * mm, "end": v(12.91, 5.54) * mm});
            skLineSegment(sketch, "E1690", {"start": v(12.91, 5.54) * mm, "end": v(13.23, 5.54) * mm});
            skLineSegment(sketch, "E1691", {"start": v(13.23, 5.54) * mm, "end": v(13.57, 5.41) * mm});
            skLineSegment(sketch, "E1692", {"start": v(13.57, 5.41) * mm, "end": v(13.73, 5.54) * mm});
            skLineSegment(sketch, "E1693", {"start": v(13.73, 5.54) * mm, "end": v(13.76, 5.68) * mm});
            skLineSegment(sketch, "E1694", {"start": v(13.76, 5.68) * mm, "end": v(13.64, 5.91) * mm});
            skLineSegment(sketch, "E1695", {"start": v(13.64, 5.91) * mm, "end": v(13.47, 6.05) * mm});
            skLineSegment(sketch, "E1696", {"start": v(13.47, 6.05) * mm, "end": v(13.18, 6.76) * mm});
            skLineSegment(sketch, "E1697", {"start": v(13.18, 6.76) * mm, "end": v(13.07, 7) * mm});
            skLineSegment(sketch, "E1698", {"start": v(13.07, 7) * mm, "end": v(13.1, 7.4) * mm});
            skLineSegment(sketch, "E1699", {"start": v(13.1, 7.4) * mm, "end": v(12.96, 8.48) * mm});
            skLineSegment(sketch, "E1700", {"start": v(12.96, 8.48) * mm, "end": v(12.91, 9) * mm});
            skLineSegment(sketch, "E1701", {"start": v(12.91, 9) * mm, "end": v(12.86, 9.49) * mm});
            skLineSegment(sketch, "E1702", {"start": v(12.86, 9.49) * mm, "end": v(12.86, 9.6) * mm});
            skLineSegment(sketch, "E1703", {"start": v(12.86, 9.6) * mm, "end": v(12.89, 10.15) * mm});
            skLineSegment(sketch, "E1704", {"start": v(12.89, 10.15) * mm, "end": v(12.86, 10.39) * mm});
            skLineSegment(sketch, "E1705", {"start": v(12.86, 10.39) * mm, "end": v(12.73, 10.7) * mm});
            skLineSegment(sketch, "E1706", {"start": v(12.73, 10.7) * mm, "end": v(12.78, 11.15) * mm});
            skLineSegment(sketch, "E1707", {"start": v(12.78, 11.15) * mm, "end": v(12.8, 11.5) * mm});
            skLineSegment(sketch, "E1708", {"start": v(12.8, 11.5) * mm, "end": v(12.67, 12.69) * mm});
            skLineSegment(sketch, "E1709", {"start": v(12.67, 12.69) * mm, "end": v(12.57, 13.48) * mm});
            skLineSegment(sketch, "E1710", {"start": v(12.57, 13.48) * mm, "end": v(12.52, 14.04) * mm});
            skLineSegment(sketch, "E1711", {"start": v(12.52, 14.04) * mm, "end": v(12.4, 14.7) * mm});
            skLineSegment(sketch, "E1712", {"start": v(12.4, 14.7) * mm, "end": v(12.36, 15.15) * mm});
            skLineSegment(sketch, "E1713", {"start": v(12.36, 15.15) * mm, "end": v(12.17, 17) * mm});
            skLineSegment(sketch, "E1714", {"start": v(12.17, 17) * mm, "end": v(11.99, 18.82) * mm});
            skLineSegment(sketch, "E1715", {"start": v(11.99, 18.82) * mm, "end": v(11.93, 20.92) * mm});
            skLineSegment(sketch, "E1716", {"start": v(11.93, 20.92) * mm, "end": v(11.93, 22.42) * mm});
            skLineSegment(sketch, "E1717", {"start": v(11.93, 22.42) * mm, "end": v(11.88, 23.56) * mm});
            skLineSegment(sketch, "E1718", {"start": v(11.88, 23.56) * mm, "end": v(11.9, 23.95) * mm});
            skLineSegment(sketch, "E1719", {"start": v(11.9, 23.95) * mm, "end": v(12.04, 24.2) * mm});
            skLineSegment(sketch, "E1720", {"start": v(12.04, 24.2) * mm, "end": v(12.44, 24.3) * mm});
            skLineSegment(sketch, "E1721", {"start": v(12.44, 24.3) * mm, "end": v(12.97, 24.32) * mm});
            skLineSegment(sketch, "E1722", {"start": v(12.97, 24.32) * mm, "end": v(13.43, 24.4) * mm});
            skLineSegment(sketch, "E1723", {"start": v(13.43, 24.4) * mm, "end": v(13.63, 24.7) * mm});
            skLineSegment(sketch, "E1724", {"start": v(13.63, 24.7) * mm, "end": v(13.63, 24.75) * mm});
            skLineSegment(sketch, "E1725", {"start": v(13.63, 24.75) * mm, "end": v(13.5, 24.95) * mm});
            skLineSegment(sketch, "E1726", {"start": v(13.5, 24.95) * mm, "end": v(13.26, 25) * mm});
            skLineSegment(sketch, "E1727", {"start": v(13.26, 25) * mm, "end": v(12.78, 24.96) * mm});
            skLineSegment(sketch, "E1728", {"start": v(12.78, 24.96) * mm, "end": v(12.12, 24.96) * mm});
            skLineSegment(sketch, "E1729", {"start": v(12.12, 24.96) * mm, "end": v(11.5, 25.02) * mm});
            skLineSegment(sketch, "E1730", {"start": v(11.5, 25.02) * mm, "end": v(10.87, 24.96) * mm});
            skLineSegment(sketch, "E1731", {"start": v(10.87, 24.96) * mm, "end": v(10.3, 24.96) * mm});
            skLineSegment(sketch, "E1732", {"start": v(10.3, 24.96) * mm, "end": v(9.82, 24.9) * mm});
            skLineSegment(sketch, "E1733", {"start": v(9.82, 24.9) * mm, "end": v(8.81, 24.86) * mm});
            skLineSegment(sketch, "E1734", {"start": v(8.81, 24.86) * mm, "end": v(8.57, 24.62) * mm});
            skLineSegment(sketch, "E1735", {"start": v(8.57, 24.62) * mm, "end": v(8.81, 24.38) * mm});
            skLineSegment(sketch, "E1736", {"start": v(8.81, 24.38) * mm, "end": v(9.29, 24.38) * mm});
            skLineSegment(sketch, "E1737", {"start": v(9.29, 24.38) * mm, "end": v(9.79, 24.22) * mm});
            skLineSegment(sketch, "E1738", {"start": v(9.79, 24.22) * mm, "end": v(10.1, 24.19) * mm});
            skLineSegment(sketch, "E1739", {"start": v(10.1, 24.19) * mm, "end": v(10.34, 24.1) * mm});
            skLineSegment(sketch, "E1740", {"start": v(10.34, 24.1) * mm, "end": v(10.3, 22.37) * mm});
            skLineSegment(sketch, "E1741", {"start": v(10.3, 22.37) * mm, "end": v(10.3, 22.08) * mm});
            skLineSegment(sketch, "E1742", {"start": v(10.3, 22.08) * mm, "end": v(10.4, 21.07) * mm});
            skLineSegment(sketch, "E1743", {"start": v(10.4, 21.07) * mm, "end": v(10.42, 20.07) * mm});
            skLineSegment(sketch, "E1744", {"start": v(10.42, 20.07) * mm, "end": v(10.58, 18.14) * mm});
            skLineSegment(sketch, "E1745", {"start": v(10.58, 18.14) * mm, "end": v(10.6, 17.1) * mm});
            skLineSegment(sketch, "E1746", {"start": v(10.6, 17.1) * mm, "end": v(10.74, 16.2) * mm});
            skLineSegment(sketch, "E1747", {"start": v(10.74, 16.2) * mm, "end": v(10.93, 14.2) * mm});
            skLineSegment(sketch, "E1748", {"start": v(10.93, 14.2) * mm, "end": v(11.09, 12.18) * mm});
            skLineSegment(sketch, "E1749", {"start": v(11.09, 12.18) * mm, "end": v(11.38, 8.22) * mm});
            skLineSegment(sketch, "E1750", {"start": v(11.38, 8.22) * mm, "end": v(11.09, 8.06) * mm});
            skLineSegment(sketch, "E1751", {"start": v(11.09, 8.06) * mm, "end": v(10.98, 8.08) * mm});
            skLineSegment(sketch, "E1752", {"start": v(10.98, 8.08) * mm, "end": v(10.85, 8.28) * mm});
            skLineSegment(sketch, "E1753", {"start": v(10.85, 8.28) * mm, "end": v(10.8, 8.56) * mm});
            skLineSegment(sketch, "E1754", {"start": v(10.8, 8.56) * mm, "end": v(10.69, 8.74) * mm});
            skLineSegment(sketch, "E1755", {"start": v(10.69, 8.74) * mm, "end": v(10.45, 9.22) * mm});
            skLineSegment(sketch, "E1756", {"start": v(10.45, 9.22) * mm, "end": v(10.21, 10.02) * mm});
            skLineSegment(sketch, "E1757", {"start": v(10.21, 10.02) * mm, "end": v(9.6, 11.42) * mm});
            skLineSegment(sketch, "E1758", {"start": v(9.6, 11.42) * mm, "end": v(9.37, 12.13) * mm});
            skLineSegment(sketch, "E1759", {"start": v(9.37, 12.13) * mm, "end": v(8.96, 13) * mm});
            skLineSegment(sketch, "E1760", {"start": v(8.96, 13) * mm, "end": v(8.55, 13.83) * mm});
            skLineSegment(sketch, "E1761", {"start": v(8.55, 13.83) * mm, "end": v(8.1, 14.88) * mm});
            skLineSegment(sketch, "E1762", {"start": v(8.1, 14.88) * mm, "end": v(7.78, 15.57) * mm});
            skLineSegment(sketch, "E1763", {"start": v(7.78, 15.57) * mm, "end": v(7.07, 16.87) * mm});
            skLineSegment(sketch, "E1764", {"start": v(7.07, 16.87) * mm, "end": v(6.7, 17.5) * mm});
            skLineSegment(sketch, "E1765", {"start": v(6.7, 17.5) * mm, "end": v(6.54, 17.82) * mm});
            skLineSegment(sketch, "E1766", {"start": v(6.54, 17.82) * mm, "end": v(5.5, 19.35) * mm});
            skLineSegment(sketch, "E1767", {"start": v(5.5, 19.35) * mm, "end": v(5.13, 19.99) * mm});
            skLineSegment(sketch, "E1768", {"start": v(5.13, 19.99) * mm, "end": v(4.74, 20.6) * mm});
            skLineSegment(sketch, "E1769", {"start": v(4.74, 20.6) * mm, "end": v(3.92, 21.76) * mm});
            skLineSegment(sketch, "E1770", {"start": v(3.92, 21.76) * mm, "end": v(2.49, 23.32) * mm});
            skLineSegment(sketch, "E1771", {"start": v(2.49, 23.32) * mm, "end": v(1.98, 23.85) * mm});
            skLineSegment(sketch, "E1772", {"start": v(1.98, 23.85) * mm, "end": v(0.9, 24.73) * mm});
            skLineSegment(sketch, "E1773", {"start": v(0.9, 24.73) * mm, "end": v(-0.21, 25.39) * mm});
            skLineSegment(sketch, "E1774", {"start": v(-0.21, 25.39) * mm, "end": v(-0.4, 25.47) * mm});
            skLineSegment(sketch, "E1775", {"start": v(-0.4, 25.47) * mm, "end": v(-1.59, 24.38) * mm});
            skLineSegment(sketch, "E1776", {"start": v(-4.1, 18.67) * mm, "end": v(-4.47, 18.96) * mm});
            skLineSegment(sketch, "E1777", {"start": v(-4.47, 18.96) * mm, "end": v(-4.87, 19.22) * mm});
            skLineSegment(sketch, "E1778", {"start": v(-4.87, 19.22) * mm, "end": v(-5.1, 19.57) * mm});
            skLineSegment(sketch, "E1779", {"start": v(-5.1, 19.57) * mm, "end": v(-5.27, 20.07) * mm});
            skLineSegment(sketch, "E1780", {"start": v(-5.27, 20.07) * mm, "end": v(-5.4, 21.13) * mm});
            skLineSegment(sketch, "E1781", {"start": v(-5.4, 21.13) * mm, "end": v(-5.4, 21.26) * mm});
            skLineSegment(sketch, "E1782", {"start": v(-5.4, 21.26) * mm, "end": v(-5.27, 21.82) * mm});
            skLineSegment(sketch, "E1783", {"start": v(-5.27, 21.82) * mm, "end": v(-5.13, 21.84) * mm});
            skLineSegment(sketch, "E1784", {"start": v(-5.13, 21.84) * mm, "end": v(-4.63, 21.73) * mm});
            skLineSegment(sketch, "E1785", {"start": v(-4.63, 21.73) * mm, "end": v(-4.5, 21.7) * mm});
            skLineSegment(sketch, "E1786", {"start": v(-4.5, 21.7) * mm, "end": v(-4.34, 21.7) * mm});
            skLineSegment(sketch, "E1787", {"start": v(-4.34, 21.7) * mm, "end": v(-4.02, 21.58) * mm});
            skLineSegment(sketch, "E1788", {"start": v(-4.02, 21.58) * mm, "end": v(-3.81, 21.52) * mm});
            skLineSegment(sketch, "E1789", {"start": v(-3.81, 21.52) * mm, "end": v(-3.62, 21.44) * mm});
            skLineSegment(sketch, "E1790", {"start": v(-3.62, 21.44) * mm, "end": v(-3.33, 21.23) * mm});
            skLineSegment(sketch, "E1791", {"start": v(-3.33, 21.23) * mm, "end": v(-2.96, 20.92) * mm});
            skLineSegment(sketch, "E1792", {"start": v(-2.96, 20.92) * mm, "end": v(-2.94, 20.84) * mm});
            skLineSegment(sketch, "E1793", {"start": v(-2.94, 20.84) * mm, "end": v(-2.88, 20.78) * mm});
            skLineSegment(sketch, "E1794", {"start": v(-2.88, 20.78) * mm, "end": v(-2.75, 20.54) * mm});
            skLineSegment(sketch, "E1795", {"start": v(-2.75, 20.54) * mm, "end": v(-2.7, 20.47) * mm});
            skLineSegment(sketch, "E1796", {"start": v(-2.7, 20.47) * mm, "end": v(-2.51, 19.78) * mm});
            skLineSegment(sketch, "E1797", {"start": v(-2.51, 19.78) * mm, "end": v(-2.54, 19.57) * mm});
            skLineSegment(sketch, "E1798", {"start": v(-2.54, 19.57) * mm, "end": v(-2.57, 19.2) * mm});
            skLineSegment(sketch, "E1799", {"start": v(-2.57, 19.2) * mm, "end": v(-2.72, 18.96) * mm});
            skLineSegment(sketch, "E1800", {"start": v(-2.72, 18.96) * mm, "end": v(-2.96, 18.8) * mm});
            skLineSegment(sketch, "E1801", {"start": v(-2.96, 18.8) * mm, "end": v(-3.1, 18.82) * mm});
            skLineSegment(sketch, "E1802", {"start": v(-3.1, 18.82) * mm, "end": v(-3.52, 18.59) * mm});
            skLineSegment(sketch, "E1803", {"start": v(-3.52, 18.59) * mm, "end": v(-3.57, 18.59) * mm});
            skLineSegment(sketch, "E1804", {"start": v(-3.57, 18.59) * mm, "end": v(-3.86, 18.64) * mm});
            skLineSegment(sketch, "E1805", {"start": v(-3.86, 18.64) * mm, "end": v(-4, 18.64) * mm});
            skLineSegment(sketch, "E1806", {"start": v(-4, 18.64) * mm, "end": v(-4.1, 18.67) * mm});
            skLineSegment(sketch, "E1807", {"start": v(-1.72, 25.68) * mm, "end": v(-2.36, 25.6) * mm});
            skLineSegment(sketch, "E1808", {"start": v(-2.36, 25.6) * mm, "end": v(-2.94, 25.44) * mm});
            skLineSegment(sketch, "E1809", {"start": v(-2.94, 25.44) * mm, "end": v(-3.36, 25.3) * mm});
            skLineSegment(sketch, "E1810", {"start": v(-3.36, 25.3) * mm, "end": v(-3.7, 25.1) * mm});
            skLineSegment(sketch, "E1811", {"start": v(-3.7, 25.1) * mm, "end": v(-4.6, 24.46) * mm});
            skLineSegment(sketch, "E1812", {"start": v(-4.6, 24.46) * mm, "end": v(-4.97, 24.14) * mm});
            skLineSegment(sketch, "E1813", {"start": v(-4.97, 24.14) * mm, "end": v(-5.24, 23.75) * mm});
            skLineSegment(sketch, "E1814", {"start": v(-5.24, 23.75) * mm, "end": v(-5.37, 23.56) * mm});
            skLineSegment(sketch, "E1815", {"start": v(-5.37, 23.56) * mm, "end": v(-5.48, 23.35) * mm});
            skLineSegment(sketch, "E1816", {"start": v(-5.48, 23.35) * mm, "end": v(-5.77, 22.4) * mm});
            skLineSegment(sketch, "E1817", {"start": v(-5.77, 22.4) * mm, "end": v(-5.93, 22.34) * mm});
            skLineSegment(sketch, "E1818", {"start": v(-5.93, 22.34) * mm, "end": v(-6.38, 22.48) * mm});
            skLineSegment(sketch, "E1819", {"start": v(-6.38, 22.48) * mm, "end": v(-6.59, 22.5) * mm});
            skLineSegment(sketch, "E1820", {"start": v(-6.59, 22.5) * mm, "end": v(-7.38, 22.87) * mm});
            skLineSegment(sketch, "E1821", {"start": v(-7.38, 22.87) * mm, "end": v(-7.73, 23.3) * mm});
            skLineSegment(sketch, "E1822", {"start": v(-7.73, 23.3) * mm, "end": v(-7.88, 23.72) * mm});
            skLineSegment(sketch, "E1823", {"start": v(-7.88, 23.72) * mm, "end": v(-7.94, 23.85) * mm});
            skLineSegment(sketch, "E1824", {"start": v(-7.94, 23.85) * mm, "end": v(-7.94, 24.01) * mm});
            skLineSegment(sketch, "E1825", {"start": v(-7.94, 24.01) * mm, "end": v(-7.96, 24.14) * mm});
            skLineSegment(sketch, "E1826", {"start": v(-7.96, 24.14) * mm, "end": v(-7.78, 24.35) * mm});
            skLineSegment(sketch, "E1827", {"start": v(-7.78, 24.35) * mm, "end": v(-7.54, 24.28) * mm});
            skLineSegment(sketch, "E1828", {"start": v(-7.54, 24.28) * mm, "end": v(-7.33, 24.01) * mm});
            skLineSegment(sketch, "E1829", {"start": v(-7.33, 24.01) * mm, "end": v(-7.09, 23.75) * mm});
            skLineSegment(sketch, "E1830", {"start": v(-7.09, 23.75) * mm, "end": v(-6.85, 23.7) * mm});
            skLineSegment(sketch, "E1831", {"start": v(-6.85, 23.7) * mm, "end": v(-6.61, 23.75) * mm});
            skLineSegment(sketch, "E1832", {"start": v(-6.61, 23.75) * mm, "end": v(-6.38, 23.9) * mm});
            skLineSegment(sketch, "E1833", {"start": v(-6.38, 23.9) * mm, "end": v(-6.24, 24.12) * mm});
            skLineSegment(sketch, "E1834", {"start": v(-6.24, 24.12) * mm, "end": v(-6.2, 24.28) * mm});
            skLineSegment(sketch, "E1835", {"start": v(-6.2, 24.28) * mm, "end": v(-6.3, 24.51) * mm});
            skLineSegment(sketch, "E1836", {"start": v(-6.3, 24.51) * mm, "end": v(-6.4, 24.75) * mm});
            skLineSegment(sketch, "E1837", {"start": v(-6.4, 24.75) * mm, "end": v(-6.64, 24.9) * mm});
            skLineSegment(sketch, "E1838", {"start": v(-6.64, 24.9) * mm, "end": v(-6.83, 25.1) * mm});
            skLineSegment(sketch, "E1839", {"start": v(-6.83, 25.1) * mm, "end": v(-7.04, 25.15) * mm});
            skLineSegment(sketch, "E1840", {"start": v(-7.04, 25.15) * mm, "end": v(-7.12, 25.2) * mm});
            skLineSegment(sketch, "E1841", {"start": v(-7.12, 25.2) * mm, "end": v(-7.28, 25.23) * mm});
            skLineSegment(sketch, "E1842", {"start": v(-7.28, 25.23) * mm, "end": v(-7.57, 25.17) * mm});
            skLineSegment(sketch, "E1843", {"start": v(-7.57, 25.17) * mm, "end": v(-7.94, 24.94) * mm});
            skLineSegment(sketch, "E1844", {"start": v(-7.94, 24.94) * mm, "end": v(-8.23, 24.57) * mm});
            skLineSegment(sketch, "E1845", {"start": v(-8.23, 24.57) * mm, "end": v(-8.33, 24.33) * mm});
            skLineSegment(sketch, "E1846", {"start": v(-8.33, 24.33) * mm, "end": v(-8.41, 24.14) * mm});
            skLineSegment(sketch, "E1847", {"start": v(-8.41, 24.14) * mm, "end": v(-8.47, 23.8) * mm});
            skLineSegment(sketch, "E1848", {"start": v(-8.47, 23.8) * mm, "end": v(-8.39, 23.3) * mm});
            skLineSegment(sketch, "E1849", {"start": v(-8.39, 23.3) * mm, "end": v(-8.2, 22.77) * mm});
            skLineSegment(sketch, "E1850", {"start": v(-8.2, 22.77) * mm, "end": v(-7.86, 22.42) * mm});
            skLineSegment(sketch, "E1851", {"start": v(-7.86, 22.42) * mm, "end": v(-7.51, 22.1) * mm});
            skLineSegment(sketch, "E1852", {"start": v(-7.51, 22.1) * mm, "end": v(-7.28, 22) * mm});
            skLineSegment(sketch, "E1853", {"start": v(-7.28, 22) * mm, "end": v(-7.04, 21.9) * mm});
            skLineSegment(sketch, "E1854", {"start": v(-7.04, 21.9) * mm, "end": v(-6.67, 21.84) * mm});
            skLineSegment(sketch, "E1855", {"start": v(-6.67, 21.84) * mm, "end": v(-6.3, 21.76) * mm});
            skLineSegment(sketch, "E1856", {"start": v(-6.3, 21.76) * mm, "end": v(-6.06, 21.76) * mm});
            skLineSegment(sketch, "E1857", {"start": v(-6.06, 21.76) * mm, "end": v(-5.82, 21.73) * mm});
            skLineSegment(sketch, "E1858", {"start": v(-5.82, 21.73) * mm, "end": v(-5.82, 21.68) * mm});
            skLineSegment(sketch, "E1859", {"start": v(-5.82, 21.68) * mm, "end": v(-5.87, 21.29) * mm});
            skLineSegment(sketch, "E1860", {"start": v(-5.87, 21.29) * mm, "end": v(-5.87, 20.62) * mm});
            skLineSegment(sketch, "E1861", {"start": v(-5.87, 20.62) * mm, "end": v(-5.82, 20.28) * mm});
            skLineSegment(sketch, "E1862", {"start": v(-5.82, 20.28) * mm, "end": v(-5.74, 19.9) * mm});
            skLineSegment(sketch, "E1863", {"start": v(-5.74, 19.9) * mm, "end": v(-5.66, 19.57) * mm});
            skLineSegment(sketch, "E1864", {"start": v(-5.66, 19.57) * mm, "end": v(-5.5, 19.28) * mm});
            skLineSegment(sketch, "E1865", {"start": v(-5.5, 19.28) * mm, "end": v(-5.32, 19.01) * mm});
            skLineSegment(sketch, "E1866", {"start": v(-5.32, 19.01) * mm, "end": v(-4.79, 18.64) * mm});
            skLineSegment(sketch, "E1867", {"start": v(-4.79, 18.64) * mm, "end": v(-4.63, 18.5) * mm});
            skLineSegment(sketch, "E1868", {"start": v(-4.63, 18.5) * mm, "end": v(-4.05, 18.27) * mm});
            skLineSegment(sketch, "E1869", {"start": v(-4.05, 18.27) * mm, "end": v(-3.6, 18.22) * mm});
            skLineSegment(sketch, "E1870", {"start": v(-3.6, 18.22) * mm, "end": v(-3.09, 18.3) * mm});
            skLineSegment(sketch, "E1871", {"start": v(-3.09, 18.3) * mm, "end": v(-2.6, 18.48) * mm});
            skLineSegment(sketch, "E1872", {"start": v(-2.6, 18.48) * mm, "end": v(-2.06, 18.96) * mm});
            skLineSegment(sketch, "E1873", {"start": v(-2.06, 18.96) * mm, "end": v(-1.83, 19.3) * mm});
            skLineSegment(sketch, "E1874", {"start": v(-1.83, 19.3) * mm, "end": v(-1.77, 19.4) * mm});
            skLineSegment(sketch, "E1875", {"start": v(-1.77, 19.4) * mm, "end": v(-1.7, 19.49) * mm});
            skLineSegment(sketch, "E1876", {"start": v(-1.7, 19.49) * mm, "end": v(-1.56, 19.91) * mm});
            skLineSegment(sketch, "E1877", {"start": v(-1.56, 19.91) * mm, "end": v(-1.64, 20.28) * mm});
            skLineSegment(sketch, "E1878", {"start": v(-1.64, 20.28) * mm, "end": v(-1.64, 20.54) * mm});
            skLineSegment(sketch, "E1879", {"start": v(-1.64, 20.54) * mm, "end": v(-1.85, 21) * mm});
            skLineSegment(sketch, "E1880", {"start": v(-1.85, 21) * mm, "end": v(-2.02, 21.27) * mm});
            skLineSegment(sketch, "E1881", {"start": v(-2.02, 21.27) * mm, "end": v(-2.28, 21.42) * mm});
            skLineSegment(sketch, "E1882", {"start": v(-2.28, 21.42) * mm, "end": v(-2.54, 21.73) * mm});
            skLineSegment(sketch, "E1883", {"start": v(-2.54, 21.73) * mm, "end": v(-2.6, 21.76) * mm});
            skLineSegment(sketch, "E1884", {"start": v(-2.6, 21.76) * mm, "end": v(-3.18, 22.03) * mm});
            skLineSegment(sketch, "E1885", {"start": v(-3.18, 22.03) * mm, "end": v(-4.1, 22.21) * mm});
            skLineSegment(sketch, "E1886", {"start": v(-4.1, 22.21) * mm, "end": v(-4.58, 22.3) * mm});
            skLineSegment(sketch, "E1887", {"start": v(-4.58, 22.3) * mm, "end": v(-5.05, 22.3) * mm});
            skLineSegment(sketch, "E1888", {"start": v(-5.05, 22.3) * mm, "end": v(-5.3, 22.32) * mm});
            skLineSegment(sketch, "E1889", {"start": v(-5.3, 22.32) * mm, "end": v(-5.32, 22.56) * mm});
            skLineSegment(sketch, "E1890", {"start": v(-5.32, 22.56) * mm, "end": v(-5.15, 23.18) * mm});
            skLineSegment(sketch, "E1891", {"start": v(-5.15, 23.18) * mm, "end": v(-4.84, 23.75) * mm});
            skLineSegment(sketch, "E1892", {"start": v(-4.84, 23.75) * mm, "end": v(-4.42, 24.22) * mm});
            skLineSegment(sketch, "E1893", {"start": v(-4.42, 24.22) * mm, "end": v(-3.76, 24.65) * mm});
            skLineSegment(sketch, "E1894", {"start": v(-3.76, 24.65) * mm, "end": v(-3.5, 24.7) * mm});
            skLineSegment(sketch, "E1895", {"start": v(-3.5, 24.7) * mm, "end": v(-3.25, 24.8) * mm});
            skLineSegment(sketch, "E1896", {"start": v(-3.25, 24.8) * mm, "end": v(-2.94, 24.86) * mm});
            skLineSegment(sketch, "E1897", {"start": v(-2.94, 24.86) * mm, "end": v(-2.65, 24.83) * mm});
            skLineSegment(sketch, "E1898", {"start": v(-2.65, 24.83) * mm, "end": v(-2.49, 24.83) * mm});
            skLineSegment(sketch, "E1899", {"start": v(-2.49, 24.83) * mm, "end": v(-2.28, 24.8) * mm});
            skLineSegment(sketch, "E1900", {"start": v(-2.28, 24.8) * mm, "end": v(-1.98, 24.67) * mm});
            skLineSegment(sketch, "E1901", {"start": v(-1.98, 24.67) * mm, "end": v(-1.77, 24.51) * mm});
            skLineSegment(sketch, "E1902", {"start": v(-1.77, 24.51) * mm, "end": v(-1.56, 24.35) * mm});
            skLineSegment(sketch, "E1903", {"start": v(-1.56, 24.35) * mm, "end": v(-1.3, 24.17) * mm});
            skLineSegment(sketch, "E1904", {"start": v(-1.3, 24.17) * mm, "end": v(-1, 23.98) * mm});
            skLineSegment(sketch, "E1905", {"start": v(-1, 23.98) * mm, "end": v(0.26, 25) * mm});
            skLineSegment(sketch, "E1906", {"start": v(0.26, 25) * mm, "end": v(-1.08, 25.63) * mm});
            skLineSegment(sketch, "E1907", {"start": v(-1.08, 25.63) * mm, "end": v(-1.61, 25.76) * mm});
            skLineSegment(sketch, "E1908", {"start": v(-1.61, 25.76) * mm, "end": v(-1.72, 25.76) * mm});
            skLineSegment(sketch, "E1909", {"start": v(-1.72, 25.76) * mm, "end": v(-1.72, 25.68) * mm});
            skLineSegment(sketch, "E1910", {"start": v(24.5, 0.91) * mm, "end": v(25.1, 1.34) * mm});
            skLineSegment(sketch, "E1911", {"start": v(25.1, 1.34) * mm, "end": v(25.14, 1.36) * mm});
            skLineSegment(sketch, "E1912", {"start": v(25.14, 1.36) * mm, "end": v(25.54, 1.57) * mm});
            skLineSegment(sketch, "E1913", {"start": v(25.54, 1.57) * mm, "end": v(25.98, 1.68) * mm});
            skLineSegment(sketch, "E1914", {"start": v(25.98, 1.68) * mm, "end": v(26.33, 1.57) * mm});
            skLineSegment(sketch, "E1915", {"start": v(26.33, 1.57) * mm, "end": v(26.56, 1.13) * mm});
            skLineSegment(sketch, "E1916", {"start": v(26.56, 1.13) * mm, "end": v(26.56, 0.8) * mm});
            skLineSegment(sketch, "E1917", {"start": v(26.56, 0.8) * mm, "end": v(26.46, 0.01) * mm});
            skLineSegment(sketch, "E1918", {"start": v(26.46, 0.01) * mm, "end": v(26.24, -0.48) * mm});
            skLineSegment(sketch, "E1919", {"start": v(26.24, -0.48) * mm, "end": v(25.82, -0.86) * mm});
            skLineSegment(sketch, "E1920", {"start": v(25.82, -0.86) * mm, "end": v(25.32, -1.07) * mm});
            skLineSegment(sketch, "E1921", {"start": v(25.32, -1.07) * mm, "end": v(24.92, -1.36) * mm});
            skLineSegment(sketch, "E1922", {"start": v(24.92, -1.36) * mm, "end": v(23.65, -1.97) * mm});
            skLineSegment(sketch, "E1923", {"start": v(23.65, -1.97) * mm, "end": v(23.36, -2.66) * mm});
            skLineSegment(sketch, "E1924", {"start": v(23.36, -2.66) * mm, "end": v(23.27, -2.77) * mm});
            skLineSegment(sketch, "E1925", {"start": v(23.27, -2.77) * mm, "end": v(23.03, -2.95) * mm});
            skLineSegment(sketch, "E1926", {"start": v(23.03, -2.95) * mm, "end": v(22.7, -3.12) * mm});
            skLineSegment(sketch, "E1927", {"start": v(22.7, -3.12) * mm, "end": v(22.3, -3.19) * mm});
            skLineSegment(sketch, "E1928", {"start": v(22.3, -3.19) * mm, "end": v(22.17, -3.19) * mm});
            skLineSegment(sketch, "E1929", {"start": v(22.17, -3.19) * mm, "end": v(21.74, -3.04) * mm});
            skLineSegment(sketch, "E1930", {"start": v(21.74, -3.04) * mm, "end": v(21.4, -2.77) * mm});
            skLineSegment(sketch, "E1931", {"start": v(21.4, -2.77) * mm, "end": v(21.23, -2.66) * mm});
            skLineSegment(sketch, "E1932", {"start": v(21.23, -2.66) * mm, "end": v(20.88, -2.4) * mm});
            skLineSegment(sketch, "E1933", {"start": v(20.88, -2.4) * mm, "end": v(20.5, -2.08) * mm});
            skLineSegment(sketch, "E1934", {"start": v(20.5, -2.08) * mm, "end": v(20.3, -1.78) * mm});
            skLineSegment(sketch, "E1935", {"start": v(20.3, -1.78) * mm, "end": v(20.16, -1.68) * mm});
            skLineSegment(sketch, "E1936", {"start": v(20.16, -1.68) * mm, "end": v(20.08, -1.68) * mm});
            skLineSegment(sketch, "E1937", {"start": v(20.08, -1.68) * mm, "end": v(19.6, -1.62) * mm});
            skLineSegment(sketch, "E1938", {"start": v(19.6, -1.62) * mm, "end": v(19.18, -1.5) * mm});
            skLineSegment(sketch, "E1939", {"start": v(19.18, -1.5) * mm, "end": v(18.93, -1.4) * mm});
            skLineSegment(sketch, "E1940", {"start": v(18.93, -1.4) * mm, "end": v(18.65, -1.28) * mm});
            skLineSegment(sketch, "E1941", {"start": v(18.65, -1.28) * mm, "end": v(18.27, -1) * mm});
            skLineSegment(sketch, "E1942", {"start": v(18.27, -1) * mm, "end": v(17.89, -0.67) * mm});
            skLineSegment(sketch, "E1943", {"start": v(17.89, -0.67) * mm, "end": v(17.52, -0.18) * mm});
            skLineSegment(sketch, "E1944", {"start": v(17.52, -0.18) * mm, "end": v(17.28, 0.4) * mm});
            skLineSegment(sketch, "E1945", {"start": v(17.28, 0.4) * mm, "end": v(17.28, 0.5) * mm});
            skLineSegment(sketch, "E1946", {"start": v(17.28, 0.5) * mm, "end": v(17.47, 0.88) * mm});
            skLineSegment(sketch, "E1947", {"start": v(17.47, 0.88) * mm, "end": v(17.83, 1.1) * mm});
            skLineSegment(sketch, "E1948", {"start": v(17.83, 1.1) * mm, "end": v(17.97, 1.1) * mm});
            skLineSegment(sketch, "E1949", {"start": v(17.97, 1.1) * mm, "end": v(18.52, 1.02) * mm});
            skLineSegment(sketch, "E1950", {"start": v(18.52, 1.02) * mm, "end": v(19.47, 0.78) * mm});
            skLineSegment(sketch, "E1951", {"start": v(19.47, 0.78) * mm, "end": v(19.69, 0.54) * mm});
            skLineSegment(sketch, "E1952", {"start": v(19.69, 0.54) * mm, "end": v(20.37, 0.1) * mm});
            skLineSegment(sketch, "E1953", {"start": v(20.37, 0.1) * mm, "end": v(20.48, 0.12) * mm});
            skLineSegment(sketch, "E1954", {"start": v(20.48, 0.12) * mm, "end": v(20.22, 0.59) * mm});
            skLineSegment(sketch, "E1955", {"start": v(20.22, 0.59) * mm, "end": v(20.03, 1.07) * mm});
            skLineSegment(sketch, "E1956", {"start": v(20.03, 1.07) * mm, "end": v(19.85, 1.63) * mm});
            skLineSegment(sketch, "E1957", {"start": v(19.85, 1.63) * mm, "end": v(19.69, 2.24) * mm});
            skLineSegment(sketch, "E1958", {"start": v(19.69, 2.24) * mm, "end": v(19.77, 2.53) * mm});
            skLineSegment(sketch, "E1959", {"start": v(19.77, 2.53) * mm, "end": v(20.16, 2.87) * mm});
            skLineSegment(sketch, "E1960", {"start": v(20.16, 2.87) * mm, "end": v(20.77, 2.98) * mm});
            skLineSegment(sketch, "E1961", {"start": v(20.77, 2.98) * mm, "end": v(20.98, 2.98) * mm});
            skLineSegment(sketch, "E1962", {"start": v(20.98, 2.98) * mm, "end": v(21.3, 2.84) * mm});
            skLineSegment(sketch, "E1963", {"start": v(21.3, 2.84) * mm, "end": v(21.54, 2.63) * mm});
            skLineSegment(sketch, "E1964", {"start": v(21.54, 2.63) * mm, "end": v(21.78, 2.2) * mm});
            skLineSegment(sketch, "E1965", {"start": v(21.78, 2.2) * mm, "end": v(22.1, 1.87) * mm});
            skLineSegment(sketch, "E1966", {"start": v(22.1, 1.87) * mm, "end": v(22.53, 2.46) * mm});
            skLineSegment(sketch, "E1967", {"start": v(22.53, 2.46) * mm, "end": v(22.89, 3.08) * mm});
            skLineSegment(sketch, "E1968", {"start": v(22.89, 3.08) * mm, "end": v(23.28, 3.38) * mm});
            skLineSegment(sketch, "E1969", {"start": v(23.28, 3.38) * mm, "end": v(23.76, 3.5) * mm});
            skLineSegment(sketch, "E1970", {"start": v(23.76, 3.5) * mm, "end": v(24.16, 3.4) * mm});
            skLineSegment(sketch, "E1971", {"start": v(24.16, 3.4) * mm, "end": v(24.4, 3) * mm});
            skLineSegment(sketch, "E1972", {"start": v(24.4, 3) * mm, "end": v(24.4, 2.8) * mm});
            skLineSegment(sketch, "E1973", {"start": v(24.4, 2.8) * mm, "end": v(24.26, 1.73) * mm});
            skLineSegment(sketch, "E1974", {"start": v(24.26, 1.73) * mm, "end": v(24.16, 1.1) * mm});
            skLineSegment(sketch, "E1975", {"start": v(24.16, 1.1) * mm, "end": v(24.1, 0.75) * mm});
            skLineSegment(sketch, "E1976", {"start": v(24.1, 0.75) * mm, "end": v(24.02, 0.46) * mm});
            skLineSegment(sketch, "E1977", {"start": v(24.02, 0.46) * mm, "end": v(24.27, 0.66) * mm});
            skLineSegment(sketch, "E1978", {"start": v(24.27, 0.66) * mm, "end": v(24.5, 0.91) * mm});
            skLineSegment(sketch, "E1979", {"start": v(19.66, -0.17) * mm, "end": v(19, 0.37) * mm});
            skLineSegment(sketch, "E1980", {"start": v(19, 0.37) * mm, "end": v(18.26, 0.67) * mm});
            skLineSegment(sketch, "E1981", {"start": v(18.26, 0.67) * mm, "end": v(17.86, 0.6) * mm});
            skLineSegment(sketch, "E1982", {"start": v(17.86, 0.6) * mm, "end": v(17.83, 0.52) * mm});
            skLineSegment(sketch, "E1983", {"start": v(17.83, 0.52) * mm, "end": v(18.03, -0.18) * mm});
            skLineSegment(sketch, "E1984", {"start": v(18.03, -0.18) * mm, "end": v(18.47, -0.6) * mm});
            skLineSegment(sketch, "E1985", {"start": v(18.47, -0.6) * mm, "end": v(18.76, -0.84) * mm});
            skLineSegment(sketch, "E1986", {"start": v(18.76, -0.84) * mm, "end": v(19.1, -1) * mm});
            skLineSegment(sketch, "E1987", {"start": v(19.1, -1) * mm, "end": v(19.5, -1.18) * mm});
            skLineSegment(sketch, "E1988", {"start": v(19.5, -1.18) * mm, "end": v(19.98, -1.2) * mm});
            skLineSegment(sketch, "E1989", {"start": v(19.98, -1.2) * mm, "end": v(20.16, -1.18) * mm});
            skLineSegment(sketch, "E1990", {"start": v(20.16, -1.18) * mm, "end": v(20.35, -1.15) * mm});
            skLineSegment(sketch, "E1991", {"start": v(20.35, -1.15) * mm, "end": v(20.3, -1.03) * mm});
            skLineSegment(sketch, "E1992", {"start": v(20.3, -1.03) * mm, "end": v(20.13, -0.8) * mm});
            skLineSegment(sketch, "E1993", {"start": v(20.13, -0.8) * mm, "end": v(19.89, -0.45) * mm});
            skLineSegment(sketch, "E1994", {"start": v(19.89, -0.45) * mm, "end": v(19.66, -0.17) * mm});
            skLineSegment(sketch, "E1995", {"start": v(21.75, -0.17) * mm, "end": v(21.78, 0.46) * mm});
            skLineSegment(sketch, "E1996", {"start": v(21.78, 0.46) * mm, "end": v(21.75, 0.8) * mm});
            skLineSegment(sketch, "E1997", {"start": v(21.75, 0.8) * mm, "end": v(21.46, 1.44) * mm});
            skLineSegment(sketch, "E1998", {"start": v(21.46, 1.44) * mm, "end": v(21.17, 2.1) * mm});
            skLineSegment(sketch, "E1999", {"start": v(21.17, 2.1) * mm, "end": v(20.97, 2.37) * mm});
            skLineSegment(sketch, "E2000", {"start": v(20.97, 2.37) * mm, "end": v(20.74, 2.6) * mm});
            skLineSegment(sketch, "E2001", {"start": v(20.74, 2.6) * mm, "end": v(20.72, 2.6) * mm});
            skLineSegment(sketch, "E2002", {"start": v(20.72, 2.6) * mm, "end": v(20.44, 2.48) * mm});
            skLineSegment(sketch, "E2003", {"start": v(20.44, 2.48) * mm, "end": v(20.3, 2.2) * mm});
            skLineSegment(sketch, "E2004", {"start": v(20.3, 2.2) * mm, "end": v(20.27, 2.02) * mm});
            skLineSegment(sketch, "E2005", {"start": v(20.27, 2.02) * mm, "end": v(20.48, 1.42) * mm});
            skLineSegment(sketch, "E2006", {"start": v(20.48, 1.42) * mm, "end": v(20.66, 1.03) * mm});
            skLineSegment(sketch, "E2007", {"start": v(20.66, 1.03) * mm, "end": v(20.92, 0.47) * mm});
            skLineSegment(sketch, "E2008", {"start": v(20.92, 0.47) * mm, "end": v(21.18, -0.08) * mm});
            skLineSegment(sketch, "E2009", {"start": v(21.18, -0.08) * mm, "end": v(21.33, -0.5) * mm});
            skLineSegment(sketch, "E2010", {"start": v(21.33, -0.5) * mm, "end": v(21.52, -0.64) * mm});
            skLineSegment(sketch, "E2011", {"start": v(21.52, -0.64) * mm, "end": v(21.67, -0.73) * mm});
            skLineSegment(sketch, "E2012", {"start": v(21.67, -0.73) * mm, "end": v(21.78, -0.5) * mm});
            skLineSegment(sketch, "E2013", {"start": v(21.78, -0.5) * mm, "end": v(21.75, -0.17) * mm});
            skLineSegment(sketch, "E2014", {"start": v(23.1, 2.1) * mm, "end": v(22.97, 1.87) * mm});
            skLineSegment(sketch, "E2015", {"start": v(22.97, 1.87) * mm, "end": v(22.94, 1.44) * mm});
            skLineSegment(sketch, "E2016", {"start": v(22.94, 1.44) * mm, "end": v(22.94, 1) * mm});
            skLineSegment(sketch, "E2017", {"start": v(22.94, 1) * mm, "end": v(22.91, 0.54) * mm});
            skLineSegment(sketch, "E2018", {"start": v(22.91, 0.54) * mm, "end": v(22.94, -0.07) * mm});
            skLineSegment(sketch, "E2019", {"start": v(22.94, -0.07) * mm, "end": v(23.02, -0.6) * mm});
            skLineSegment(sketch, "E2020", {"start": v(23.02, -0.6) * mm, "end": v(23.2, -0.43) * mm});
            skLineSegment(sketch, "E2021", {"start": v(23.2, -0.43) * mm, "end": v(23.26, -0.2) * mm});
            skLineSegment(sketch, "E2022", {"start": v(23.26, -0.2) * mm, "end": v(23.79, 1.3) * mm});
            skLineSegment(sketch, "E2023", {"start": v(23.79, 1.3) * mm, "end": v(24, 2.74) * mm});
            skLineSegment(sketch, "E2024", {"start": v(24, 2.74) * mm, "end": v(23.97, 3.06) * mm});
            skLineSegment(sketch, "E2025", {"start": v(23.97, 3.06) * mm, "end": v(23.47, 2.85) * mm});
            skLineSegment(sketch, "E2026", {"start": v(23.47, 2.85) * mm, "end": v(23.22, 2.51) * mm});
            skLineSegment(sketch, "E2027", {"start": v(23.22, 2.51) * mm, "end": v(23.1, 2.1) * mm});
            skLineSegment(sketch, "E2028", {"start": v(24, -0.6) * mm, "end": v(23.92, -0.8) * mm});
            skLineSegment(sketch, "E2029", {"start": v(23.92, -0.8) * mm, "end": v(23.73, -1.1) * mm});
            skLineSegment(sketch, "E2030", {"start": v(23.73, -1.1) * mm, "end": v(23.73, -1.2) * mm});
            skLineSegment(sketch, "E2031", {"start": v(23.73, -1.2) * mm, "end": v(23.76, -1.42) * mm});
            skLineSegment(sketch, "E2032", {"start": v(23.76, -1.42) * mm, "end": v(24.74, -0.9) * mm});
            skLineSegment(sketch, "E2033", {"start": v(24.74, -0.9) * mm, "end": v(25.7, -0.36) * mm});
            skLineSegment(sketch, "E2034", {"start": v(25.7, -0.36) * mm, "end": v(25.8, -0.16) * mm});
            skLineSegment(sketch, "E2035", {"start": v(25.8, -0.16) * mm, "end": v(25.93, 0.07) * mm});
            skLineSegment(sketch, "E2036", {"start": v(25.93, 0.07) * mm, "end": v(26, 0.67) * mm});
            skLineSegment(sketch, "E2037", {"start": v(26, 0.67) * mm, "end": v(25.96, 1.1) * mm});
            skLineSegment(sketch, "E2038", {"start": v(25.96, 1.1) * mm, "end": v(25.82, 1.3) * mm});
            skLineSegment(sketch, "E2039", {"start": v(25.82, 1.3) * mm, "end": v(25.26, 1.08) * mm});
            skLineSegment(sketch, "E2040", {"start": v(25.26, 1.08) * mm, "end": v(24.82, 0.7) * mm});
            skLineSegment(sketch, "E2041", {"start": v(24.82, 0.7) * mm, "end": v(24.48, 0.23) * mm});
            skLineSegment(sketch, "E2042", {"start": v(24.48, 0.23) * mm, "end": v(24.18, -0.28) * mm});
            skLineSegment(sketch, "E2043", {"start": v(24.18, -0.28) * mm, "end": v(24, -0.6) * mm});
            skLineSegment(sketch, "E2044", {"start": v(19.24, -4.14) * mm, "end": v(18.55, -4.38) * mm});
            skLineSegment(sketch, "E2045", {"start": v(18.55, -4.38) * mm, "end": v(18.5, -4.4) * mm});
            skLineSegment(sketch, "E2046", {"start": v(18.5, -4.4) * mm, "end": v(18.04, -4.48) * mm});
            skLineSegment(sketch, "E2047", {"start": v(18.04, -4.48) * mm, "end": v(17.6, -4.46) * mm});
            skLineSegment(sketch, "E2048", {"start": v(17.6, -4.46) * mm, "end": v(17.28, -4.25) * mm});
            skLineSegment(sketch, "E2049", {"start": v(17.28, -4.25) * mm, "end": v(17.17, -3.74) * mm});
            skLineSegment(sketch, "E2050", {"start": v(17.17, -3.74) * mm, "end": v(17.25, -3.45) * mm});
            skLineSegment(sketch, "E2051", {"start": v(17.25, -3.45) * mm, "end": v(17.57, -2.71) * mm});
            skLineSegment(sketch, "E2052", {"start": v(17.57, -2.71) * mm, "end": v(17.92, -2.3) * mm});
            skLineSegment(sketch, "E2053", {"start": v(17.92, -2.3) * mm, "end": v(18.41, -2.05) * mm});
            skLineSegment(sketch, "E2054", {"start": v(18.41, -2.05) * mm, "end": v(18.94, -2) * mm});
            skLineSegment(sketch, "E2055", {"start": v(18.94, -2) * mm, "end": v(19.4, -1.84) * mm});
            skLineSegment(sketch, "E2056", {"start": v(19.4, -1.84) * mm, "end": v(20.77, -1.63) * mm});
            skLineSegment(sketch, "E2057", {"start": v(20.77, -1.63) * mm, "end": v(21.25, -1.05) * mm});
            skLineSegment(sketch, "E2058", {"start": v(21.25, -1.05) * mm, "end": v(21.37, -0.96) * mm});
            skLineSegment(sketch, "E2059", {"start": v(21.37, -0.96) * mm, "end": v(21.65, -0.86) * mm});
            skLineSegment(sketch, "E2060", {"start": v(21.65, -0.86) * mm, "end": v(22.02, -0.8) * mm});
            skLineSegment(sketch, "E2061", {"start": v(22.02, -0.8) * mm, "end": v(22.41, -0.83) * mm});
            skLineSegment(sketch, "E2062", {"start": v(22.41, -0.83) * mm, "end": v(22.54, -0.86) * mm});
            skLineSegment(sketch, "E2063", {"start": v(22.54, -0.86) * mm, "end": v(22.92, -1.13) * mm});
            skLineSegment(sketch, "E2064", {"start": v(22.92, -1.13) * mm, "end": v(23.15, -1.47) * mm});
            skLineSegment(sketch, "E2065", {"start": v(23.15, -1.47) * mm, "end": v(23.29, -1.61) * mm});
            skLineSegment(sketch, "E2066", {"start": v(23.29, -1.61) * mm, "end": v(23.56, -1.96) * mm});
            skLineSegment(sketch, "E2067", {"start": v(23.56, -1.96) * mm, "end": v(23.82, -2.38) * mm});
            skLineSegment(sketch, "E2068", {"start": v(23.82, -2.38) * mm, "end": v(23.94, -2.74) * mm});
            skLineSegment(sketch, "E2069", {"start": v(23.94, -2.74) * mm, "end": v(24.05, -2.87) * mm});
            skLineSegment(sketch, "E2070", {"start": v(24.05, -2.87) * mm, "end": v(24.13, -2.9) * mm});
            skLineSegment(sketch, "E2071", {"start": v(24.13, -2.9) * mm, "end": v(24.58, -3.09) * mm});
            skLineSegment(sketch, "E2072", {"start": v(24.58, -3.09) * mm, "end": v(24.95, -3.32) * mm});
            skLineSegment(sketch, "E2073", {"start": v(24.95, -3.32) * mm, "end": v(25.16, -3.48) * mm});
            skLineSegment(sketch, "E2074", {"start": v(25.16, -3.48) * mm, "end": v(25.4, -3.66) * mm});
            skLineSegment(sketch, "E2075", {"start": v(25.4, -3.66) * mm, "end": v(25.7, -4.03) * mm});
            skLineSegment(sketch, "E2076", {"start": v(25.7, -4.03) * mm, "end": v(25.98, -4.46) * mm});
            skLineSegment(sketch, "E2077", {"start": v(25.98, -4.46) * mm, "end": v(26.2, -5.03) * mm});
            skLineSegment(sketch, "E2078", {"start": v(26.2, -5.03) * mm, "end": v(26.25, -5.68) * mm});
            skLineSegment(sketch, "E2079", {"start": v(26.25, -5.68) * mm, "end": v(26.22, -5.75) * mm});
            skLineSegment(sketch, "E2080", {"start": v(26.22, -5.75) * mm, "end": v(25.93, -6.08) * mm});
            skLineSegment(sketch, "E2081", {"start": v(25.93, -6.08) * mm, "end": v(25.5, -6.18) * mm});
            skLineSegment(sketch, "E2082", {"start": v(25.5, -6.18) * mm, "end": v(25.37, -6.12) * mm});
            skLineSegment(sketch, "E2083", {"start": v(25.37, -6.12) * mm, "end": v(24.84, -5.89) * mm});
            skLineSegment(sketch, "E2084", {"start": v(24.84, -5.89) * mm, "end": v(24, -5.38) * mm});
            skLineSegment(sketch, "E2085", {"start": v(24, -5.38) * mm, "end": v(23.87, -5.1) * mm});
            skLineSegment(sketch, "E2086", {"start": v(23.87, -5.1) * mm, "end": v(23.3, -4.46) * mm});
            skLineSegment(sketch, "E2087", {"start": v(23.3, -4.46) * mm, "end": v(23.2, -4.46) * mm});
            skLineSegment(sketch, "E2088", {"start": v(23.2, -4.46) * mm, "end": v(23.32, -4.97) * mm});
            skLineSegment(sketch, "E2089", {"start": v(23.32, -4.97) * mm, "end": v(23.36, -5.49) * mm});
            skLineSegment(sketch, "E2090", {"start": v(23.36, -5.49) * mm, "end": v(23.4, -6.07) * mm});
            skLineSegment(sketch, "E2091", {"start": v(23.4, -6.07) * mm, "end": v(23.36, -6.7) * mm});
            skLineSegment(sketch, "E2092", {"start": v(23.36, -6.7) * mm, "end": v(23.2, -6.94) * mm});
            skLineSegment(sketch, "E2093", {"start": v(23.2, -6.94) * mm, "end": v(22.74, -7.16) * mm});
            skLineSegment(sketch, "E2094", {"start": v(22.74, -7.16) * mm, "end": v(22.1, -7.1) * mm});
            skLineSegment(sketch, "E2095", {"start": v(22.1, -7.1) * mm, "end": v(21.88, -7.05) * mm});
            skLineSegment(sketch, "E2096", {"start": v(21.88, -7.05) * mm, "end": v(21.62, -6.8) * mm});
            skLineSegment(sketch, "E2097", {"start": v(21.62, -6.8) * mm, "end": v(21.43, -6.55) * mm});
            skLineSegment(sketch, "E2098", {"start": v(21.43, -6.55) * mm, "end": v(21.33, -6.07) * mm});
            skLineSegment(sketch, "E2099", {"start": v(21.33, -6.07) * mm, "end": v(21.11, -5.65) * mm});
            skLineSegment(sketch, "E2100", {"start": v(21.11, -5.65) * mm, "end": v(20.54, -6.08) * mm});
            skLineSegment(sketch, "E2101", {"start": v(20.54, -6.08) * mm, "end": v(20, -6.6) * mm});
            skLineSegment(sketch, "E2102", {"start": v(20, -6.6) * mm, "end": v(19.54, -6.78) * mm});
            skLineSegment(sketch, "E2103", {"start": v(19.54, -6.78) * mm, "end": v(19.05, -6.76) * mm});
            skLineSegment(sketch, "E2104", {"start": v(19.05, -6.76) * mm, "end": v(18.7, -6.54) * mm});
            skLineSegment(sketch, "E2105", {"start": v(18.7, -6.54) * mm, "end": v(18.57, -6.1) * mm});
            skLineSegment(sketch, "E2106", {"start": v(18.57, -6.1) * mm, "end": v(18.63, -5.89) * mm});
            skLineSegment(sketch, "E2107", {"start": v(18.63, -5.89) * mm, "end": v(19.05, -4.9) * mm});
            skLineSegment(sketch, "E2108", {"start": v(19.05, -4.9) * mm, "end": v(19.34, -4.33) * mm});
            skLineSegment(sketch, "E2109", {"start": v(19.34, -4.33) * mm, "end": v(19.66, -3.77) * mm});
            skLineSegment(sketch, "E2110", {"start": v(19.66, -3.77) * mm, "end": v(19.24, -4.14) * mm});
            skLineSegment(sketch, "E2111", {"start": v(24.18, -4.46) * mm, "end": v(24.65, -5.16) * mm});
            skLineSegment(sketch, "E2112", {"start": v(24.65, -5.16) * mm, "end": v(25.3, -5.65) * mm});
            skLineSegment(sketch, "E2113", {"start": v(25.3, -5.65) * mm, "end": v(25.7, -5.7) * mm});
            skLineSegment(sketch, "E2114", {"start": v(25.7, -5.7) * mm, "end": v(25.74, -5.65) * mm});
            skLineSegment(sketch, "E2115", {"start": v(25.74, -5.65) * mm, "end": v(25.75, -4.93) * mm});
            skLineSegment(sketch, "E2116", {"start": v(25.75, -4.93) * mm, "end": v(25.45, -4.4) * mm});
            skLineSegment(sketch, "E2117", {"start": v(25.45, -4.4) * mm, "end": v(25.23, -4.09) * mm});
            skLineSegment(sketch, "E2118", {"start": v(25.23, -4.09) * mm, "end": v(24.95, -3.85) * mm});
            skLineSegment(sketch, "E2119", {"start": v(24.95, -3.85) * mm, "end": v(24.62, -3.56) * mm});
            skLineSegment(sketch, "E2120", {"start": v(24.62, -3.56) * mm, "end": v(24.16, -3.4) * mm});
            skLineSegment(sketch, "E2121", {"start": v(24.16, -3.4) * mm, "end": v(23.97, -3.37) * mm});
            skLineSegment(sketch, "E2122", {"start": v(23.97, -3.37) * mm, "end": v(23.79, -3.35) * mm});
            skLineSegment(sketch, "E2123", {"start": v(23.79, -3.35) * mm, "end": v(23.8, -3.48) * mm});
            skLineSegment(sketch, "E2124", {"start": v(23.8, -3.48) * mm, "end": v(23.9, -3.74) * mm});
            skLineSegment(sketch, "E2125", {"start": v(23.9, -3.74) * mm, "end": v(24.04, -4.13) * mm});
            skLineSegment(sketch, "E2126", {"start": v(24.04, -4.13) * mm, "end": v(24.18, -4.46) * mm});
            skLineSegment(sketch, "E2127", {"start": v(22.17, -3.88) * mm, "end": v(21.96, -4.46) * mm});
            skLineSegment(sketch, "E2128", {"start": v(21.96, -4.46) * mm, "end": v(21.9, -4.8) * mm});
            skLineSegment(sketch, "E2129", {"start": v(21.9, -4.8) * mm, "end": v(21.99, -5.49) * mm});
            skLineSegment(sketch, "E2130", {"start": v(21.99, -5.49) * mm, "end": v(22.07, -6.2) * mm});
            skLineSegment(sketch, "E2131", {"start": v(22.07, -6.2) * mm, "end": v(22.19, -6.5) * mm});
            skLineSegment(sketch, "E2132", {"start": v(22.19, -6.5) * mm, "end": v(22.33, -6.79) * mm});
            skLineSegment(sketch, "E2133", {"start": v(22.33, -6.79) * mm, "end": v(22.36, -6.79) * mm});
            skLineSegment(sketch, "E2134", {"start": v(22.36, -6.79) * mm, "end": v(22.66, -6.74) * mm});
            skLineSegment(sketch, "E2135", {"start": v(22.66, -6.74) * mm, "end": v(22.86, -6.55) * mm});
            skLineSegment(sketch, "E2136", {"start": v(22.86, -6.55) * mm, "end": v(22.94, -6.39) * mm});
            skLineSegment(sketch, "E2137", {"start": v(22.94, -6.39) * mm, "end": v(22.96, -6.07) * mm});
            skLineSegment(sketch, "E2138", {"start": v(22.96, -6.07) * mm, "end": v(22.91, -5.75) * mm});
            skLineSegment(sketch, "E2139", {"start": v(22.91, -5.75) * mm, "end": v(22.85, -5.33) * mm});
            skLineSegment(sketch, "E2140", {"start": v(22.85, -5.33) * mm, "end": v(22.75, -4.72) * mm});
            skLineSegment(sketch, "E2141", {"start": v(22.75, -4.72) * mm, "end": v(22.66, -4.12) * mm});
            skLineSegment(sketch, "E2142", {"start": v(22.66, -4.12) * mm, "end": v(22.65, -3.7) * mm});
            skLineSegment(sketch, "E2143", {"start": v(22.65, -3.7) * mm, "end": v(22.52, -3.49) * mm});
            skLineSegment(sketch, "E2144", {"start": v(22.52, -3.49) * mm, "end": v(22.38, -3.35) * mm});
            skLineSegment(sketch, "E2145", {"start": v(22.38, -3.35) * mm, "end": v(22.22, -3.56) * mm});
            skLineSegment(sketch, "E2146", {"start": v(22.22, -3.56) * mm, "end": v(22.17, -3.88) * mm});
            skLineSegment(sketch, "E2147", {"start": v(20.24, -5.68) * mm, "end": v(20.45, -5.49) * mm});
            skLineSegment(sketch, "E2148", {"start": v(20.45, -5.49) * mm, "end": v(20.61, -5.1) * mm});
            skLineSegment(sketch, "E2149", {"start": v(20.61, -5.1) * mm, "end": v(20.74, -4.64) * mm});
            skLineSegment(sketch, "E2150", {"start": v(20.74, -4.64) * mm, "end": v(20.9, -4.22) * mm});
            skLineSegment(sketch, "E2151", {"start": v(20.9, -4.22) * mm, "end": v(21.03, -3.64) * mm});
            skLineSegment(sketch, "E2152", {"start": v(21.03, -3.64) * mm, "end": v(21.11, -3.1) * mm});
            skLineSegment(sketch, "E2153", {"start": v(21.11, -3.1) * mm, "end": v(20.9, -3.2) * mm});
            skLineSegment(sketch, "E2154", {"start": v(20.9, -3.2) * mm, "end": v(20.77, -3.4) * mm});
            skLineSegment(sketch, "E2155", {"start": v(20.77, -3.4) * mm, "end": v(19.84, -4.7) * mm});
            skLineSegment(sketch, "E2156", {"start": v(19.84, -4.7) * mm, "end": v(19.24, -6.02) * mm});
            skLineSegment(sketch, "E2157", {"start": v(19.24, -6.02) * mm, "end": v(19.18, -6.34) * mm});
            skLineSegment(sketch, "E2158", {"start": v(19.18, -6.34) * mm, "end": v(19.71, -6.28) * mm});
            skLineSegment(sketch, "E2159", {"start": v(19.71, -6.28) * mm, "end": v(20, -6.03) * mm});
            skLineSegment(sketch, "E2160", {"start": v(20, -6.03) * mm, "end": v(20.24, -5.68) * mm});
            skLineSegment(sketch, "E2161", {"start": v(20.13, -2.82) * mm, "end": v(20.27, -2.63) * mm});
            skLineSegment(sketch, "E2162", {"start": v(20.27, -2.63) * mm, "end": v(20.5, -2.42) * mm});
            skLineSegment(sketch, "E2163", {"start": v(20.5, -2.42) * mm, "end": v(20.53, -2.31) * mm});
            skLineSegment(sketch, "E2164", {"start": v(20.53, -2.31) * mm, "end": v(20.56, -2.1) * mm});
            skLineSegment(sketch, "E2165", {"start": v(20.56, -2.1) * mm, "end": v(19.48, -2.32) * mm});
            skLineSegment(sketch, "E2166", {"start": v(19.48, -2.32) * mm, "end": v(18.41, -2.58) * mm});
            skLineSegment(sketch, "E2167", {"start": v(18.41, -2.58) * mm, "end": v(18.07, -2.92) * mm});
            skLineSegment(sketch, "E2168", {"start": v(18.07, -2.92) * mm, "end": v(17.83, -3.48) * mm});
            skLineSegment(sketch, "E2169", {"start": v(17.83, -3.48) * mm, "end": v(17.76, -3.89) * mm});
            skLineSegment(sketch, "E2170", {"start": v(17.76, -3.89) * mm, "end": v(17.83, -4.14) * mm});
            skLineSegment(sketch, "E2171", {"start": v(17.83, -4.14) * mm, "end": v(18.96, -3.84) * mm});
            skLineSegment(sketch, "E2172", {"start": v(18.96, -3.84) * mm, "end": v(19.87, -3.08) * mm});
            skLineSegment(sketch, "E2173", {"start": v(19.87, -3.08) * mm, "end": v(20.13, -2.82) * mm});
            skLineSegment(sketch, "E2174", {"start": v(23.7, -1.7) * mm, "end": v(23.9, -1.73) * mm});
            skLineSegment(sketch, "E2175", {"start": v(23.9, -1.73) * mm, "end": v(23.94, -1.7) * mm});
            skLineSegment(sketch, "E2176", {"start": v(23.94, -1.7) * mm, "end": v(24.4, -1.53) * mm});
            skLineSegment(sketch, "E2177", {"start": v(24.4, -1.53) * mm, "end": v(24.82, -1.42) * mm});
            skLineSegment(sketch, "E2178", {"start": v(24.82, -1.42) * mm, "end": v(25.07, -1.38) * mm});
            skLineSegment(sketch, "E2179", {"start": v(25.07, -1.38) * mm, "end": v(25.37, -1.36) * mm});
            skLineSegment(sketch, "E2180", {"start": v(25.37, -1.36) * mm, "end": v(25.84, -1.41) * mm});
            skLineSegment(sketch, "E2181", {"start": v(25.84, -1.41) * mm, "end": v(26.33, -1.52) * mm});
            skLineSegment(sketch, "E2182", {"start": v(26.33, -1.52) * mm, "end": v(26.88, -1.78) * mm});
            skLineSegment(sketch, "E2183", {"start": v(26.88, -1.78) * mm, "end": v(27.36, -2.18) * mm});
            skLineSegment(sketch, "E2184", {"start": v(27.36, -2.18) * mm, "end": v(27.38, -2.24) * mm});
            skLineSegment(sketch, "E2185", {"start": v(27.38, -2.24) * mm, "end": v(27.4, -2.66) * mm});
            skLineSegment(sketch, "E2186", {"start": v(27.4, -2.66) * mm, "end": v(27.17, -3.03) * mm});
            skLineSegment(sketch, "E2187", {"start": v(27.17, -3.03) * mm, "end": v(27.04, -3.1) * mm});
            skLineSegment(sketch, "E2188", {"start": v(27.04, -3.1) * mm, "end": v(26.51, -3.32) * mm});
            skLineSegment(sketch, "E2189", {"start": v(26.51, -3.32) * mm, "end": v(25.56, -3.56) * mm});
            skLineSegment(sketch, "E2190", {"start": v(25.56, -3.56) * mm, "end": v(25.27, -3.45) * mm});
            skLineSegment(sketch, "E2191", {"start": v(25.27, -3.45) * mm, "end": v(24.45, -3.37) * mm});
            skLineSegment(sketch, "E2192", {"start": v(24.45, -3.37) * mm, "end": v(24.37, -3.45) * mm});
            skLineSegment(sketch, "E2193", {"start": v(24.37, -3.45) * mm, "end": v(24.27, -3.38) * mm});
            skLineSegment(sketch, "E2194", {"start": v(24.27, -3.38) * mm, "end": v(24, -3.21) * mm});
            skLineSegment(sketch, "E2195", {"start": v(24, -3.21) * mm, "end": v(23.65, -2.97) * mm});
            skLineSegment(sketch, "E2196", {"start": v(23.65, -2.97) * mm, "end": v(23.3, -2.69) * mm});
            skLineSegment(sketch, "E2197", {"start": v(23.3, -2.69) * mm, "end": v(23.05, -2.39) * mm});
            skLineSegment(sketch, "E2198", {"start": v(23.05, -2.39) * mm, "end": v(22.98, -2.1) * mm});
            skLineSegment(sketch, "E2199", {"start": v(22.98, -2.1) * mm, "end": v(23.17, -1.87) * mm});
            skLineSegment(sketch, "E2200", {"start": v(23.17, -1.87) * mm, "end": v(23.7, -1.7) * mm});
            skLineSegment(sketch, "E2201", {"start": v(25.06, -2.8) * mm, "end": v(25.89, -2.96) * mm});
            skLineSegment(sketch, "E2202", {"start": v(25.89, -2.96) * mm, "end": v(26.7, -2.87) * mm});
            skLineSegment(sketch, "E2203", {"start": v(26.7, -2.87) * mm, "end": v(27.01, -2.63) * mm});
            skLineSegment(sketch, "E2204", {"start": v(27.01, -2.63) * mm, "end": v(27.01, -2.55) * mm});
            skLineSegment(sketch, "E2205", {"start": v(27.01, -2.55) * mm, "end": v(26.51, -2.04) * mm});
            skLineSegment(sketch, "E2206", {"start": v(26.51, -2.04) * mm, "end": v(25.93, -1.87) * mm});
            skLineSegment(sketch, "E2207", {"start": v(25.93, -1.87) * mm, "end": v(25.55, -1.8) * mm});
            skLineSegment(sketch, "E2208", {"start": v(25.55, -1.8) * mm, "end": v(25.19, -1.84) * mm});
            skLineSegment(sketch, "E2209", {"start": v(25.19, -1.84) * mm, "end": v(24.75, -1.87) * mm});
            skLineSegment(sketch, "E2210", {"start": v(24.75, -1.87) * mm, "end": v(24.32, -2.08) * mm});
            skLineSegment(sketch, "E2211", {"start": v(24.32, -2.08) * mm, "end": v(24.18, -2.18) * mm});
            skLineSegment(sketch, "E2212", {"start": v(24.18, -2.18) * mm, "end": v(24.05, -2.29) * mm});
            skLineSegment(sketch, "E2213", {"start": v(24.05, -2.29) * mm, "end": v(24.15, -2.37) * mm});
            skLineSegment(sketch, "E2214", {"start": v(24.15, -2.37) * mm, "end": v(24.4, -2.5) * mm});
            skLineSegment(sketch, "E2215", {"start": v(24.4, -2.5) * mm, "end": v(24.73, -2.66) * mm});
            skLineSegment(sketch, "E2216", {"start": v(24.73, -2.66) * mm, "end": v(25.06, -2.8) * mm});
            skLineSegment(sketch, "E2217", {"start": v(23.36, -2.05) * mm, "end": v(23.42, -1.73) * mm});
            skLineSegment(sketch, "E2218", {"start": v(23.42, -1.73) * mm, "end": v(23.42, -1.68) * mm});
            skLineSegment(sketch, "E2219", {"start": v(23.42, -1.68) * mm, "end": v(23.24, -1.37) * mm});
            skLineSegment(sketch, "E2220", {"start": v(23.24, -1.37) * mm, "end": v(22.91, -1.26) * mm});
            skLineSegment(sketch, "E2221", {"start": v(22.91, -1.26) * mm, "end": v(22.57, -1.47) * mm});
            skLineSegment(sketch, "E2222", {"start": v(22.57, -1.47) * mm, "end": v(22.54, -1.68) * mm});
            skLineSegment(sketch, "E2223", {"start": v(22.54, -1.68) * mm, "end": v(22.54, -1.92) * mm});
            skLineSegment(sketch, "E2224", {"start": v(22.54, -1.92) * mm, "end": v(22.49, -2.07) * mm});
            skLineSegment(sketch, "E2225", {"start": v(22.49, -2.07) * mm, "end": v(22.44, -2.08) * mm});
            skLineSegment(sketch, "E2226", {"start": v(22.44, -2.08) * mm, "end": v(22.35, -1.9) * mm});
            skLineSegment(sketch, "E2227", {"start": v(22.35, -1.9) * mm, "end": v(22.28, -1.63) * mm});
            skLineSegment(sketch, "E2228", {"start": v(22.28, -1.63) * mm, "end": v(21.99, -1.36) * mm});
            skLineSegment(sketch, "E2229", {"start": v(21.99, -1.36) * mm, "end": v(21.56, -1.28) * mm});
            skLineSegment(sketch, "E2230", {"start": v(21.56, -1.28) * mm, "end": v(21.4, -1.33) * mm});
            skLineSegment(sketch, "E2231", {"start": v(21.4, -1.33) * mm, "end": v(21.3, -1.47) * mm});
            skLineSegment(sketch, "E2232", {"start": v(21.3, -1.47) * mm, "end": v(21.33, -1.7) * mm});
            skLineSegment(sketch, "E2233", {"start": v(21.33, -1.7) * mm, "end": v(21.56, -2.23) * mm});
            skLineSegment(sketch, "E2234", {"start": v(21.56, -2.23) * mm, "end": v(21.96, -2.5) * mm});
            skLineSegment(sketch, "E2235", {"start": v(21.96, -2.5) * mm, "end": v(22.15, -2.55) * mm});
            skLineSegment(sketch, "E2236", {"start": v(22.15, -2.55) * mm, "end": v(22.33, -2.72) * mm});
            skLineSegment(sketch, "E2237", {"start": v(22.33, -2.72) * mm, "end": v(22.49, -2.87) * mm});
            skLineSegment(sketch, "E2238", {"start": v(22.49, -2.87) * mm, "end": v(22.91, -2.47) * mm});
            skLineSegment(sketch, "E2239", {"start": v(22.91, -2.47) * mm, "end": v(23.17, -2.3) * mm});
            skLineSegment(sketch, "E2240", {"start": v(23.17, -2.3) * mm, "end": v(23.36, -2.05) * mm});
            skSolve(sketch);
        }
        {
            var Q0;
            {var subQ18=sQuery(id+"F0.wireOp",EDGE,"E1925");Q0=makeQuery(id+"F0.imprint","IMPRINT",FACE,{"disambiguationData":[TD([[makeQuery(id+"F0.imprint","IMPRINT",EDGE,{"derivedFrom":subQ18}),1.0]])]});}
            var Q1;
            {var subQ8=sQuery(id+"F0.wireOp",EDGE,"E2068");Q1=makeQuery(id+"F0.imprint","IMPRINT",FACE,{"disambiguationData":[TD([[makeQuery(id+"F0.imprint","IMPRINT",EDGE,{"derivedFrom":subQ8}),-1.0]])]});}
            var Q2;
            {var subQ11=sQuery(id+"F0.wireOp",EDGE,"E2068");Q2=makeQuery(id+"F0.imprint","IMPRINT",FACE,{"disambiguationData":[TD([[makeQuery(id+"F0.imprint","IMPRINT",EDGE,{"derivedFrom":subQ11}),1.0]])]});}
            var Q3;
            Q3=makeQuery(id+"F0.imprint","IMPRINT",FACE,{"disambiguationData":[TD([[makeQuery(id+"F0.imprint","IMPRINT",EDGE,{"derivedFrom":sQuery(id+"F0.wireOp",EDGE,"E1910")}),-1.0]])]});
            var Q4;
            {var subQ24=sQuery(id+"F0.wireOp",EDGE,"E1925");Q4=makeQuery(id+"F0.imprint","IMPRINT",FACE,{"disambiguationData":[TD([[makeQuery(id+"F0.imprint","IMPRINT",EDGE,{"derivedFrom":subQ24}),-1.0]])]});}
            var Q5;
            {var subQ9=sQuery(id+"F0.wireOp",EDGE,"E2197");Q5=makeQuery(id+"F0.imprint","IMPRINT",FACE,{"disambiguationData":[TD([[makeQuery(id+"F0.imprint","IMPRINT",EDGE,{"derivedFrom":subQ9}),-1.0]])]});}
            var Q6;
            {var subQ3=sQuery(id+"F0.wireOp",EDGE,"E2174");Q6=makeQuery(id+"F0.imprint","IMPRINT",FACE,{"disambiguationData":[TD([[makeQuery(id+"F0.imprint","IMPRINT",EDGE,{"derivedFrom":subQ3}),-1.0]])]});}
            var Q7;
            Q7=makeQuery(id+"F0.imprint","IMPRINT",FACE,{"disambiguationData":[TD([[makeQuery(id+"F0.imprint","IMPRINT",EDGE,{"derivedFrom":sQuery(id+"F0.wireOp",EDGE,"E0")}),1.0]])]});
            var Q8;
            Q8=makeQuery(id+"F0.imprint","IMPRINT",FACE,{"disambiguationData":[TD([[makeQuery(id+"F0.imprint","IMPRINT",EDGE,{"derivedFrom":sQuery(id+"F0.wireOp",EDGE,"E1295")}),1.0]])]});
            var Q9;
            Q9=makeQuery(id+"F0.imprint","IMPRINT",FACE,{"disambiguationData":[TD([[makeQuery(id+"F0.imprint","IMPRINT",EDGE,{"derivedFrom":sQuery(id+"F0.wireOp",EDGE,"E1402")}),1.0]])]});
            var Q10;
            {var subQ5=sQuery(id+"F0.wireOp",EDGE,"E1570");Q10=makeQuery(id+"F0.imprint","IMPRINT",FACE,{"disambiguationData":[TD([[makeQuery(id+"F0.imprint","IMPRINT",EDGE,{"derivedFrom":subQ5}),1.0]])]});}
            var Q11;
            Q11=makeQuery(id+"F0.imprint","IMPRINT",FACE,{"disambiguationData":[TD([[makeQuery(id+"F0.imprint","IMPRINT",EDGE,{"derivedFrom":sQuery(id+"F0.wireOp",EDGE,"E782")}),1.0]])]});
            var Q12;
            Q12=makeQuery(id+"F0.imprint","IMPRINT",FACE,{"disambiguationData":[TD([[makeQuery(id+"F0.imprint","IMPRINT",EDGE,{"derivedFrom":sQuery(id+"F0.wireOp",EDGE,"E536")}),1.0]])]});
            var Q13;
            Q13=makeQuery(id+"F0.imprint","IMPRINT",FACE,{"disambiguationData":[TD([[makeQuery(id+"F0.imprint","IMPRINT",EDGE,{"derivedFrom":sQuery(id+"F0.wireOp",EDGE,"E322")}),1.0]])]});
            var Q14;
            Q14=makeQuery(id+"F0.imprint","IMPRINT",FACE,{"disambiguationData":[TD([[makeQuery(id+"F0.imprint","IMPRINT",EDGE,{"derivedFrom":sQuery(id+"F0.wireOp",EDGE,"E1776")}),1.0]])]});
            var Q15;
            {var subQ4=sQuery(id+"F0.wireOp",EDGE,"E1904");Q15=makeQuery(id+"F0.imprint","IMPRINT",FACE,{"disambiguationData":[TD([[makeQuery(id+"F0.imprint","IMPRINT",EDGE,{"derivedFrom":subQ4}),1.0]])]});}
            var Q16;
            Q16=makeQuery(id+"F0.imprint","IMPRINT",FACE,{"disambiguationData":[TD([[makeQuery(id+"F0.imprint","IMPRINT",EDGE,{"derivedFrom":sQuery(id+"F0.wireOp",EDGE,"E987")}),1.0]])]});
            extrude(context, id + "F1", {"entities" : qUnion([Q0, Q1, Q2, Q3, Q4, Q5, Q6, Q7, Q8, Q9, Q10, Q11, Q12, Q13, Q14, Q15, Q16]), "depth" : 2 * mm});
        }
        {
            var Q0;
            Q0=makeQuery(id+"F1.opExtrude","CAP_FACE",FACE,{"disambiguationData":[OSD([sQuery(id+"F0.wireOp",EDGE,"E1569"),sQuery(id+"F0.wireOp",EDGE,"E1570"),sQuery(id+"F0.wireOp",EDGE,"E1571"),sQuery(id+"F0.wireOp",EDGE,"E1572"),sQuery(id+"F0.wireOp",EDGE,"E1573"),sQuery(id+"F0.wireOp",EDGE,"E1574"),sQuery(id+"F0.wireOp",EDGE,"E1575"),sQuery(id+"F0.wireOp",EDGE,"E1576"),sQuery(id+"F0.wireOp",EDGE,"E1577"),sQuery(id+"F0.wireOp",EDGE,"E1578"),sQuery(id+"F0.wireOp",EDGE,"E1579"),sQuery(id+"F0.wireOp",EDGE,"E1580"),sQuery(id+"F0.wireOp",EDGE,"E1581"),sQuery(id+"F0.wireOp",EDGE,"E1582"),sQuery(id+"F0.wireOp",EDGE,"E1583"),sQuery(id+"F0.wireOp",EDGE,"E1584"),sQuery(id+"F0.wireOp",EDGE,"E1585"),sQuery(id+"F0.wireOp",EDGE,"E1586"),sQuery(id+"F0.wireOp",EDGE,"E1587"),sQuery(id+"F0.wireOp",EDGE,"E1588"),sQuery(id+"F0.wireOp",EDGE,"E1589"),sQuery(id+"F0.wireOp",EDGE,"E1590"),sQuery(id+"F0.wireOp",EDGE,"E1591"),sQuery(id+"F0.wireOp",EDGE,"E1592"),sQuery(id+"F0.wireOp",EDGE,"E1593"),sQuery(id+"F0.wireOp",EDGE,"E1594"),sQuery(id+"F0.wireOp",EDGE,"E1595"),sQuery(id+"F0.wireOp",EDGE,"E1596"),sQuery(id+"F0.wireOp",EDGE,"E1597"),sQuery(id+"F0.wireOp",EDGE,"E1598"),sQuery(id+"F0.wireOp",EDGE,"E1599"),sQuery(id+"F0.wireOp",EDGE,"E1600"),sQuery(id+"F0.wireOp",EDGE,"E1601"),sQuery(id+"F0.wireOp",EDGE,"E1602"),sQuery(id+"F0.wireOp",EDGE,"E1603"),sQuery(id+"F0.wireOp",EDGE,"E1604"),sQuery(id+"F0.wireOp",EDGE,"E1605"),sQuery(id+"F0.wireOp",EDGE,"E1606"),sQuery(id+"F0.wireOp",EDGE,"E1607"),sQuery(id+"F0.wireOp",EDGE,"E1608"),sQuery(id+"F0.wireOp",EDGE,"E1609"),sQuery(id+"F0.wireOp",EDGE,"E1610"),sQuery(id+"F0.wireOp",EDGE,"E1611"),sQuery(id+"F0.wireOp",EDGE,"E1612"),sQuery(id+"F0.wireOp",EDGE,"E1613"),sQuery(id+"F0.wireOp",EDGE,"E1614"),sQuery(id+"F0.wireOp",EDGE,"E1615"),sQuery(id+"F0.wireOp",EDGE,"E1616"),sQuery(id+"F0.wireOp",EDGE,"E1617"),sQuery(id+"F0.wireOp",EDGE,"E1618"),sQuery(id+"F0.wireOp",EDGE,"E1619"),sQuery(id+"F0.wireOp",EDGE,"E1620"),sQuery(id+"F0.wireOp",EDGE,"E1621"),sQuery(id+"F0.wireOp",EDGE,"E1622"),sQuery(id+"F0.wireOp",EDGE,"E1623"),sQuery(id+"F0.wireOp",EDGE,"E1624"),sQuery(id+"F0.wireOp",EDGE,"E1625"),sQuery(id+"F0.wireOp",EDGE,"E1626"),sQuery(id+"F0.wireOp",EDGE,"E1627"),sQuery(id+"F0.wireOp",EDGE,"E1628"),sQuery(id+"F0.wireOp",EDGE,"E1629"),sQuery(id+"F0.wireOp",EDGE,"E1630"),sQuery(id+"F0.wireOp",EDGE,"E1631"),sQuery(id+"F0.wireOp",EDGE,"E1632"),sQuery(id+"F0.wireOp",EDGE,"E1633"),sQuery(id+"F0.wireOp",EDGE,"E1634"),sQuery(id+"F0.wireOp",EDGE,"E1635"),sQuery(id+"F0.wireOp",EDGE,"E1636"),sQuery(id+"F0.wireOp",EDGE,"E1637"),sQuery(id+"F0.wireOp",EDGE,"E1638"),sQuery(id+"F0.wireOp",EDGE,"E1639"),sQuery(id+"F0.wireOp",EDGE,"E1640"),sQuery(id+"F0.wireOp",EDGE,"E1641"),sQuery(id+"F0.wireOp",EDGE,"E1642"),sQuery(id+"F0.wireOp",EDGE,"E1643"),sQuery(id+"F0.wireOp",EDGE,"E1644"),sQuery(id+"F0.wireOp",EDGE,"E1645"),sQuery(id+"F0.wireOp",EDGE,"E1646"),sQuery(id+"F0.wireOp",EDGE,"E1647"),sQuery(id+"F0.wireOp",EDGE,"E1648"),sQuery(id+"F0.wireOp",EDGE,"E1649"),sQuery(id+"F0.wireOp",EDGE,"E1650"),sQuery(id+"F0.wireOp",EDGE,"E1651"),sQuery(id+"F0.wireOp",EDGE,"E1652"),sQuery(id+"F0.wireOp",EDGE,"E1653"),sQuery(id+"F0.wireOp",EDGE,"E1654"),sQuery(id+"F0.wireOp",EDGE,"E1655"),sQuery(id+"F0.wireOp",EDGE,"E1656"),sQuery(id+"F0.wireOp",EDGE,"E1657"),sQuery(id+"F0.wireOp",EDGE,"E1658"),sQuery(id+"F0.wireOp",EDGE,"E1659"),sQuery(id+"F0.wireOp",EDGE,"E1660"),sQuery(id+"F0.wireOp",EDGE,"E1661"),sQuery(id+"F0.wireOp",EDGE,"E1662"),sQuery(id+"F0.wireOp",EDGE,"E1663"),sQuery(id+"F0.wireOp",EDGE,"E1664"),sQuery(id+"F0.wireOp",EDGE,"E1665"),sQuery(id+"F0.wireOp",EDGE,"E1666"),sQuery(id+"F0.wireOp",EDGE,"E1667"),sQuery(id+"F0.wireOp",EDGE,"E1668"),sQuery(id+"F0.wireOp",EDGE,"E1669"),sQuery(id+"F0.wireOp",EDGE,"E1670"),sQuery(id+"F0.wireOp",EDGE,"E1671"),sQuery(id+"F0.wireOp",EDGE,"E1672"),sQuery(id+"F0.wireOp",EDGE,"E1673"),sQuery(id+"F0.wireOp",EDGE,"E1674"),sQuery(id+"F0.wireOp",EDGE,"E1675"),sQuery(id+"F0.wireOp",EDGE,"E1676"),sQuery(id+"F0.wireOp",EDGE,"E1677"),sQuery(id+"F0.wireOp",EDGE,"E1678"),sQuery(id+"F0.wireOp",EDGE,"E1679"),sQuery(id+"F0.wireOp",EDGE,"E1680"),sQuery(id+"F0.wireOp",EDGE,"E1681"),sQuery(id+"F0.wireOp",EDGE,"E1682"),sQuery(id+"F0.wireOp",EDGE,"E1683"),sQuery(id+"F0.wireOp",EDGE,"E1684"),sQuery(id+"F0.wireOp",EDGE,"E1685"),sQuery(id+"F0.wireOp",EDGE,"E1686"),sQuery(id+"F0.wireOp",EDGE,"E1687"),sQuery(id+"F0.wireOp",EDGE,"E1688"),sQuery(id+"F0.wireOp",EDGE,"E1689"),sQuery(id+"F0.wireOp",EDGE,"E1690"),sQuery(id+"F0.wireOp",EDGE,"E1691"),sQuery(id+"F0.wireOp",EDGE,"E1692"),sQuery(id+"F0.wireOp",EDGE,"E1693"),sQuery(id+"F0.wireOp",EDGE,"E1694"),sQuery(id+"F0.wireOp",EDGE,"E1695"),sQuery(id+"F0.wireOp",EDGE,"E1696"),sQuery(id+"F0.wireOp",EDGE,"E1697"),sQuery(id+"F0.wireOp",EDGE,"E1698"),sQuery(id+"F0.wireOp",EDGE,"E1699"),sQuery(id+"F0.wireOp",EDGE,"E1700"),sQuery(id+"F0.wireOp",EDGE,"E1701"),sQuery(id+"F0.wireOp",EDGE,"E1702"),sQuery(id+"F0.wireOp",EDGE,"E1703"),sQuery(id+"F0.wireOp",EDGE,"E1704"),sQuery(id+"F0.wireOp",EDGE,"E1705"),sQuery(id+"F0.wireOp",EDGE,"E1706"),sQuery(id+"F0.wireOp",EDGE,"E1707"),sQuery(id+"F0.wireOp",EDGE,"E1708"),sQuery(id+"F0.wireOp",EDGE,"E1709"),sQuery(id+"F0.wireOp",EDGE,"E1710"),sQuery(id+"F0.wireOp",EDGE,"E1711"),sQuery(id+"F0.wireOp",EDGE,"E1712"),sQuery(id+"F0.wireOp",EDGE,"E1713"),sQuery(id+"F0.wireOp",EDGE,"E1714"),sQuery(id+"F0.wireOp",EDGE,"E1715"),sQuery(id+"F0.wireOp",EDGE,"E1716"),sQuery(id+"F0.wireOp",EDGE,"E1717"),sQuery(id+"F0.wireOp",EDGE,"E1718"),sQuery(id+"F0.wireOp",EDGE,"E1719"),sQuery(id+"F0.wireOp",EDGE,"E1720"),sQuery(id+"F0.wireOp",EDGE,"E1721"),sQuery(id+"F0.wireOp",EDGE,"E1722"),sQuery(id+"F0.wireOp",EDGE,"E1723"),sQuery(id+"F0.wireOp",EDGE,"E1724"),sQuery(id+"F0.wireOp",EDGE,"E1725"),sQuery(id+"F0.wireOp",EDGE,"E1726"),sQuery(id+"F0.wireOp",EDGE,"E1727"),sQuery(id+"F0.wireOp",EDGE,"E1728"),sQuery(id+"F0.wireOp",EDGE,"E1729"),sQuery(id+"F0.wireOp",EDGE,"E1730"),sQuery(id+"F0.wireOp",EDGE,"E1731"),sQuery(id+"F0.wireOp",EDGE,"E1732"),sQuery(id+"F0.wireOp",EDGE,"E1733"),sQuery(id+"F0.wireOp",EDGE,"E1734"),sQuery(id+"F0.wireOp",EDGE,"E1735"),sQuery(id+"F0.wireOp",EDGE,"E1736"),sQuery(id+"F0.wireOp",EDGE,"E1737"),sQuery(id+"F0.wireOp",EDGE,"E1738"),sQuery(id+"F0.wireOp",EDGE,"E1739"),sQuery(id+"F0.wireOp",EDGE,"E1740"),sQuery(id+"F0.wireOp",EDGE,"E1741"),sQuery(id+"F0.wireOp",EDGE,"E1742"),sQuery(id+"F0.wireOp",EDGE,"E1743"),sQuery(id+"F0.wireOp",EDGE,"E1744"),sQuery(id+"F0.wireOp",EDGE,"E1745"),sQuery(id+"F0.wireOp",EDGE,"E1746"),sQuery(id+"F0.wireOp",EDGE,"E1747"),sQuery(id+"F0.wireOp",EDGE,"E1748"),sQuery(id+"F0.wireOp",EDGE,"E1749"),sQuery(id+"F0.wireOp",EDGE,"E1750"),sQuery(id+"F0.wireOp",EDGE,"E1751"),sQuery(id+"F0.wireOp",EDGE,"E1752"),sQuery(id+"F0.wireOp",EDGE,"E1753"),sQuery(id+"F0.wireOp",EDGE,"E1754"),sQuery(id+"F0.wireOp",EDGE,"E1755"),sQuery(id+"F0.wireOp",EDGE,"E1756"),sQuery(id+"F0.wireOp",EDGE,"E1757"),sQuery(id+"F0.wireOp",EDGE,"E1758"),sQuery(id+"F0.wireOp",EDGE,"E1759"),sQuery(id+"F0.wireOp",EDGE,"E1760"),sQuery(id+"F0.wireOp",EDGE,"E1761"),sQuery(id+"F0.wireOp",EDGE,"E1762"),sQuery(id+"F0.wireOp",EDGE,"E1763"),sQuery(id+"F0.wireOp",EDGE,"E1764"),sQuery(id+"F0.wireOp",EDGE,"E1765"),sQuery(id+"F0.wireOp",EDGE,"E1766"),sQuery(id+"F0.wireOp",EDGE,"E1767"),sQuery(id+"F0.wireOp",EDGE,"E1768"),sQuery(id+"F0.wireOp",EDGE,"E1769"),sQuery(id+"F0.wireOp",EDGE,"E1770"),sQuery(id+"F0.wireOp",EDGE,"E1771"),sQuery(id+"F0.wireOp",EDGE,"E1772"),sQuery(id+"F0.wireOp",EDGE,"E1773"),sQuery(id+"F0.wireOp",EDGE,"E1774"),sQuery(id+"F0.wireOp",EDGE,"E1775"),sQuery(id+"F0.wireOp",EDGE,"E1776"),sQuery(id+"F0.wireOp",EDGE,"E1777"),sQuery(id+"F0.wireOp",EDGE,"E1778"),sQuery(id+"F0.wireOp",EDGE,"E1779"),sQuery(id+"F0.wireOp",EDGE,"E1780"),sQuery(id+"F0.wireOp",EDGE,"E1781"),sQuery(id+"F0.wireOp",EDGE,"E1782"),sQuery(id+"F0.wireOp",EDGE,"E1783"),sQuery(id+"F0.wireOp",EDGE,"E1784"),sQuery(id+"F0.wireOp",EDGE,"E1785"),sQuery(id+"F0.wireOp",EDGE,"E1786"),sQuery(id+"F0.wireOp",EDGE,"E1787"),sQuery(id+"F0.wireOp",EDGE,"E1788"),sQuery(id+"F0.wireOp",EDGE,"E1789"),sQuery(id+"F0.wireOp",EDGE,"E1790"),sQuery(id+"F0.wireOp",EDGE,"E1791"),sQuery(id+"F0.wireOp",EDGE,"E1792"),sQuery(id+"F0.wireOp",EDGE,"E1793"),sQuery(id+"F0.wireOp",EDGE,"E1794"),sQuery(id+"F0.wireOp",EDGE,"E1795"),sQuery(id+"F0.wireOp",EDGE,"E1796"),sQuery(id+"F0.wireOp",EDGE,"E1797"),sQuery(id+"F0.wireOp",EDGE,"E1798"),sQuery(id+"F0.wireOp",EDGE,"E1799"),sQuery(id+"F0.wireOp",EDGE,"E1800"),sQuery(id+"F0.wireOp",EDGE,"E1801"),sQuery(id+"F0.wireOp",EDGE,"E1802"),sQuery(id+"F0.wireOp",EDGE,"E1803"),sQuery(id+"F0.wireOp",EDGE,"E1804"),sQuery(id+"F0.wireOp",EDGE,"E1805"),sQuery(id+"F0.wireOp",EDGE,"E1806"),sQuery(id+"F0.wireOp",EDGE,"E1807"),sQuery(id+"F0.wireOp",EDGE,"E1808"),sQuery(id+"F0.wireOp",EDGE,"E1809"),sQuery(id+"F0.wireOp",EDGE,"E1810"),sQuery(id+"F0.wireOp",EDGE,"E1811"),sQuery(id+"F0.wireOp",EDGE,"E1812"),sQuery(id+"F0.wireOp",EDGE,"E1813"),sQuery(id+"F0.wireOp",EDGE,"E1814"),sQuery(id+"F0.wireOp",EDGE,"E1815"),sQuery(id+"F0.wireOp",EDGE,"E1816"),sQuery(id+"F0.wireOp",EDGE,"E1817"),sQuery(id+"F0.wireOp",EDGE,"E1818"),sQuery(id+"F0.wireOp",EDGE,"E1819"),sQuery(id+"F0.wireOp",EDGE,"E1820"),sQuery(id+"F0.wireOp",EDGE,"E1821"),sQuery(id+"F0.wireOp",EDGE,"E1822"),sQuery(id+"F0.wireOp",EDGE,"E1823"),sQuery(id+"F0.wireOp",EDGE,"E1824"),sQuery(id+"F0.wireOp",EDGE,"E1825"),sQuery(id+"F0.wireOp",EDGE,"E1826"),sQuery(id+"F0.wireOp",EDGE,"E1827"),sQuery(id+"F0.wireOp",EDGE,"E1828"),sQuery(id+"F0.wireOp",EDGE,"E1829"),sQuery(id+"F0.wireOp",EDGE,"E1830"),sQuery(id+"F0.wireOp",EDGE,"E1831"),sQuery(id+"F0.wireOp",EDGE,"E1832"),sQuery(id+"F0.wireOp",EDGE,"E1833"),sQuery(id+"F0.wireOp",EDGE,"E1834"),sQuery(id+"F0.wireOp",EDGE,"E1835"),sQuery(id+"F0.wireOp",EDGE,"E1836"),sQuery(id+"F0.wireOp",EDGE,"E1837"),sQuery(id+"F0.wireOp",EDGE,"E1838"),sQuery(id+"F0.wireOp",EDGE,"E1839"),sQuery(id+"F0.wireOp",EDGE,"E1840"),sQuery(id+"F0.wireOp",EDGE,"E1841"),sQuery(id+"F0.wireOp",EDGE,"E1842"),sQuery(id+"F0.wireOp",EDGE,"E1843"),sQuery(id+"F0.wireOp",EDGE,"E1844"),sQuery(id+"F0.wireOp",EDGE,"E1845"),sQuery(id+"F0.wireOp",EDGE,"E1846"),sQuery(id+"F0.wireOp",EDGE,"E1847"),sQuery(id+"F0.wireOp",EDGE,"E1848"),sQuery(id+"F0.wireOp",EDGE,"E1849"),sQuery(id+"F0.wireOp",EDGE,"E1850"),sQuery(id+"F0.wireOp",EDGE,"E1851"),sQuery(id+"F0.wireOp",EDGE,"E1852"),sQuery(id+"F0.wireOp",EDGE,"E1853"),sQuery(id+"F0.wireOp",EDGE,"E1854"),sQuery(id+"F0.wireOp",EDGE,"E1855"),sQuery(id+"F0.wireOp",EDGE,"E1856"),sQuery(id+"F0.wireOp",EDGE,"E1857"),sQuery(id+"F0.wireOp",EDGE,"E1858"),sQuery(id+"F0.wireOp",EDGE,"E1859"),sQuery(id+"F0.wireOp",EDGE,"E1860"),sQuery(id+"F0.wireOp",EDGE,"E1861"),sQuery(id+"F0.wireOp",EDGE,"E1862"),sQuery(id+"F0.wireOp",EDGE,"E1863"),sQuery(id+"F0.wireOp",EDGE,"E1864"),sQuery(id+"F0.wireOp",EDGE,"E1865"),sQuery(id+"F0.wireOp",EDGE,"E1866"),sQuery(id+"F0.wireOp",EDGE,"E1867"),sQuery(id+"F0.wireOp",EDGE,"E1868"),sQuery(id+"F0.wireOp",EDGE,"E1869"),sQuery(id+"F0.wireOp",EDGE,"E1870"),sQuery(id+"F0.wireOp",EDGE,"E1871"),sQuery(id+"F0.wireOp",EDGE,"E1872"),sQuery(id+"F0.wireOp",EDGE,"E1873"),sQuery(id+"F0.wireOp",EDGE,"E1874"),sQuery(id+"F0.wireOp",EDGE,"E1875"),sQuery(id+"F0.wireOp",EDGE,"E1876"),sQuery(id+"F0.wireOp",EDGE,"E1877"),sQuery(id+"F0.wireOp",EDGE,"E1878"),sQuery(id+"F0.wireOp",EDGE,"E1879"),sQuery(id+"F0.wireOp",EDGE,"E1880"),sQuery(id+"F0.wireOp",EDGE,"E1881"),sQuery(id+"F0.wireOp",EDGE,"E1882"),sQuery(id+"F0.wireOp",EDGE,"E1883"),sQuery(id+"F0.wireOp",EDGE,"E1884"),sQuery(id+"F0.wireOp",EDGE,"E1885"),sQuery(id+"F0.wireOp",EDGE,"E1886"),sQuery(id+"F0.wireOp",EDGE,"E1887"),sQuery(id+"F0.wireOp",EDGE,"E1888"),sQuery(id+"F0.wireOp",EDGE,"E1889"),sQuery(id+"F0.wireOp",EDGE,"E1890"),sQuery(id+"F0.wireOp",EDGE,"E1891"),sQuery(id+"F0.wireOp",EDGE,"E1892"),sQuery(id+"F0.wireOp",EDGE,"E1893"),sQuery(id+"F0.wireOp",EDGE,"E1894"),sQuery(id+"F0.wireOp",EDGE,"E1895"),sQuery(id+"F0.wireOp",EDGE,"E1896"),sQuery(id+"F0.wireOp",EDGE,"E1897"),sQuery(id+"F0.wireOp",EDGE,"E1898"),sQuery(id+"F0.wireOp",EDGE,"E1899"),sQuery(id+"F0.wireOp",EDGE,"E1900"),sQuery(id+"F0.wireOp",EDGE,"E1901"),sQuery(id+"F0.wireOp",EDGE,"E1902"),sQuery(id+"F0.wireOp",EDGE,"E1903"),sQuery(id+"F0.wireOp",EDGE,"E1906"),sQuery(id+"F0.wireOp",EDGE,"E1907"),sQuery(id+"F0.wireOp",EDGE,"E1908"),sQuery(id+"F0.wireOp",EDGE,"E1909")])],"isStart":false});
            cPlane(context, id + "F2", {"entities" : qUnion([Q0]), "cplaneType" : CPlaneType.OFFSET, "offset" : 0 * mm, "width" : 152.4 * mm, "height" : 152.4 * mm});
        }
        {
            var Q0;
            Q0=qCreatedBy(id+"F2.planeOp",FACE);
            var sketch = newSketch(context, id + "F3", { "sketchPlane" : qUnion([Q0])});
            skLineSegment(sketch, "E2241.bottom", {"start": v(48.38, -28.06) * mm, "end": v(-49, -28.06) * mm});
            skLineSegment(sketch, "E2241.top", {"start": v(48.38, 28.1) * mm, "end": v(-49, 28.1) * mm});
            skLineSegment(sketch, "E2241.left", {"start": v(48.38, -28.06) * mm, "end": v(48.38, 28.1) * mm});
            skLineSegment(sketch, "E2241.right", {"start": v(-49, -28.06) * mm, "end": v(-49, 28.1) * mm});
            skSolve(sketch);
        }
        {
            var Q0;
            Q0 = qSketchRegion(id + "F3", true);
            var Q1;
            Q1=makeQuery(id+"F3.imprint","IMPRINT",FACE,{"disambiguationData":[TD([[makeQuery(id+"F3.imprint","IMPRINT",EDGE,{"derivedFrom":sQuery(id+"F3.wireOp",EDGE,"E2241.bottom")}),-1.0]])]});
            extrude(context, id + "F4", {"entities" : qUnion([Q0, Q1]), "operationType" : NewBodyOperationType.ADD, "oppositeDirection" : true, "depth" : 1 * mm});
        }
    });
